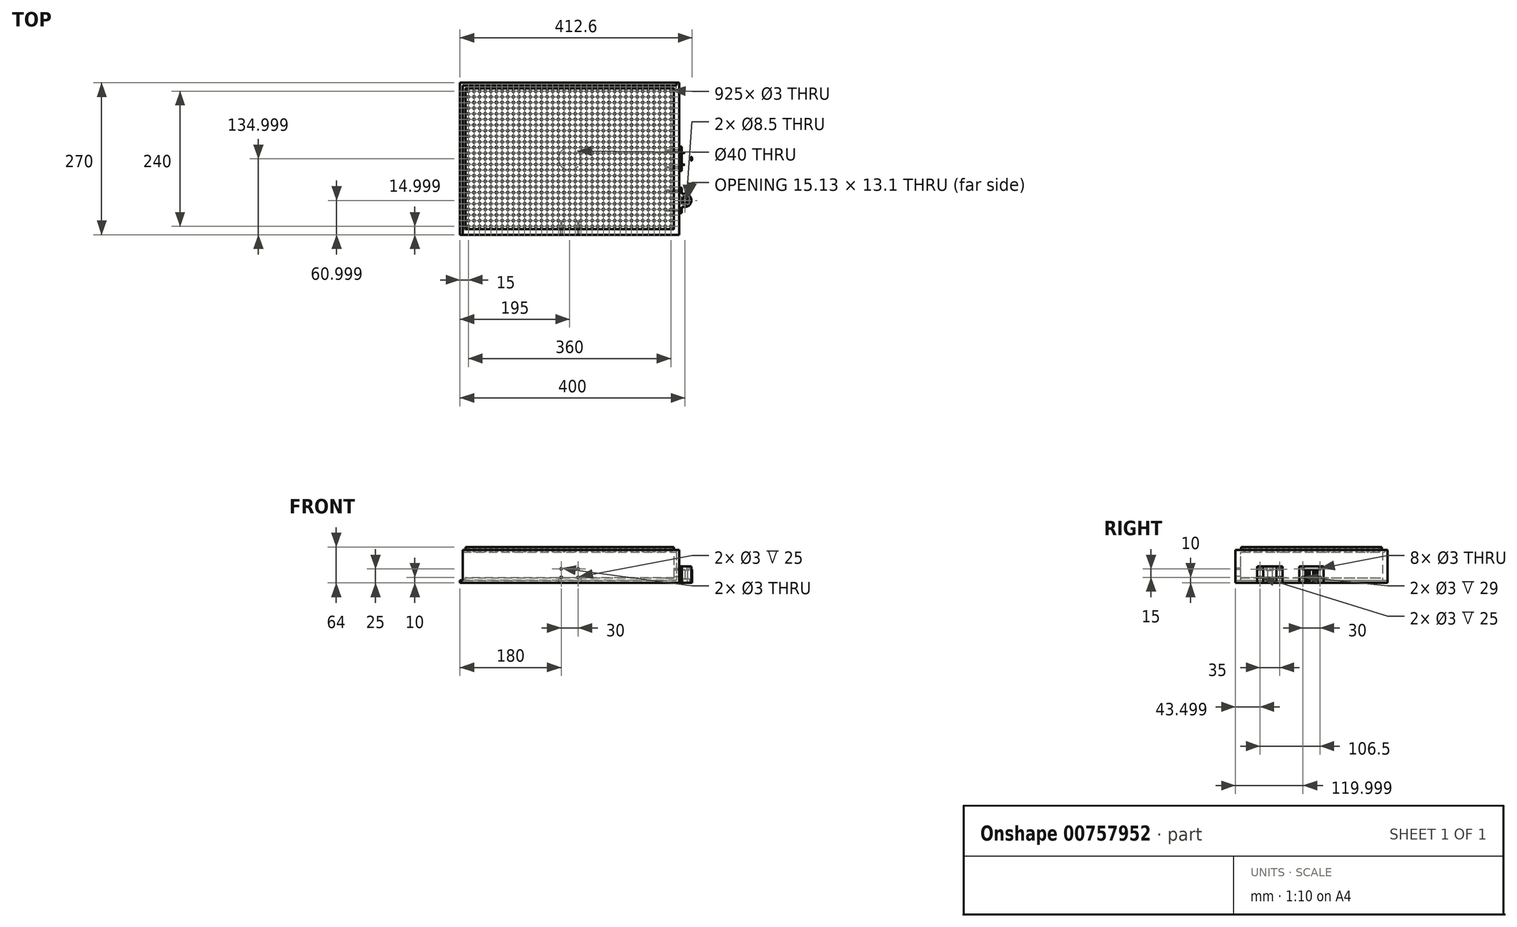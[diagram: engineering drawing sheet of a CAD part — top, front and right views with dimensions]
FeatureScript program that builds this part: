
annotation { "Feature Type Name" : "Feature", "Feature Type Description" : "" }
export const myFeature = defineFeature(function(context is Context, id is Id, definition is map)
    precondition{}
    {
        {
            var Q0;
            Q0=qCreatedBy(makeId("Top.planeOp"),FACE);
            var sketch = newSketch(context, id + "F0", { "sketchPlane" : qUnion([Q0])});
            skLineSegment(sketch, "E0.bottom", {"start": v(-146.05, 133.26) * mm, "end": v(223.95, 133.26) * mm});
            skLineSegment(sketch, "E0.top", {"start": v(-146.05, -116.74) * mm, "end": v(223.95, -116.74) * mm});
            skLineSegment(sketch, "E0.left", {"start": v(-146.05, 133.26) * mm, "end": v(-146.05, -116.74) * mm});
            skLineSegment(sketch, "E0.right", {"start": v(223.95, 133.26) * mm, "end": v(223.95, -116.74) * mm});
            skCircle(sketch, "E1", {"center": v(-141.05, -111.74) * mm, "radius": 1.5 * mm});
            skCircle(sketch, "E2.0.1.0", {"center": v(-141.05, -101.74) * mm, "radius": 1.5 * mm});
            skCircle(sketch, "E2.0.2.0", {"center": v(-141.05, -91.74) * mm, "radius": 1.5 * mm});
            skCircle(sketch, "E2.0.3.0", {"center": v(-141.05, -81.74) * mm, "radius": 1.5 * mm});
            skCircle(sketch, "E2.0.4.0", {"center": v(-141.05, -71.74) * mm, "radius": 1.5 * mm});
            skCircle(sketch, "E2.0.5.0", {"center": v(-141.05, -61.74) * mm, "radius": 1.5 * mm});
            skCircle(sketch, "E2.0.6.0", {"center": v(-141.05, -51.74) * mm, "radius": 1.5 * mm});
            skCircle(sketch, "E2.0.7.0", {"center": v(-141.05, -41.74) * mm, "radius": 1.5 * mm});
            skCircle(sketch, "E2.0.8.0", {"center": v(-141.05, -31.74) * mm, "radius": 1.5 * mm});
            skCircle(sketch, "E2.0.9.0", {"center": v(-141.05, -21.74) * mm, "radius": 1.5 * mm});
            skCircle(sketch, "E2.0.10.0", {"center": v(-141.05, -11.74) * mm, "radius": 1.5 * mm});
            skCircle(sketch, "E2.0.11.0", {"center": v(-141.05, -1.74) * mm, "radius": 1.5 * mm});
            skCircle(sketch, "E2.0.12.0", {"center": v(-141.05, 8.26) * mm, "radius": 1.5 * mm});
            skCircle(sketch, "E2.0.13.0", {"center": v(-141.05, 18.26) * mm, "radius": 1.5 * mm});
            skCircle(sketch, "E2.0.14.0", {"center": v(-141.05, 28.26) * mm, "radius": 1.5 * mm});
            skCircle(sketch, "E2.0.15.0", {"center": v(-141.05, 38.26) * mm, "radius": 1.5 * mm});
            skCircle(sketch, "E2.0.16.0", {"center": v(-141.05, 48.26) * mm, "radius": 1.5 * mm});
            skCircle(sketch, "E2.0.17.0", {"center": v(-141.05, 58.26) * mm, "radius": 1.5 * mm});
            skCircle(sketch, "E2.0.18.0", {"center": v(-141.05, 68.26) * mm, "radius": 1.5 * mm});
            skCircle(sketch, "E2.0.19.0", {"center": v(-141.05, 78.26) * mm, "radius": 1.5 * mm});
            skCircle(sketch, "E2.0.20.0", {"center": v(-141.05, 88.26) * mm, "radius": 1.5 * mm});
            skCircle(sketch, "E2.0.21.0", {"center": v(-141.05, 98.26) * mm, "radius": 1.5 * mm});
            skCircle(sketch, "E2.0.22.0", {"center": v(-141.05, 108.26) * mm, "radius": 1.5 * mm});
            skCircle(sketch, "E2.0.23.0", {"center": v(-141.05, 118.26) * mm, "radius": 1.5 * mm});
            skCircle(sketch, "E2.1.0.0", {"center": v(-131.05, -111.74) * mm, "radius": 1.5 * mm});
            skCircle(sketch, "E2.1.1.0", {"center": v(-131.05, -101.74) * mm, "radius": 1.5 * mm});
            skCircle(sketch, "E2.1.2.0", {"center": v(-131.05, -91.74) * mm, "radius": 1.5 * mm});
            skCircle(sketch, "E2.1.3.0", {"center": v(-131.05, -81.74) * mm, "radius": 1.5 * mm});
            skCircle(sketch, "E2.1.4.0", {"center": v(-131.05, -71.74) * mm, "radius": 1.5 * mm});
            skCircle(sketch, "E2.1.5.0", {"center": v(-131.05, -61.74) * mm, "radius": 1.5 * mm});
            skCircle(sketch, "E2.1.6.0", {"center": v(-131.05, -51.74) * mm, "radius": 1.5 * mm});
            skCircle(sketch, "E2.1.7.0", {"center": v(-131.05, -41.74) * mm, "radius": 1.5 * mm});
            skCircle(sketch, "E2.1.8.0", {"center": v(-131.05, -31.74) * mm, "radius": 1.5 * mm});
            skCircle(sketch, "E2.1.9.0", {"center": v(-131.05, -21.74) * mm, "radius": 1.5 * mm});
            skCircle(sketch, "E2.1.10.0", {"center": v(-131.05, -11.74) * mm, "radius": 1.5 * mm});
            skCircle(sketch, "E2.1.11.0", {"center": v(-131.05, -1.74) * mm, "radius": 1.5 * mm});
            skCircle(sketch, "E2.1.12.0", {"center": v(-131.05, 8.26) * mm, "radius": 1.5 * mm});
            skCircle(sketch, "E2.1.13.0", {"center": v(-131.05, 18.26) * mm, "radius": 1.5 * mm});
            skCircle(sketch, "E2.1.14.0", {"center": v(-131.05, 28.26) * mm, "radius": 1.5 * mm});
            skCircle(sketch, "E2.1.15.0", {"center": v(-131.05, 38.26) * mm, "radius": 1.5 * mm});
            skCircle(sketch, "E2.1.16.0", {"center": v(-131.05, 48.26) * mm, "radius": 1.5 * mm});
            skCircle(sketch, "E2.1.17.0", {"center": v(-131.05, 58.26) * mm, "radius": 1.5 * mm});
            skCircle(sketch, "E2.1.18.0", {"center": v(-131.05, 68.26) * mm, "radius": 1.5 * mm});
            skCircle(sketch, "E2.1.19.0", {"center": v(-131.05, 78.26) * mm, "radius": 1.5 * mm});
            skCircle(sketch, "E2.1.20.0", {"center": v(-131.05, 88.26) * mm, "radius": 1.5 * mm});
            skCircle(sketch, "E2.1.21.0", {"center": v(-131.05, 98.26) * mm, "radius": 1.5 * mm});
            skCircle(sketch, "E2.1.22.0", {"center": v(-131.05, 108.26) * mm, "radius": 1.5 * mm});
            skCircle(sketch, "E2.1.23.0", {"center": v(-131.05, 118.26) * mm, "radius": 1.5 * mm});
            skCircle(sketch, "E2.2.0.0", {"center": v(-121.05, -111.74) * mm, "radius": 1.5 * mm});
            skCircle(sketch, "E2.2.1.0", {"center": v(-121.05, -101.74) * mm, "radius": 1.5 * mm});
            skCircle(sketch, "E2.2.2.0", {"center": v(-121.05, -91.74) * mm, "radius": 1.5 * mm});
            skCircle(sketch, "E2.2.3.0", {"center": v(-121.05, -81.74) * mm, "radius": 1.5 * mm});
            skCircle(sketch, "E2.2.4.0", {"center": v(-121.05, -71.74) * mm, "radius": 1.5 * mm});
            skCircle(sketch, "E2.2.5.0", {"center": v(-121.05, -61.74) * mm, "radius": 1.5 * mm});
            skCircle(sketch, "E2.2.6.0", {"center": v(-121.05, -51.74) * mm, "radius": 1.5 * mm});
            skCircle(sketch, "E2.2.7.0", {"center": v(-121.05, -41.74) * mm, "radius": 1.5 * mm});
            skCircle(sketch, "E2.2.8.0", {"center": v(-121.05, -31.74) * mm, "radius": 1.5 * mm});
            skCircle(sketch, "E2.2.9.0", {"center": v(-121.05, -21.74) * mm, "radius": 1.5 * mm});
            skCircle(sketch, "E2.2.10.0", {"center": v(-121.05, -11.74) * mm, "radius": 1.5 * mm});
            skCircle(sketch, "E2.2.11.0", {"center": v(-121.05, -1.74) * mm, "radius": 1.5 * mm});
            skCircle(sketch, "E2.2.12.0", {"center": v(-121.05, 8.26) * mm, "radius": 1.5 * mm});
            skCircle(sketch, "E2.2.13.0", {"center": v(-121.05, 18.26) * mm, "radius": 1.5 * mm});
            skCircle(sketch, "E2.2.14.0", {"center": v(-121.05, 28.26) * mm, "radius": 1.5 * mm});
            skCircle(sketch, "E2.2.15.0", {"center": v(-121.05, 38.26) * mm, "radius": 1.5 * mm});
            skCircle(sketch, "E2.2.16.0", {"center": v(-121.05, 48.26) * mm, "radius": 1.5 * mm});
            skCircle(sketch, "E2.2.17.0", {"center": v(-121.05, 58.26) * mm, "radius": 1.5 * mm});
            skCircle(sketch, "E2.2.18.0", {"center": v(-121.05, 68.26) * mm, "radius": 1.5 * mm});
            skCircle(sketch, "E2.2.19.0", {"center": v(-121.05, 78.26) * mm, "radius": 1.5 * mm});
            skCircle(sketch, "E2.2.20.0", {"center": v(-121.05, 88.26) * mm, "radius": 1.5 * mm});
            skCircle(sketch, "E2.2.21.0", {"center": v(-121.05, 98.26) * mm, "radius": 1.5 * mm});
            skCircle(sketch, "E2.2.22.0", {"center": v(-121.05, 108.26) * mm, "radius": 1.5 * mm});
            skCircle(sketch, "E2.2.23.0", {"center": v(-121.05, 118.26) * mm, "radius": 1.5 * mm});
            skCircle(sketch, "E2.3.0.0", {"center": v(-111.05, -111.74) * mm, "radius": 1.5 * mm});
            skCircle(sketch, "E2.3.1.0", {"center": v(-111.05, -101.74) * mm, "radius": 1.5 * mm});
            skCircle(sketch, "E2.3.2.0", {"center": v(-111.05, -91.74) * mm, "radius": 1.5 * mm});
            skCircle(sketch, "E2.3.3.0", {"center": v(-111.05, -81.74) * mm, "radius": 1.5 * mm});
            skCircle(sketch, "E2.3.4.0", {"center": v(-111.05, -71.74) * mm, "radius": 1.5 * mm});
            skCircle(sketch, "E2.3.5.0", {"center": v(-111.05, -61.74) * mm, "radius": 1.5 * mm});
            skCircle(sketch, "E2.3.6.0", {"center": v(-111.05, -51.74) * mm, "radius": 1.5 * mm});
            skCircle(sketch, "E2.3.7.0", {"center": v(-111.05, -41.74) * mm, "radius": 1.5 * mm});
            skCircle(sketch, "E2.3.8.0", {"center": v(-111.05, -31.74) * mm, "radius": 1.5 * mm});
            skCircle(sketch, "E2.3.9.0", {"center": v(-111.05, -21.74) * mm, "radius": 1.5 * mm});
            skCircle(sketch, "E2.3.10.0", {"center": v(-111.05, -11.74) * mm, "radius": 1.5 * mm});
            skCircle(sketch, "E2.3.11.0", {"center": v(-111.05, -1.74) * mm, "radius": 1.5 * mm});
            skCircle(sketch, "E2.3.12.0", {"center": v(-111.05, 8.26) * mm, "radius": 1.5 * mm});
            skCircle(sketch, "E2.3.13.0", {"center": v(-111.05, 18.26) * mm, "radius": 1.5 * mm});
            skCircle(sketch, "E2.3.14.0", {"center": v(-111.05, 28.26) * mm, "radius": 1.5 * mm});
            skCircle(sketch, "E2.3.15.0", {"center": v(-111.05, 38.26) * mm, "radius": 1.5 * mm});
            skCircle(sketch, "E2.3.16.0", {"center": v(-111.05, 48.26) * mm, "radius": 1.5 * mm});
            skCircle(sketch, "E2.3.17.0", {"center": v(-111.05, 58.26) * mm, "radius": 1.5 * mm});
            skCircle(sketch, "E2.3.18.0", {"center": v(-111.05, 68.26) * mm, "radius": 1.5 * mm});
            skCircle(sketch, "E2.3.19.0", {"center": v(-111.05, 78.26) * mm, "radius": 1.5 * mm});
            skCircle(sketch, "E2.3.20.0", {"center": v(-111.05, 88.26) * mm, "radius": 1.5 * mm});
            skCircle(sketch, "E2.3.21.0", {"center": v(-111.05, 98.26) * mm, "radius": 1.5 * mm});
            skCircle(sketch, "E2.3.22.0", {"center": v(-111.05, 108.26) * mm, "radius": 1.5 * mm});
            skCircle(sketch, "E2.3.23.0", {"center": v(-111.05, 118.26) * mm, "radius": 1.5 * mm});
            skCircle(sketch, "E2.4.0.0", {"center": v(-101.05, -111.74) * mm, "radius": 1.5 * mm});
            skCircle(sketch, "E2.4.1.0", {"center": v(-101.05, -101.74) * mm, "radius": 1.5 * mm});
            skCircle(sketch, "E2.4.2.0", {"center": v(-101.05, -91.74) * mm, "radius": 1.5 * mm});
            skCircle(sketch, "E2.4.3.0", {"center": v(-101.05, -81.74) * mm, "radius": 1.5 * mm});
            skCircle(sketch, "E2.4.4.0", {"center": v(-101.05, -71.74) * mm, "radius": 1.5 * mm});
            skCircle(sketch, "E2.4.5.0", {"center": v(-101.05, -61.74) * mm, "radius": 1.5 * mm});
            skCircle(sketch, "E2.4.6.0", {"center": v(-101.05, -51.74) * mm, "radius": 1.5 * mm});
            skCircle(sketch, "E2.4.7.0", {"center": v(-101.05, -41.74) * mm, "radius": 1.5 * mm});
            skCircle(sketch, "E2.4.8.0", {"center": v(-101.05, -31.74) * mm, "radius": 1.5 * mm});
            skCircle(sketch, "E2.4.9.0", {"center": v(-101.05, -21.74) * mm, "radius": 1.5 * mm});
            skCircle(sketch, "E2.4.10.0", {"center": v(-101.05, -11.74) * mm, "radius": 1.5 * mm});
            skCircle(sketch, "E2.4.11.0", {"center": v(-101.05, -1.74) * mm, "radius": 1.5 * mm});
            skCircle(sketch, "E2.4.12.0", {"center": v(-101.05, 8.26) * mm, "radius": 1.5 * mm});
            skCircle(sketch, "E2.4.13.0", {"center": v(-101.05, 18.26) * mm, "radius": 1.5 * mm});
            skCircle(sketch, "E2.4.14.0", {"center": v(-101.05, 28.26) * mm, "radius": 1.5 * mm});
            skCircle(sketch, "E2.4.15.0", {"center": v(-101.05, 38.26) * mm, "radius": 1.5 * mm});
            skCircle(sketch, "E2.4.16.0", {"center": v(-101.05, 48.26) * mm, "radius": 1.5 * mm});
            skCircle(sketch, "E2.4.17.0", {"center": v(-101.05, 58.26) * mm, "radius": 1.5 * mm});
            skCircle(sketch, "E2.4.18.0", {"center": v(-101.05, 68.26) * mm, "radius": 1.5 * mm});
            skCircle(sketch, "E2.4.19.0", {"center": v(-101.05, 78.26) * mm, "radius": 1.5 * mm});
            skCircle(sketch, "E2.4.20.0", {"center": v(-101.05, 88.26) * mm, "radius": 1.5 * mm});
            skCircle(sketch, "E2.4.21.0", {"center": v(-101.05, 98.26) * mm, "radius": 1.5 * mm});
            skCircle(sketch, "E2.4.22.0", {"center": v(-101.05, 108.26) * mm, "radius": 1.5 * mm});
            skCircle(sketch, "E2.4.23.0", {"center": v(-101.05, 118.26) * mm, "radius": 1.5 * mm});
            skCircle(sketch, "E2.5.0.0", {"center": v(-91.05, -111.74) * mm, "radius": 1.5 * mm});
            skCircle(sketch, "E2.5.1.0", {"center": v(-91.05, -101.74) * mm, "radius": 1.5 * mm});
            skCircle(sketch, "E2.5.2.0", {"center": v(-91.05, -91.74) * mm, "radius": 1.5 * mm});
            skCircle(sketch, "E2.5.3.0", {"center": v(-91.05, -81.74) * mm, "radius": 1.5 * mm});
            skCircle(sketch, "E2.5.4.0", {"center": v(-91.05, -71.74) * mm, "radius": 1.5 * mm});
            skCircle(sketch, "E2.5.5.0", {"center": v(-91.05, -61.74) * mm, "radius": 1.5 * mm});
            skCircle(sketch, "E2.5.6.0", {"center": v(-91.05, -51.74) * mm, "radius": 1.5 * mm});
            skCircle(sketch, "E2.5.7.0", {"center": v(-91.05, -41.74) * mm, "radius": 1.5 * mm});
            skCircle(sketch, "E2.5.8.0", {"center": v(-91.05, -31.74) * mm, "radius": 1.5 * mm});
            skCircle(sketch, "E2.5.9.0", {"center": v(-91.05, -21.74) * mm, "radius": 1.5 * mm});
            skCircle(sketch, "E2.5.10.0", {"center": v(-91.05, -11.74) * mm, "radius": 1.5 * mm});
            skCircle(sketch, "E2.5.11.0", {"center": v(-91.05, -1.74) * mm, "radius": 1.5 * mm});
            skCircle(sketch, "E2.5.12.0", {"center": v(-91.05, 8.26) * mm, "radius": 1.5 * mm});
            skCircle(sketch, "E2.5.13.0", {"center": v(-91.05, 18.26) * mm, "radius": 1.5 * mm});
            skCircle(sketch, "E2.5.14.0", {"center": v(-91.05, 28.26) * mm, "radius": 1.5 * mm});
            skCircle(sketch, "E2.5.15.0", {"center": v(-91.05, 38.26) * mm, "radius": 1.5 * mm});
            skCircle(sketch, "E2.5.16.0", {"center": v(-91.05, 48.26) * mm, "radius": 1.5 * mm});
            skCircle(sketch, "E2.5.17.0", {"center": v(-91.05, 58.26) * mm, "radius": 1.5 * mm});
            skCircle(sketch, "E2.5.18.0", {"center": v(-91.05, 68.26) * mm, "radius": 1.5 * mm});
            skCircle(sketch, "E2.5.19.0", {"center": v(-91.05, 78.26) * mm, "radius": 1.5 * mm});
            skCircle(sketch, "E2.5.20.0", {"center": v(-91.05, 88.26) * mm, "radius": 1.5 * mm});
            skCircle(sketch, "E2.5.21.0", {"center": v(-91.05, 98.26) * mm, "radius": 1.5 * mm});
            skCircle(sketch, "E2.5.22.0", {"center": v(-91.05, 108.26) * mm, "radius": 1.5 * mm});
            skCircle(sketch, "E2.5.23.0", {"center": v(-91.05, 118.26) * mm, "radius": 1.5 * mm});
            skCircle(sketch, "E2.6.0.0", {"center": v(-81.05, -111.74) * mm, "radius": 1.5 * mm});
            skCircle(sketch, "E2.6.1.0", {"center": v(-81.05, -101.74) * mm, "radius": 1.5 * mm});
            skCircle(sketch, "E2.6.2.0", {"center": v(-81.05, -91.74) * mm, "radius": 1.5 * mm});
            skCircle(sketch, "E2.6.3.0", {"center": v(-81.05, -81.74) * mm, "radius": 1.5 * mm});
            skCircle(sketch, "E2.6.4.0", {"center": v(-81.05, -71.74) * mm, "radius": 1.5 * mm});
            skCircle(sketch, "E2.6.5.0", {"center": v(-81.05, -61.74) * mm, "radius": 1.5 * mm});
            skCircle(sketch, "E2.6.6.0", {"center": v(-81.05, -51.74) * mm, "radius": 1.5 * mm});
            skCircle(sketch, "E2.6.7.0", {"center": v(-81.05, -41.74) * mm, "radius": 1.5 * mm});
            skCircle(sketch, "E2.6.8.0", {"center": v(-81.05, -31.74) * mm, "radius": 1.5 * mm});
            skCircle(sketch, "E2.6.9.0", {"center": v(-81.05, -21.74) * mm, "radius": 1.5 * mm});
            skCircle(sketch, "E2.6.10.0", {"center": v(-81.05, -11.74) * mm, "radius": 1.5 * mm});
            skCircle(sketch, "E2.6.11.0", {"center": v(-81.05, -1.74) * mm, "radius": 1.5 * mm});
            skCircle(sketch, "E2.6.12.0", {"center": v(-81.05, 8.26) * mm, "radius": 1.5 * mm});
            skCircle(sketch, "E2.6.13.0", {"center": v(-81.05, 18.26) * mm, "radius": 1.5 * mm});
            skCircle(sketch, "E2.6.14.0", {"center": v(-81.05, 28.26) * mm, "radius": 1.5 * mm});
            skCircle(sketch, "E2.6.15.0", {"center": v(-81.05, 38.26) * mm, "radius": 1.5 * mm});
            skCircle(sketch, "E2.6.16.0", {"center": v(-81.05, 48.26) * mm, "radius": 1.5 * mm});
            skCircle(sketch, "E2.6.17.0", {"center": v(-81.05, 58.26) * mm, "radius": 1.5 * mm});
            skCircle(sketch, "E2.6.18.0", {"center": v(-81.05, 68.26) * mm, "radius": 1.5 * mm});
            skCircle(sketch, "E2.6.19.0", {"center": v(-81.05, 78.26) * mm, "radius": 1.5 * mm});
            skCircle(sketch, "E2.6.20.0", {"center": v(-81.05, 88.26) * mm, "radius": 1.5 * mm});
            skCircle(sketch, "E2.6.21.0", {"center": v(-81.05, 98.26) * mm, "radius": 1.5 * mm});
            skCircle(sketch, "E2.6.22.0", {"center": v(-81.05, 108.26) * mm, "radius": 1.5 * mm});
            skCircle(sketch, "E2.6.23.0", {"center": v(-81.05, 118.26) * mm, "radius": 1.5 * mm});
            skCircle(sketch, "E2.7.0.0", {"center": v(-71.05, -111.74) * mm, "radius": 1.5 * mm});
            skCircle(sketch, "E2.7.1.0", {"center": v(-71.05, -101.74) * mm, "radius": 1.5 * mm});
            skCircle(sketch, "E2.7.2.0", {"center": v(-71.05, -91.74) * mm, "radius": 1.5 * mm});
            skCircle(sketch, "E2.7.3.0", {"center": v(-71.05, -81.74) * mm, "radius": 1.5 * mm});
            skCircle(sketch, "E2.7.4.0", {"center": v(-71.05, -71.74) * mm, "radius": 1.5 * mm});
            skCircle(sketch, "E2.7.5.0", {"center": v(-71.05, -61.74) * mm, "radius": 1.5 * mm});
            skCircle(sketch, "E2.7.6.0", {"center": v(-71.05, -51.74) * mm, "radius": 1.5 * mm});
            skCircle(sketch, "E2.7.7.0", {"center": v(-71.05, -41.74) * mm, "radius": 1.5 * mm});
            skCircle(sketch, "E2.7.8.0", {"center": v(-71.05, -31.74) * mm, "radius": 1.5 * mm});
            skCircle(sketch, "E2.7.9.0", {"center": v(-71.05, -21.74) * mm, "radius": 1.5 * mm});
            skCircle(sketch, "E2.7.10.0", {"center": v(-71.05, -11.74) * mm, "radius": 1.5 * mm});
            skCircle(sketch, "E2.7.11.0", {"center": v(-71.05, -1.74) * mm, "radius": 1.5 * mm});
            skCircle(sketch, "E2.7.12.0", {"center": v(-71.05, 8.26) * mm, "radius": 1.5 * mm});
            skCircle(sketch, "E2.7.13.0", {"center": v(-71.05, 18.26) * mm, "radius": 1.5 * mm});
            skCircle(sketch, "E2.7.14.0", {"center": v(-71.05, 28.26) * mm, "radius": 1.5 * mm});
            skCircle(sketch, "E2.7.15.0", {"center": v(-71.05, 38.26) * mm, "radius": 1.5 * mm});
            skCircle(sketch, "E2.7.16.0", {"center": v(-71.05, 48.26) * mm, "radius": 1.5 * mm});
            skCircle(sketch, "E2.7.17.0", {"center": v(-71.05, 58.26) * mm, "radius": 1.5 * mm});
            skCircle(sketch, "E2.7.18.0", {"center": v(-71.05, 68.26) * mm, "radius": 1.5 * mm});
            skCircle(sketch, "E2.7.19.0", {"center": v(-71.05, 78.26) * mm, "radius": 1.5 * mm});
            skCircle(sketch, "E2.7.20.0", {"center": v(-71.05, 88.26) * mm, "radius": 1.5 * mm});
            skCircle(sketch, "E2.7.21.0", {"center": v(-71.05, 98.26) * mm, "radius": 1.5 * mm});
            skCircle(sketch, "E2.7.22.0", {"center": v(-71.05, 108.26) * mm, "radius": 1.5 * mm});
            skCircle(sketch, "E2.7.23.0", {"center": v(-71.05, 118.26) * mm, "radius": 1.5 * mm});
            skCircle(sketch, "E2.8.0.0", {"center": v(-61.05, -111.74) * mm, "radius": 1.5 * mm});
            skCircle(sketch, "E2.8.1.0", {"center": v(-61.05, -101.74) * mm, "radius": 1.5 * mm});
            skCircle(sketch, "E2.8.2.0", {"center": v(-61.05, -91.74) * mm, "radius": 1.5 * mm});
            skCircle(sketch, "E2.8.3.0", {"center": v(-61.05, -81.74) * mm, "radius": 1.5 * mm});
            skCircle(sketch, "E2.8.4.0", {"center": v(-61.05, -71.74) * mm, "radius": 1.5 * mm});
            skCircle(sketch, "E2.8.5.0", {"center": v(-61.05, -61.74) * mm, "radius": 1.5 * mm});
            skCircle(sketch, "E2.8.6.0", {"center": v(-61.05, -51.74) * mm, "radius": 1.5 * mm});
            skCircle(sketch, "E2.8.7.0", {"center": v(-61.05, -41.74) * mm, "radius": 1.5 * mm});
            skCircle(sketch, "E2.8.8.0", {"center": v(-61.05, -31.74) * mm, "radius": 1.5 * mm});
            skCircle(sketch, "E2.8.9.0", {"center": v(-61.05, -21.74) * mm, "radius": 1.5 * mm});
            skCircle(sketch, "E2.8.10.0", {"center": v(-61.05, -11.74) * mm, "radius": 1.5 * mm});
            skCircle(sketch, "E2.8.11.0", {"center": v(-61.05, -1.74) * mm, "radius": 1.5 * mm});
            skCircle(sketch, "E2.8.12.0", {"center": v(-61.05, 8.26) * mm, "radius": 1.5 * mm});
            skCircle(sketch, "E2.8.13.0", {"center": v(-61.05, 18.26) * mm, "radius": 1.5 * mm});
            skCircle(sketch, "E2.8.14.0", {"center": v(-61.05, 28.26) * mm, "radius": 1.5 * mm});
            skCircle(sketch, "E2.8.15.0", {"center": v(-61.05, 38.26) * mm, "radius": 1.5 * mm});
            skCircle(sketch, "E2.8.16.0", {"center": v(-61.05, 48.26) * mm, "radius": 1.5 * mm});
            skCircle(sketch, "E2.8.17.0", {"center": v(-61.05, 58.26) * mm, "radius": 1.5 * mm});
            skCircle(sketch, "E2.8.18.0", {"center": v(-61.05, 68.26) * mm, "radius": 1.5 * mm});
            skCircle(sketch, "E2.8.19.0", {"center": v(-61.05, 78.26) * mm, "radius": 1.5 * mm});
            skCircle(sketch, "E2.8.20.0", {"center": v(-61.05, 88.26) * mm, "radius": 1.5 * mm});
            skCircle(sketch, "E2.8.21.0", {"center": v(-61.05, 98.26) * mm, "radius": 1.5 * mm});
            skCircle(sketch, "E2.8.22.0", {"center": v(-61.05, 108.26) * mm, "radius": 1.5 * mm});
            skCircle(sketch, "E2.8.23.0", {"center": v(-61.05, 118.26) * mm, "radius": 1.5 * mm});
            skCircle(sketch, "E2.9.0.0", {"center": v(-51.05, -111.74) * mm, "radius": 1.5 * mm});
            skCircle(sketch, "E2.9.1.0", {"center": v(-51.05, -101.74) * mm, "radius": 1.5 * mm});
            skCircle(sketch, "E2.9.2.0", {"center": v(-51.05, -91.74) * mm, "radius": 1.5 * mm});
            skCircle(sketch, "E2.9.3.0", {"center": v(-51.05, -81.74) * mm, "radius": 1.5 * mm});
            skCircle(sketch, "E2.9.4.0", {"center": v(-51.05, -71.74) * mm, "radius": 1.5 * mm});
            skCircle(sketch, "E2.9.5.0", {"center": v(-51.05, -61.74) * mm, "radius": 1.5 * mm});
            skCircle(sketch, "E2.9.6.0", {"center": v(-51.05, -51.74) * mm, "radius": 1.5 * mm});
            skCircle(sketch, "E2.9.7.0", {"center": v(-51.05, -41.74) * mm, "radius": 1.5 * mm});
            skCircle(sketch, "E2.9.8.0", {"center": v(-51.05, -31.74) * mm, "radius": 1.5 * mm});
            skCircle(sketch, "E2.9.9.0", {"center": v(-51.05, -21.74) * mm, "radius": 1.5 * mm});
            skCircle(sketch, "E2.9.10.0", {"center": v(-51.05, -11.74) * mm, "radius": 1.5 * mm});
            skCircle(sketch, "E2.9.11.0", {"center": v(-51.05, -1.74) * mm, "radius": 1.5 * mm});
            skCircle(sketch, "E2.9.12.0", {"center": v(-51.05, 8.26) * mm, "radius": 1.5 * mm});
            skCircle(sketch, "E2.9.13.0", {"center": v(-51.05, 18.26) * mm, "radius": 1.5 * mm});
            skCircle(sketch, "E2.9.14.0", {"center": v(-51.05, 28.26) * mm, "radius": 1.5 * mm});
            skCircle(sketch, "E2.9.15.0", {"center": v(-51.05, 38.26) * mm, "radius": 1.5 * mm});
            skCircle(sketch, "E2.9.16.0", {"center": v(-51.05, 48.26) * mm, "radius": 1.5 * mm});
            skCircle(sketch, "E2.9.17.0", {"center": v(-51.05, 58.26) * mm, "radius": 1.5 * mm});
            skCircle(sketch, "E2.9.18.0", {"center": v(-51.05, 68.26) * mm, "radius": 1.5 * mm});
            skCircle(sketch, "E2.9.19.0", {"center": v(-51.05, 78.26) * mm, "radius": 1.5 * mm});
            skCircle(sketch, "E2.9.20.0", {"center": v(-51.05, 88.26) * mm, "radius": 1.5 * mm});
            skCircle(sketch, "E2.9.21.0", {"center": v(-51.05, 98.26) * mm, "radius": 1.5 * mm});
            skCircle(sketch, "E2.9.22.0", {"center": v(-51.05, 108.26) * mm, "radius": 1.5 * mm});
            skCircle(sketch, "E2.9.23.0", {"center": v(-51.05, 118.26) * mm, "radius": 1.5 * mm});
            skCircle(sketch, "E2.10.0.0", {"center": v(-41.05, -111.74) * mm, "radius": 1.5 * mm});
            skCircle(sketch, "E2.10.1.0", {"center": v(-41.05, -101.74) * mm, "radius": 1.5 * mm});
            skCircle(sketch, "E2.10.2.0", {"center": v(-41.05, -91.74) * mm, "radius": 1.5 * mm});
            skCircle(sketch, "E2.10.3.0", {"center": v(-41.05, -81.74) * mm, "radius": 1.5 * mm});
            skCircle(sketch, "E2.10.4.0", {"center": v(-41.05, -71.74) * mm, "radius": 1.5 * mm});
            skCircle(sketch, "E2.10.5.0", {"center": v(-41.05, -61.74) * mm, "radius": 1.5 * mm});
            skCircle(sketch, "E2.10.6.0", {"center": v(-41.05, -51.74) * mm, "radius": 1.5 * mm});
            skCircle(sketch, "E2.10.7.0", {"center": v(-41.05, -41.74) * mm, "radius": 1.5 * mm});
            skCircle(sketch, "E2.10.8.0", {"center": v(-41.05, -31.74) * mm, "radius": 1.5 * mm});
            skCircle(sketch, "E2.10.9.0", {"center": v(-41.05, -21.74) * mm, "radius": 1.5 * mm});
            skCircle(sketch, "E2.10.10.0", {"center": v(-41.05, -11.74) * mm, "radius": 1.5 * mm});
            skCircle(sketch, "E2.10.11.0", {"center": v(-41.05, -1.74) * mm, "radius": 1.5 * mm});
            skCircle(sketch, "E2.10.12.0", {"center": v(-41.05, 8.26) * mm, "radius": 1.5 * mm});
            skCircle(sketch, "E2.10.13.0", {"center": v(-41.05, 18.26) * mm, "radius": 1.5 * mm});
            skCircle(sketch, "E2.10.14.0", {"center": v(-41.05, 28.26) * mm, "radius": 1.5 * mm});
            skCircle(sketch, "E2.10.15.0", {"center": v(-41.05, 38.26) * mm, "radius": 1.5 * mm});
            skCircle(sketch, "E2.10.16.0", {"center": v(-41.05, 48.26) * mm, "radius": 1.5 * mm});
            skCircle(sketch, "E2.10.17.0", {"center": v(-41.05, 58.26) * mm, "radius": 1.5 * mm});
            skCircle(sketch, "E2.10.18.0", {"center": v(-41.05, 68.26) * mm, "radius": 1.5 * mm});
            skCircle(sketch, "E2.10.19.0", {"center": v(-41.05, 78.26) * mm, "radius": 1.5 * mm});
            skCircle(sketch, "E2.10.20.0", {"center": v(-41.05, 88.26) * mm, "radius": 1.5 * mm});
            skCircle(sketch, "E2.10.21.0", {"center": v(-41.05, 98.26) * mm, "radius": 1.5 * mm});
            skCircle(sketch, "E2.10.22.0", {"center": v(-41.05, 108.26) * mm, "radius": 1.5 * mm});
            skCircle(sketch, "E2.10.23.0", {"center": v(-41.05, 118.26) * mm, "radius": 1.5 * mm});
            skCircle(sketch, "E2.11.0.0", {"center": v(-31.05, -111.74) * mm, "radius": 1.5 * mm});
            skCircle(sketch, "E2.11.1.0", {"center": v(-31.05, -101.74) * mm, "radius": 1.5 * mm});
            skCircle(sketch, "E2.11.2.0", {"center": v(-31.05, -91.74) * mm, "radius": 1.5 * mm});
            skCircle(sketch, "E2.11.3.0", {"center": v(-31.05, -81.74) * mm, "radius": 1.5 * mm});
            skCircle(sketch, "E2.11.4.0", {"center": v(-31.05, -71.74) * mm, "radius": 1.5 * mm});
            skCircle(sketch, "E2.11.5.0", {"center": v(-31.05, -61.74) * mm, "radius": 1.5 * mm});
            skCircle(sketch, "E2.11.6.0", {"center": v(-31.05, -51.74) * mm, "radius": 1.5 * mm});
            skCircle(sketch, "E2.11.7.0", {"center": v(-31.05, -41.74) * mm, "radius": 1.5 * mm});
            skCircle(sketch, "E2.11.8.0", {"center": v(-31.05, -31.74) * mm, "radius": 1.5 * mm});
            skCircle(sketch, "E2.11.9.0", {"center": v(-31.05, -21.74) * mm, "radius": 1.5 * mm});
            skCircle(sketch, "E2.11.10.0", {"center": v(-31.05, -11.74) * mm, "radius": 1.5 * mm});
            skCircle(sketch, "E2.11.11.0", {"center": v(-31.05, -1.74) * mm, "radius": 1.5 * mm});
            skCircle(sketch, "E2.11.12.0", {"center": v(-31.05, 8.26) * mm, "radius": 1.5 * mm});
            skCircle(sketch, "E2.11.13.0", {"center": v(-31.05, 18.26) * mm, "radius": 1.5 * mm});
            skCircle(sketch, "E2.11.14.0", {"center": v(-31.05, 28.26) * mm, "radius": 1.5 * mm});
            skCircle(sketch, "E2.11.15.0", {"center": v(-31.05, 38.26) * mm, "radius": 1.5 * mm});
            skCircle(sketch, "E2.11.16.0", {"center": v(-31.05, 48.26) * mm, "radius": 1.5 * mm});
            skCircle(sketch, "E2.11.17.0", {"center": v(-31.05, 58.26) * mm, "radius": 1.5 * mm});
            skCircle(sketch, "E2.11.18.0", {"center": v(-31.05, 68.26) * mm, "radius": 1.5 * mm});
            skCircle(sketch, "E2.11.19.0", {"center": v(-31.05, 78.26) * mm, "radius": 1.5 * mm});
            skCircle(sketch, "E2.11.20.0", {"center": v(-31.05, 88.26) * mm, "radius": 1.5 * mm});
            skCircle(sketch, "E2.11.21.0", {"center": v(-31.05, 98.26) * mm, "radius": 1.5 * mm});
            skCircle(sketch, "E2.11.22.0", {"center": v(-31.05, 108.26) * mm, "radius": 1.5 * mm});
            skCircle(sketch, "E2.11.23.0", {"center": v(-31.05, 118.26) * mm, "radius": 1.5 * mm});
            skCircle(sketch, "E2.12.0.0", {"center": v(-21.05, -111.74) * mm, "radius": 1.5 * mm});
            skCircle(sketch, "E2.12.1.0", {"center": v(-21.05, -101.74) * mm, "radius": 1.5 * mm});
            skCircle(sketch, "E2.12.2.0", {"center": v(-21.05, -91.74) * mm, "radius": 1.5 * mm});
            skCircle(sketch, "E2.12.3.0", {"center": v(-21.05, -81.74) * mm, "radius": 1.5 * mm});
            skCircle(sketch, "E2.12.4.0", {"center": v(-21.05, -71.74) * mm, "radius": 1.5 * mm});
            skCircle(sketch, "E2.12.5.0", {"center": v(-21.05, -61.74) * mm, "radius": 1.5 * mm});
            skCircle(sketch, "E2.12.6.0", {"center": v(-21.05, -51.74) * mm, "radius": 1.5 * mm});
            skCircle(sketch, "E2.12.7.0", {"center": v(-21.05, -41.74) * mm, "radius": 1.5 * mm});
            skCircle(sketch, "E2.12.8.0", {"center": v(-21.05, -31.74) * mm, "radius": 1.5 * mm});
            skCircle(sketch, "E2.12.9.0", {"center": v(-21.05, -21.74) * mm, "radius": 1.5 * mm});
            skCircle(sketch, "E2.12.10.0", {"center": v(-21.05, -11.74) * mm, "radius": 1.5 * mm});
            skCircle(sketch, "E2.12.11.0", {"center": v(-21.05, -1.74) * mm, "radius": 1.5 * mm});
            skCircle(sketch, "E2.12.12.0", {"center": v(-21.05, 8.26) * mm, "radius": 1.5 * mm});
            skCircle(sketch, "E2.12.13.0", {"center": v(-21.05, 18.26) * mm, "radius": 1.5 * mm});
            skCircle(sketch, "E2.12.14.0", {"center": v(-21.05, 28.26) * mm, "radius": 1.5 * mm});
            skCircle(sketch, "E2.12.15.0", {"center": v(-21.05, 38.26) * mm, "radius": 1.5 * mm});
            skCircle(sketch, "E2.12.16.0", {"center": v(-21.05, 48.26) * mm, "radius": 1.5 * mm});
            skCircle(sketch, "E2.12.17.0", {"center": v(-21.05, 58.26) * mm, "radius": 1.5 * mm});
            skCircle(sketch, "E2.12.18.0", {"center": v(-21.05, 68.26) * mm, "radius": 1.5 * mm});
            skCircle(sketch, "E2.12.19.0", {"center": v(-21.05, 78.26) * mm, "radius": 1.5 * mm});
            skCircle(sketch, "E2.12.20.0", {"center": v(-21.05, 88.26) * mm, "radius": 1.5 * mm});
            skCircle(sketch, "E2.12.21.0", {"center": v(-21.05, 98.26) * mm, "radius": 1.5 * mm});
            skCircle(sketch, "E2.12.22.0", {"center": v(-21.05, 108.26) * mm, "radius": 1.5 * mm});
            skCircle(sketch, "E2.12.23.0", {"center": v(-21.05, 118.26) * mm, "radius": 1.5 * mm});
            skCircle(sketch, "E2.13.0.0", {"center": v(-11.05, -111.74) * mm, "radius": 1.5 * mm});
            skCircle(sketch, "E2.13.1.0", {"center": v(-11.05, -101.74) * mm, "radius": 1.5 * mm});
            skCircle(sketch, "E2.13.2.0", {"center": v(-11.05, -91.74) * mm, "radius": 1.5 * mm});
            skCircle(sketch, "E2.13.3.0", {"center": v(-11.05, -81.74) * mm, "radius": 1.5 * mm});
            skCircle(sketch, "E2.13.4.0", {"center": v(-11.05, -71.74) * mm, "radius": 1.5 * mm});
            skCircle(sketch, "E2.13.5.0", {"center": v(-11.05, -61.74) * mm, "radius": 1.5 * mm});
            skCircle(sketch, "E2.13.6.0", {"center": v(-11.05, -51.74) * mm, "radius": 1.5 * mm});
            skCircle(sketch, "E2.13.7.0", {"center": v(-11.05, -41.74) * mm, "radius": 1.5 * mm});
            skCircle(sketch, "E2.13.8.0", {"center": v(-11.05, -31.74) * mm, "radius": 1.5 * mm});
            skCircle(sketch, "E2.13.9.0", {"center": v(-11.05, -21.74) * mm, "radius": 1.5 * mm});
            skCircle(sketch, "E2.13.10.0", {"center": v(-11.05, -11.74) * mm, "radius": 1.5 * mm});
            skCircle(sketch, "E2.13.11.0", {"center": v(-11.05, -1.74) * mm, "radius": 1.5 * mm});
            skCircle(sketch, "E2.13.12.0", {"center": v(-11.05, 8.26) * mm, "radius": 1.5 * mm});
            skCircle(sketch, "E2.13.13.0", {"center": v(-11.05, 18.26) * mm, "radius": 1.5 * mm});
            skCircle(sketch, "E2.13.14.0", {"center": v(-11.05, 28.26) * mm, "radius": 1.5 * mm});
            skCircle(sketch, "E2.13.15.0", {"center": v(-11.05, 38.26) * mm, "radius": 1.5 * mm});
            skCircle(sketch, "E2.13.16.0", {"center": v(-11.05, 48.26) * mm, "radius": 1.5 * mm});
            skCircle(sketch, "E2.13.17.0", {"center": v(-11.05, 58.26) * mm, "radius": 1.5 * mm});
            skCircle(sketch, "E2.13.18.0", {"center": v(-11.05, 68.26) * mm, "radius": 1.5 * mm});
            skCircle(sketch, "E2.13.19.0", {"center": v(-11.05, 78.26) * mm, "radius": 1.5 * mm});
            skCircle(sketch, "E2.13.20.0", {"center": v(-11.05, 88.26) * mm, "radius": 1.5 * mm});
            skCircle(sketch, "E2.13.21.0", {"center": v(-11.05, 98.26) * mm, "radius": 1.5 * mm});
            skCircle(sketch, "E2.13.22.0", {"center": v(-11.05, 108.26) * mm, "radius": 1.5 * mm});
            skCircle(sketch, "E2.13.23.0", {"center": v(-11.05, 118.26) * mm, "radius": 1.5 * mm});
            skCircle(sketch, "E2.14.0.0", {"center": v(-1.05, -111.74) * mm, "radius": 1.5 * mm});
            skCircle(sketch, "E2.14.1.0", {"center": v(-1.05, -101.74) * mm, "radius": 1.5 * mm});
            skCircle(sketch, "E2.14.2.0", {"center": v(-1.05, -91.74) * mm, "radius": 1.5 * mm});
            skCircle(sketch, "E2.14.3.0", {"center": v(-1.05, -81.74) * mm, "radius": 1.5 * mm});
            skCircle(sketch, "E2.14.4.0", {"center": v(-1.05, -71.74) * mm, "radius": 1.5 * mm});
            skCircle(sketch, "E2.14.5.0", {"center": v(-1.05, -61.74) * mm, "radius": 1.5 * mm});
            skCircle(sketch, "E2.14.6.0", {"center": v(-1.05, -51.74) * mm, "radius": 1.5 * mm});
            skCircle(sketch, "E2.14.7.0", {"center": v(-1.05, -41.74) * mm, "radius": 1.5 * mm});
            skCircle(sketch, "E2.14.8.0", {"center": v(-1.05, -31.74) * mm, "radius": 1.5 * mm});
            skCircle(sketch, "E2.14.9.0", {"center": v(-1.05, -21.74) * mm, "radius": 1.5 * mm});
            skCircle(sketch, "E2.14.10.0", {"center": v(-1.05, -11.74) * mm, "radius": 1.5 * mm});
            skCircle(sketch, "E2.14.11.0", {"center": v(-1.05, -1.74) * mm, "radius": 1.5 * mm});
            skCircle(sketch, "E2.14.12.0", {"center": v(-1.05, 8.26) * mm, "radius": 1.5 * mm});
            skCircle(sketch, "E2.14.13.0", {"center": v(-1.05, 18.26) * mm, "radius": 1.5 * mm});
            skCircle(sketch, "E2.14.14.0", {"center": v(-1.05, 28.26) * mm, "radius": 1.5 * mm});
            skCircle(sketch, "E2.14.15.0", {"center": v(-1.05, 38.26) * mm, "radius": 1.5 * mm});
            skCircle(sketch, "E2.14.16.0", {"center": v(-1.05, 48.26) * mm, "radius": 1.5 * mm});
            skCircle(sketch, "E2.14.17.0", {"center": v(-1.05, 58.26) * mm, "radius": 1.5 * mm});
            skCircle(sketch, "E2.14.18.0", {"center": v(-1.05, 68.26) * mm, "radius": 1.5 * mm});
            skCircle(sketch, "E2.14.19.0", {"center": v(-1.05, 78.26) * mm, "radius": 1.5 * mm});
            skCircle(sketch, "E2.14.20.0", {"center": v(-1.05, 88.26) * mm, "radius": 1.5 * mm});
            skCircle(sketch, "E2.14.21.0", {"center": v(-1.05, 98.26) * mm, "radius": 1.5 * mm});
            skCircle(sketch, "E2.14.22.0", {"center": v(-1.05, 108.26) * mm, "radius": 1.5 * mm});
            skCircle(sketch, "E2.14.23.0", {"center": v(-1.05, 118.26) * mm, "radius": 1.5 * mm});
            skCircle(sketch, "E2.15.0.0", {"center": v(8.95, -111.74) * mm, "radius": 1.5 * mm});
            skCircle(sketch, "E2.15.1.0", {"center": v(8.95, -101.74) * mm, "radius": 1.5 * mm});
            skCircle(sketch, "E2.15.2.0", {"center": v(8.95, -91.74) * mm, "radius": 1.5 * mm});
            skCircle(sketch, "E2.15.3.0", {"center": v(8.95, -81.74) * mm, "radius": 1.5 * mm});
            skCircle(sketch, "E2.15.4.0", {"center": v(8.95, -71.74) * mm, "radius": 1.5 * mm});
            skCircle(sketch, "E2.15.5.0", {"center": v(8.95, -61.74) * mm, "radius": 1.5 * mm});
            skCircle(sketch, "E2.15.6.0", {"center": v(8.95, -51.74) * mm, "radius": 1.5 * mm});
            skCircle(sketch, "E2.15.7.0", {"center": v(8.95, -41.74) * mm, "radius": 1.5 * mm});
            skCircle(sketch, "E2.15.8.0", {"center": v(8.95, -31.74) * mm, "radius": 1.5 * mm});
            skCircle(sketch, "E2.15.9.0", {"center": v(8.95, -21.74) * mm, "radius": 1.5 * mm});
            skCircle(sketch, "E2.15.10.0", {"center": v(8.95, -11.74) * mm, "radius": 1.5 * mm});
            skCircle(sketch, "E2.15.11.0", {"center": v(8.95, -1.74) * mm, "radius": 1.5 * mm});
            skCircle(sketch, "E2.15.12.0", {"center": v(8.95, 8.26) * mm, "radius": 1.5 * mm});
            skCircle(sketch, "E2.15.13.0", {"center": v(8.95, 18.26) * mm, "radius": 1.5 * mm});
            skCircle(sketch, "E2.15.14.0", {"center": v(8.95, 28.26) * mm, "radius": 1.5 * mm});
            skCircle(sketch, "E2.15.15.0", {"center": v(8.95, 38.26) * mm, "radius": 1.5 * mm});
            skCircle(sketch, "E2.15.16.0", {"center": v(8.95, 48.26) * mm, "radius": 1.5 * mm});
            skCircle(sketch, "E2.15.17.0", {"center": v(8.95, 58.26) * mm, "radius": 1.5 * mm});
            skCircle(sketch, "E2.15.18.0", {"center": v(8.95, 68.26) * mm, "radius": 1.5 * mm});
            skCircle(sketch, "E2.15.19.0", {"center": v(8.95, 78.26) * mm, "radius": 1.5 * mm});
            skCircle(sketch, "E2.15.20.0", {"center": v(8.95, 88.26) * mm, "radius": 1.5 * mm});
            skCircle(sketch, "E2.15.21.0", {"center": v(8.95, 98.26) * mm, "radius": 1.5 * mm});
            skCircle(sketch, "E2.15.22.0", {"center": v(8.95, 108.26) * mm, "radius": 1.5 * mm});
            skCircle(sketch, "E2.15.23.0", {"center": v(8.95, 118.26) * mm, "radius": 1.5 * mm});
            skCircle(sketch, "E2.16.0.0", {"center": v(18.95, -111.74) * mm, "radius": 1.5 * mm});
            skCircle(sketch, "E2.16.1.0", {"center": v(18.95, -101.74) * mm, "radius": 1.5 * mm});
            skCircle(sketch, "E2.16.2.0", {"center": v(18.95, -91.74) * mm, "radius": 1.5 * mm});
            skCircle(sketch, "E2.16.3.0", {"center": v(18.95, -81.74) * mm, "radius": 1.5 * mm});
            skCircle(sketch, "E2.16.4.0", {"center": v(18.95, -71.74) * mm, "radius": 1.5 * mm});
            skCircle(sketch, "E2.16.5.0", {"center": v(18.95, -61.74) * mm, "radius": 1.5 * mm});
            skCircle(sketch, "E2.16.6.0", {"center": v(18.95, -51.74) * mm, "radius": 1.5 * mm});
            skCircle(sketch, "E2.16.7.0", {"center": v(18.95, -41.74) * mm, "radius": 1.5 * mm});
            skCircle(sketch, "E2.16.8.0", {"center": v(18.95, -31.74) * mm, "radius": 1.5 * mm});
            skCircle(sketch, "E2.16.9.0", {"center": v(18.95, -21.74) * mm, "radius": 1.5 * mm});
            skCircle(sketch, "E2.16.10.0", {"center": v(18.95, -11.74) * mm, "radius": 1.5 * mm});
            skCircle(sketch, "E2.16.11.0", {"center": v(18.95, -1.74) * mm, "radius": 1.5 * mm});
            skCircle(sketch, "E2.16.12.0", {"center": v(18.95, 8.26) * mm, "radius": 1.5 * mm});
            skCircle(sketch, "E2.16.13.0", {"center": v(18.95, 18.26) * mm, "radius": 1.5 * mm});
            skCircle(sketch, "E2.16.14.0", {"center": v(18.95, 28.26) * mm, "radius": 1.5 * mm});
            skCircle(sketch, "E2.16.15.0", {"center": v(18.95, 38.26) * mm, "radius": 1.5 * mm});
            skCircle(sketch, "E2.16.16.0", {"center": v(18.95, 48.26) * mm, "radius": 1.5 * mm});
            skCircle(sketch, "E2.16.17.0", {"center": v(18.95, 58.26) * mm, "radius": 1.5 * mm});
            skCircle(sketch, "E2.16.18.0", {"center": v(18.95, 68.26) * mm, "radius": 1.5 * mm});
            skCircle(sketch, "E2.16.19.0", {"center": v(18.95, 78.26) * mm, "radius": 1.5 * mm});
            skCircle(sketch, "E2.16.20.0", {"center": v(18.95, 88.26) * mm, "radius": 1.5 * mm});
            skCircle(sketch, "E2.16.21.0", {"center": v(18.95, 98.26) * mm, "radius": 1.5 * mm});
            skCircle(sketch, "E2.16.22.0", {"center": v(18.95, 108.26) * mm, "radius": 1.5 * mm});
            skCircle(sketch, "E2.16.23.0", {"center": v(18.95, 118.26) * mm, "radius": 1.5 * mm});
            skCircle(sketch, "E2.17.0.0", {"center": v(28.95, -111.74) * mm, "radius": 1.5 * mm});
            skCircle(sketch, "E2.17.1.0", {"center": v(28.95, -101.74) * mm, "radius": 1.5 * mm});
            skCircle(sketch, "E2.17.2.0", {"center": v(28.95, -91.74) * mm, "radius": 1.5 * mm});
            skCircle(sketch, "E2.17.3.0", {"center": v(28.95, -81.74) * mm, "radius": 1.5 * mm});
            skCircle(sketch, "E2.17.4.0", {"center": v(28.95, -71.74) * mm, "radius": 1.5 * mm});
            skCircle(sketch, "E2.17.5.0", {"center": v(28.95, -61.74) * mm, "radius": 1.5 * mm});
            skCircle(sketch, "E2.17.6.0", {"center": v(28.95, -51.74) * mm, "radius": 1.5 * mm});
            skCircle(sketch, "E2.17.7.0", {"center": v(28.95, -41.74) * mm, "radius": 1.5 * mm});
            skCircle(sketch, "E2.17.8.0", {"center": v(28.95, -31.74) * mm, "radius": 1.5 * mm});
            skCircle(sketch, "E2.17.9.0", {"center": v(28.95, -21.74) * mm, "radius": 1.5 * mm});
            skCircle(sketch, "E2.17.10.0", {"center": v(28.95, -11.74) * mm, "radius": 1.5 * mm});
            skCircle(sketch, "E2.17.11.0", {"center": v(28.95, -1.74) * mm, "radius": 1.5 * mm});
            skCircle(sketch, "E2.17.12.0", {"center": v(28.95, 8.26) * mm, "radius": 1.5 * mm});
            skCircle(sketch, "E2.17.13.0", {"center": v(28.95, 18.26) * mm, "radius": 1.5 * mm});
            skCircle(sketch, "E2.17.14.0", {"center": v(28.95, 28.26) * mm, "radius": 1.5 * mm});
            skCircle(sketch, "E2.17.15.0", {"center": v(28.95, 38.26) * mm, "radius": 1.5 * mm});
            skCircle(sketch, "E2.17.16.0", {"center": v(28.95, 48.26) * mm, "radius": 1.5 * mm});
            skCircle(sketch, "E2.17.17.0", {"center": v(28.95, 58.26) * mm, "radius": 1.5 * mm});
            skCircle(sketch, "E2.17.18.0", {"center": v(28.95, 68.26) * mm, "radius": 1.5 * mm});
            skCircle(sketch, "E2.17.19.0", {"center": v(28.95, 78.26) * mm, "radius": 1.5 * mm});
            skCircle(sketch, "E2.17.20.0", {"center": v(28.95, 88.26) * mm, "radius": 1.5 * mm});
            skCircle(sketch, "E2.17.21.0", {"center": v(28.95, 98.26) * mm, "radius": 1.5 * mm});
            skCircle(sketch, "E2.17.22.0", {"center": v(28.95, 108.26) * mm, "radius": 1.5 * mm});
            skCircle(sketch, "E2.17.23.0", {"center": v(28.95, 118.26) * mm, "radius": 1.5 * mm});
            skCircle(sketch, "E2.18.0.0", {"center": v(38.95, -111.74) * mm, "radius": 1.5 * mm});
            skCircle(sketch, "E2.18.1.0", {"center": v(38.95, -101.74) * mm, "radius": 1.5 * mm});
            skCircle(sketch, "E2.18.2.0", {"center": v(38.95, -91.74) * mm, "radius": 1.5 * mm});
            skCircle(sketch, "E2.18.3.0", {"center": v(38.95, -81.74) * mm, "radius": 1.5 * mm});
            skCircle(sketch, "E2.18.4.0", {"center": v(38.95, -71.74) * mm, "radius": 1.5 * mm});
            skCircle(sketch, "E2.18.5.0", {"center": v(38.95, -61.74) * mm, "radius": 1.5 * mm});
            skCircle(sketch, "E2.18.6.0", {"center": v(38.95, -51.74) * mm, "radius": 1.5 * mm});
            skCircle(sketch, "E2.18.7.0", {"center": v(38.95, -41.74) * mm, "radius": 1.5 * mm});
            skCircle(sketch, "E2.18.8.0", {"center": v(38.95, -31.74) * mm, "radius": 1.5 * mm});
            skCircle(sketch, "E2.18.9.0", {"center": v(38.95, -21.74) * mm, "radius": 1.5 * mm});
            skCircle(sketch, "E2.18.10.0", {"center": v(38.95, -11.74) * mm, "radius": 1.5 * mm});
            skCircle(sketch, "E2.18.11.0", {"center": v(38.95, -1.74) * mm, "radius": 1.5 * mm});
            skCircle(sketch, "E2.18.12.0", {"center": v(38.95, 8.26) * mm, "radius": 1.5 * mm});
            skCircle(sketch, "E2.18.13.0", {"center": v(38.95, 18.26) * mm, "radius": 1.5 * mm});
            skCircle(sketch, "E2.18.14.0", {"center": v(38.95, 28.26) * mm, "radius": 1.5 * mm});
            skCircle(sketch, "E2.18.15.0", {"center": v(38.95, 38.26) * mm, "radius": 1.5 * mm});
            skCircle(sketch, "E2.18.16.0", {"center": v(38.95, 48.26) * mm, "radius": 1.5 * mm});
            skCircle(sketch, "E2.18.17.0", {"center": v(38.95, 58.26) * mm, "radius": 1.5 * mm});
            skCircle(sketch, "E2.18.18.0", {"center": v(38.95, 68.26) * mm, "radius": 1.5 * mm});
            skCircle(sketch, "E2.18.19.0", {"center": v(38.95, 78.26) * mm, "radius": 1.5 * mm});
            skCircle(sketch, "E2.18.20.0", {"center": v(38.95, 88.26) * mm, "radius": 1.5 * mm});
            skCircle(sketch, "E2.18.21.0", {"center": v(38.95, 98.26) * mm, "radius": 1.5 * mm});
            skCircle(sketch, "E2.18.22.0", {"center": v(38.95, 108.26) * mm, "radius": 1.5 * mm});
            skCircle(sketch, "E2.18.23.0", {"center": v(38.95, 118.26) * mm, "radius": 1.5 * mm});
            skCircle(sketch, "E2.19.0.0", {"center": v(48.95, -111.74) * mm, "radius": 1.5 * mm});
            skCircle(sketch, "E2.19.1.0", {"center": v(48.95, -101.74) * mm, "radius": 1.5 * mm});
            skCircle(sketch, "E2.19.2.0", {"center": v(48.95, -91.74) * mm, "radius": 1.5 * mm});
            skCircle(sketch, "E2.19.3.0", {"center": v(48.95, -81.74) * mm, "radius": 1.5 * mm});
            skCircle(sketch, "E2.19.4.0", {"center": v(48.95, -71.74) * mm, "radius": 1.5 * mm});
            skCircle(sketch, "E2.19.5.0", {"center": v(48.95, -61.74) * mm, "radius": 1.5 * mm});
            skCircle(sketch, "E2.19.6.0", {"center": v(48.95, -51.74) * mm, "radius": 1.5 * mm});
            skCircle(sketch, "E2.19.7.0", {"center": v(48.95, -41.74) * mm, "radius": 1.5 * mm});
            skCircle(sketch, "E2.19.8.0", {"center": v(48.95, -31.74) * mm, "radius": 1.5 * mm});
            skCircle(sketch, "E2.19.9.0", {"center": v(48.95, -21.74) * mm, "radius": 1.5 * mm});
            skCircle(sketch, "E2.19.10.0", {"center": v(48.95, -11.74) * mm, "radius": 1.5 * mm});
            skCircle(sketch, "E2.19.11.0", {"center": v(48.95, -1.74) * mm, "radius": 1.5 * mm});
            skCircle(sketch, "E2.19.12.0", {"center": v(48.95, 8.26) * mm, "radius": 1.5 * mm});
            skCircle(sketch, "E2.19.13.0", {"center": v(48.95, 18.26) * mm, "radius": 1.5 * mm});
            skCircle(sketch, "E2.19.14.0", {"center": v(48.95, 28.26) * mm, "radius": 1.5 * mm});
            skCircle(sketch, "E2.19.15.0", {"center": v(48.95, 38.26) * mm, "radius": 1.5 * mm});
            skCircle(sketch, "E2.19.16.0", {"center": v(48.95, 48.26) * mm, "radius": 1.5 * mm});
            skCircle(sketch, "E2.19.17.0", {"center": v(48.95, 58.26) * mm, "radius": 1.5 * mm});
            skCircle(sketch, "E2.19.18.0", {"center": v(48.95, 68.26) * mm, "radius": 1.5 * mm});
            skCircle(sketch, "E2.19.19.0", {"center": v(48.95, 78.26) * mm, "radius": 1.5 * mm});
            skCircle(sketch, "E2.19.20.0", {"center": v(48.95, 88.26) * mm, "radius": 1.5 * mm});
            skCircle(sketch, "E2.19.21.0", {"center": v(48.95, 98.26) * mm, "radius": 1.5 * mm});
            skCircle(sketch, "E2.19.22.0", {"center": v(48.95, 108.26) * mm, "radius": 1.5 * mm});
            skCircle(sketch, "E2.19.23.0", {"center": v(48.95, 118.26) * mm, "radius": 1.5 * mm});
            skCircle(sketch, "E2.20.0.0", {"center": v(58.95, -111.74) * mm, "radius": 1.5 * mm});
            skCircle(sketch, "E2.20.1.0", {"center": v(58.95, -101.74) * mm, "radius": 1.5 * mm});
            skCircle(sketch, "E2.20.2.0", {"center": v(58.95, -91.74) * mm, "radius": 1.5 * mm});
            skCircle(sketch, "E2.20.3.0", {"center": v(58.95, -81.74) * mm, "radius": 1.5 * mm});
            skCircle(sketch, "E2.20.4.0", {"center": v(58.95, -71.74) * mm, "radius": 1.5 * mm});
            skCircle(sketch, "E2.20.5.0", {"center": v(58.95, -61.74) * mm, "radius": 1.5 * mm});
            skCircle(sketch, "E2.20.6.0", {"center": v(58.95, -51.74) * mm, "radius": 1.5 * mm});
            skCircle(sketch, "E2.20.7.0", {"center": v(58.95, -41.74) * mm, "radius": 1.5 * mm});
            skCircle(sketch, "E2.20.8.0", {"center": v(58.95, -31.74) * mm, "radius": 1.5 * mm});
            skCircle(sketch, "E2.20.9.0", {"center": v(58.95, -21.74) * mm, "radius": 1.5 * mm});
            skCircle(sketch, "E2.20.10.0", {"center": v(58.95, -11.74) * mm, "radius": 1.5 * mm});
            skCircle(sketch, "E2.20.11.0", {"center": v(58.95, -1.74) * mm, "radius": 1.5 * mm});
            skCircle(sketch, "E2.20.12.0", {"center": v(58.95, 8.26) * mm, "radius": 1.5 * mm});
            skCircle(sketch, "E2.20.13.0", {"center": v(58.95, 18.26) * mm, "radius": 1.5 * mm});
            skCircle(sketch, "E2.20.14.0", {"center": v(58.95, 28.26) * mm, "radius": 1.5 * mm});
            skCircle(sketch, "E2.20.15.0", {"center": v(58.95, 38.26) * mm, "radius": 1.5 * mm});
            skCircle(sketch, "E2.20.16.0", {"center": v(58.95, 48.26) * mm, "radius": 1.5 * mm});
            skCircle(sketch, "E2.20.17.0", {"center": v(58.95, 58.26) * mm, "radius": 1.5 * mm});
            skCircle(sketch, "E2.20.18.0", {"center": v(58.95, 68.26) * mm, "radius": 1.5 * mm});
            skCircle(sketch, "E2.20.19.0", {"center": v(58.95, 78.26) * mm, "radius": 1.5 * mm});
            skCircle(sketch, "E2.20.20.0", {"center": v(58.95, 88.26) * mm, "radius": 1.5 * mm});
            skCircle(sketch, "E2.20.21.0", {"center": v(58.95, 98.26) * mm, "radius": 1.5 * mm});
            skCircle(sketch, "E2.20.22.0", {"center": v(58.95, 108.26) * mm, "radius": 1.5 * mm});
            skCircle(sketch, "E2.20.23.0", {"center": v(58.95, 118.26) * mm, "radius": 1.5 * mm});
            skCircle(sketch, "E2.21.0.0", {"center": v(68.95, -111.74) * mm, "radius": 1.5 * mm});
            skCircle(sketch, "E2.21.1.0", {"center": v(68.95, -101.74) * mm, "radius": 1.5 * mm});
            skCircle(sketch, "E2.21.2.0", {"center": v(68.95, -91.74) * mm, "radius": 1.5 * mm});
            skCircle(sketch, "E2.21.3.0", {"center": v(68.95, -81.74) * mm, "radius": 1.5 * mm});
            skCircle(sketch, "E2.21.4.0", {"center": v(68.95, -71.74) * mm, "radius": 1.5 * mm});
            skCircle(sketch, "E2.21.5.0", {"center": v(68.95, -61.74) * mm, "radius": 1.5 * mm});
            skCircle(sketch, "E2.21.6.0", {"center": v(68.95, -51.74) * mm, "radius": 1.5 * mm});
            skCircle(sketch, "E2.21.7.0", {"center": v(68.95, -41.74) * mm, "radius": 1.5 * mm});
            skCircle(sketch, "E2.21.8.0", {"center": v(68.95, -31.74) * mm, "radius": 1.5 * mm});
            skCircle(sketch, "E2.21.9.0", {"center": v(68.95, -21.74) * mm, "radius": 1.5 * mm});
            skCircle(sketch, "E2.21.10.0", {"center": v(68.95, -11.74) * mm, "radius": 1.5 * mm});
            skCircle(sketch, "E2.21.11.0", {"center": v(68.95, -1.74) * mm, "radius": 1.5 * mm});
            skCircle(sketch, "E2.21.12.0", {"center": v(68.95, 8.26) * mm, "radius": 1.5 * mm});
            skCircle(sketch, "E2.21.13.0", {"center": v(68.95, 18.26) * mm, "radius": 1.5 * mm});
            skCircle(sketch, "E2.21.14.0", {"center": v(68.95, 28.26) * mm, "radius": 1.5 * mm});
            skCircle(sketch, "E2.21.15.0", {"center": v(68.95, 38.26) * mm, "radius": 1.5 * mm});
            skCircle(sketch, "E2.21.16.0", {"center": v(68.95, 48.26) * mm, "radius": 1.5 * mm});
            skCircle(sketch, "E2.21.17.0", {"center": v(68.95, 58.26) * mm, "radius": 1.5 * mm});
            skCircle(sketch, "E2.21.18.0", {"center": v(68.95, 68.26) * mm, "radius": 1.5 * mm});
            skCircle(sketch, "E2.21.19.0", {"center": v(68.95, 78.26) * mm, "radius": 1.5 * mm});
            skCircle(sketch, "E2.21.20.0", {"center": v(68.95, 88.26) * mm, "radius": 1.5 * mm});
            skCircle(sketch, "E2.21.21.0", {"center": v(68.95, 98.26) * mm, "radius": 1.5 * mm});
            skCircle(sketch, "E2.21.22.0", {"center": v(68.95, 108.26) * mm, "radius": 1.5 * mm});
            skCircle(sketch, "E2.21.23.0", {"center": v(68.95, 118.26) * mm, "radius": 1.5 * mm});
            skCircle(sketch, "E2.22.0.0", {"center": v(78.95, -111.74) * mm, "radius": 1.5 * mm});
            skCircle(sketch, "E2.22.1.0", {"center": v(78.95, -101.74) * mm, "radius": 1.5 * mm});
            skCircle(sketch, "E2.22.2.0", {"center": v(78.95, -91.74) * mm, "radius": 1.5 * mm});
            skCircle(sketch, "E2.22.3.0", {"center": v(78.95, -81.74) * mm, "radius": 1.5 * mm});
            skCircle(sketch, "E2.22.4.0", {"center": v(78.95, -71.74) * mm, "radius": 1.5 * mm});
            skCircle(sketch, "E2.22.5.0", {"center": v(78.95, -61.74) * mm, "radius": 1.5 * mm});
            skCircle(sketch, "E2.22.6.0", {"center": v(78.95, -51.74) * mm, "radius": 1.5 * mm});
            skCircle(sketch, "E2.22.7.0", {"center": v(78.95, -41.74) * mm, "radius": 1.5 * mm});
            skCircle(sketch, "E2.22.8.0", {"center": v(78.95, -31.74) * mm, "radius": 1.5 * mm});
            skCircle(sketch, "E2.22.9.0", {"center": v(78.95, -21.74) * mm, "radius": 1.5 * mm});
            skCircle(sketch, "E2.22.10.0", {"center": v(78.95, -11.74) * mm, "radius": 1.5 * mm});
            skCircle(sketch, "E2.22.11.0", {"center": v(78.95, -1.74) * mm, "radius": 1.5 * mm});
            skCircle(sketch, "E2.22.12.0", {"center": v(78.95, 8.26) * mm, "radius": 1.5 * mm});
            skCircle(sketch, "E2.22.13.0", {"center": v(78.95, 18.26) * mm, "radius": 1.5 * mm});
            skCircle(sketch, "E2.22.14.0", {"center": v(78.95, 28.26) * mm, "radius": 1.5 * mm});
            skCircle(sketch, "E2.22.15.0", {"center": v(78.95, 38.26) * mm, "radius": 1.5 * mm});
            skCircle(sketch, "E2.22.16.0", {"center": v(78.95, 48.26) * mm, "radius": 1.5 * mm});
            skCircle(sketch, "E2.22.17.0", {"center": v(78.95, 58.26) * mm, "radius": 1.5 * mm});
            skCircle(sketch, "E2.22.18.0", {"center": v(78.95, 68.26) * mm, "radius": 1.5 * mm});
            skCircle(sketch, "E2.22.19.0", {"center": v(78.95, 78.26) * mm, "radius": 1.5 * mm});
            skCircle(sketch, "E2.22.20.0", {"center": v(78.95, 88.26) * mm, "radius": 1.5 * mm});
            skCircle(sketch, "E2.22.21.0", {"center": v(78.95, 98.26) * mm, "radius": 1.5 * mm});
            skCircle(sketch, "E2.22.22.0", {"center": v(78.95, 108.26) * mm, "radius": 1.5 * mm});
            skCircle(sketch, "E2.22.23.0", {"center": v(78.95, 118.26) * mm, "radius": 1.5 * mm});
            skCircle(sketch, "E2.23.0.0", {"center": v(88.95, -111.74) * mm, "radius": 1.5 * mm});
            skCircle(sketch, "E2.23.1.0", {"center": v(88.95, -101.74) * mm, "radius": 1.5 * mm});
            skCircle(sketch, "E2.23.2.0", {"center": v(88.95, -91.74) * mm, "radius": 1.5 * mm});
            skCircle(sketch, "E2.23.3.0", {"center": v(88.95, -81.74) * mm, "radius": 1.5 * mm});
            skCircle(sketch, "E2.23.4.0", {"center": v(88.95, -71.74) * mm, "radius": 1.5 * mm});
            skCircle(sketch, "E2.23.5.0", {"center": v(88.95, -61.74) * mm, "radius": 1.5 * mm});
            skCircle(sketch, "E2.23.6.0", {"center": v(88.95, -51.74) * mm, "radius": 1.5 * mm});
            skCircle(sketch, "E2.23.7.0", {"center": v(88.95, -41.74) * mm, "radius": 1.5 * mm});
            skCircle(sketch, "E2.23.8.0", {"center": v(88.95, -31.74) * mm, "radius": 1.5 * mm});
            skCircle(sketch, "E2.23.9.0", {"center": v(88.95, -21.74) * mm, "radius": 1.5 * mm});
            skCircle(sketch, "E2.23.10.0", {"center": v(88.95, -11.74) * mm, "radius": 1.5 * mm});
            skCircle(sketch, "E2.23.11.0", {"center": v(88.95, -1.74) * mm, "radius": 1.5 * mm});
            skCircle(sketch, "E2.23.12.0", {"center": v(88.95, 8.26) * mm, "radius": 1.5 * mm});
            skCircle(sketch, "E2.23.13.0", {"center": v(88.95, 18.26) * mm, "radius": 1.5 * mm});
            skCircle(sketch, "E2.23.14.0", {"center": v(88.95, 28.26) * mm, "radius": 1.5 * mm});
            skCircle(sketch, "E2.23.15.0", {"center": v(88.95, 38.26) * mm, "radius": 1.5 * mm});
            skCircle(sketch, "E2.23.16.0", {"center": v(88.95, 48.26) * mm, "radius": 1.5 * mm});
            skCircle(sketch, "E2.23.17.0", {"center": v(88.95, 58.26) * mm, "radius": 1.5 * mm});
            skCircle(sketch, "E2.23.18.0", {"center": v(88.95, 68.26) * mm, "radius": 1.5 * mm});
            skCircle(sketch, "E2.23.19.0", {"center": v(88.95, 78.26) * mm, "radius": 1.5 * mm});
            skCircle(sketch, "E2.23.20.0", {"center": v(88.95, 88.26) * mm, "radius": 1.5 * mm});
            skCircle(sketch, "E2.23.21.0", {"center": v(88.95, 98.26) * mm, "radius": 1.5 * mm});
            skCircle(sketch, "E2.23.22.0", {"center": v(88.95, 108.26) * mm, "radius": 1.5 * mm});
            skCircle(sketch, "E2.23.23.0", {"center": v(88.95, 118.26) * mm, "radius": 1.5 * mm});
            skCircle(sketch, "E2.24.0.0", {"center": v(98.95, -111.74) * mm, "radius": 1.5 * mm});
            skCircle(sketch, "E2.24.1.0", {"center": v(98.95, -101.74) * mm, "radius": 1.5 * mm});
            skCircle(sketch, "E2.24.2.0", {"center": v(98.95, -91.74) * mm, "radius": 1.5 * mm});
            skCircle(sketch, "E2.24.3.0", {"center": v(98.95, -81.74) * mm, "radius": 1.5 * mm});
            skCircle(sketch, "E2.24.4.0", {"center": v(98.95, -71.74) * mm, "radius": 1.5 * mm});
            skCircle(sketch, "E2.24.5.0", {"center": v(98.95, -61.74) * mm, "radius": 1.5 * mm});
            skCircle(sketch, "E2.24.6.0", {"center": v(98.95, -51.74) * mm, "radius": 1.5 * mm});
            skCircle(sketch, "E2.24.7.0", {"center": v(98.95, -41.74) * mm, "radius": 1.5 * mm});
            skCircle(sketch, "E2.24.8.0", {"center": v(98.95, -31.74) * mm, "radius": 1.5 * mm});
            skCircle(sketch, "E2.24.9.0", {"center": v(98.95, -21.74) * mm, "radius": 1.5 * mm});
            skCircle(sketch, "E2.24.10.0", {"center": v(98.95, -11.74) * mm, "radius": 1.5 * mm});
            skCircle(sketch, "E2.24.11.0", {"center": v(98.95, -1.74) * mm, "radius": 1.5 * mm});
            skCircle(sketch, "E2.24.12.0", {"center": v(98.95, 8.26) * mm, "radius": 1.5 * mm});
            skCircle(sketch, "E2.24.13.0", {"center": v(98.95, 18.26) * mm, "radius": 1.5 * mm});
            skCircle(sketch, "E2.24.14.0", {"center": v(98.95, 28.26) * mm, "radius": 1.5 * mm});
            skCircle(sketch, "E2.24.15.0", {"center": v(98.95, 38.26) * mm, "radius": 1.5 * mm});
            skCircle(sketch, "E2.24.16.0", {"center": v(98.95, 48.26) * mm, "radius": 1.5 * mm});
            skCircle(sketch, "E2.24.17.0", {"center": v(98.95, 58.26) * mm, "radius": 1.5 * mm});
            skCircle(sketch, "E2.24.18.0", {"center": v(98.95, 68.26) * mm, "radius": 1.5 * mm});
            skCircle(sketch, "E2.24.19.0", {"center": v(98.95, 78.26) * mm, "radius": 1.5 * mm});
            skCircle(sketch, "E2.24.20.0", {"center": v(98.95, 88.26) * mm, "radius": 1.5 * mm});
            skCircle(sketch, "E2.24.21.0", {"center": v(98.95, 98.26) * mm, "radius": 1.5 * mm});
            skCircle(sketch, "E2.24.22.0", {"center": v(98.95, 108.26) * mm, "radius": 1.5 * mm});
            skCircle(sketch, "E2.24.23.0", {"center": v(98.95, 118.26) * mm, "radius": 1.5 * mm});
            skCircle(sketch, "E2.25.0.0", {"center": v(108.95, -111.74) * mm, "radius": 1.5 * mm});
            skCircle(sketch, "E2.25.1.0", {"center": v(108.95, -101.74) * mm, "radius": 1.5 * mm});
            skCircle(sketch, "E2.25.2.0", {"center": v(108.95, -91.74) * mm, "radius": 1.5 * mm});
            skCircle(sketch, "E2.25.3.0", {"center": v(108.95, -81.74) * mm, "radius": 1.5 * mm});
            skCircle(sketch, "E2.25.4.0", {"center": v(108.95, -71.74) * mm, "radius": 1.5 * mm});
            skCircle(sketch, "E2.25.5.0", {"center": v(108.95, -61.74) * mm, "radius": 1.5 * mm});
            skCircle(sketch, "E2.25.6.0", {"center": v(108.95, -51.74) * mm, "radius": 1.5 * mm});
            skCircle(sketch, "E2.25.7.0", {"center": v(108.95, -41.74) * mm, "radius": 1.5 * mm});
            skCircle(sketch, "E2.25.8.0", {"center": v(108.95, -31.74) * mm, "radius": 1.5 * mm});
            skCircle(sketch, "E2.25.9.0", {"center": v(108.95, -21.74) * mm, "radius": 1.5 * mm});
            skCircle(sketch, "E2.25.10.0", {"center": v(108.95, -11.74) * mm, "radius": 1.5 * mm});
            skCircle(sketch, "E2.25.11.0", {"center": v(108.95, -1.74) * mm, "radius": 1.5 * mm});
            skCircle(sketch, "E2.25.12.0", {"center": v(108.95, 8.26) * mm, "radius": 1.5 * mm});
            skCircle(sketch, "E2.25.13.0", {"center": v(108.95, 18.26) * mm, "radius": 1.5 * mm});
            skCircle(sketch, "E2.25.14.0", {"center": v(108.95, 28.26) * mm, "radius": 1.5 * mm});
            skCircle(sketch, "E2.25.15.0", {"center": v(108.95, 38.26) * mm, "radius": 1.5 * mm});
            skCircle(sketch, "E2.25.16.0", {"center": v(108.95, 48.26) * mm, "radius": 1.5 * mm});
            skCircle(sketch, "E2.25.17.0", {"center": v(108.95, 58.26) * mm, "radius": 1.5 * mm});
            skCircle(sketch, "E2.25.18.0", {"center": v(108.95, 68.26) * mm, "radius": 1.5 * mm});
            skCircle(sketch, "E2.25.19.0", {"center": v(108.95, 78.26) * mm, "radius": 1.5 * mm});
            skCircle(sketch, "E2.25.20.0", {"center": v(108.95, 88.26) * mm, "radius": 1.5 * mm});
            skCircle(sketch, "E2.25.21.0", {"center": v(108.95, 98.26) * mm, "radius": 1.5 * mm});
            skCircle(sketch, "E2.25.22.0", {"center": v(108.95, 108.26) * mm, "radius": 1.5 * mm});
            skCircle(sketch, "E2.25.23.0", {"center": v(108.95, 118.26) * mm, "radius": 1.5 * mm});
            skCircle(sketch, "E2.26.0.0", {"center": v(118.95, -111.74) * mm, "radius": 1.5 * mm});
            skCircle(sketch, "E2.26.1.0", {"center": v(118.95, -101.74) * mm, "radius": 1.5 * mm});
            skCircle(sketch, "E2.26.2.0", {"center": v(118.95, -91.74) * mm, "radius": 1.5 * mm});
            skCircle(sketch, "E2.26.3.0", {"center": v(118.95, -81.74) * mm, "radius": 1.5 * mm});
            skCircle(sketch, "E2.26.4.0", {"center": v(118.95, -71.74) * mm, "radius": 1.5 * mm});
            skCircle(sketch, "E2.26.5.0", {"center": v(118.95, -61.74) * mm, "radius": 1.5 * mm});
            skCircle(sketch, "E2.26.6.0", {"center": v(118.95, -51.74) * mm, "radius": 1.5 * mm});
            skCircle(sketch, "E2.26.7.0", {"center": v(118.95, -41.74) * mm, "radius": 1.5 * mm});
            skCircle(sketch, "E2.26.8.0", {"center": v(118.95, -31.74) * mm, "radius": 1.5 * mm});
            skCircle(sketch, "E2.26.9.0", {"center": v(118.95, -21.74) * mm, "radius": 1.5 * mm});
            skCircle(sketch, "E2.26.10.0", {"center": v(118.95, -11.74) * mm, "radius": 1.5 * mm});
            skCircle(sketch, "E2.26.11.0", {"center": v(118.95, -1.74) * mm, "radius": 1.5 * mm});
            skCircle(sketch, "E2.26.12.0", {"center": v(118.95, 8.26) * mm, "radius": 1.5 * mm});
            skCircle(sketch, "E2.26.13.0", {"center": v(118.95, 18.26) * mm, "radius": 1.5 * mm});
            skCircle(sketch, "E2.26.14.0", {"center": v(118.95, 28.26) * mm, "radius": 1.5 * mm});
            skCircle(sketch, "E2.26.15.0", {"center": v(118.95, 38.26) * mm, "radius": 1.5 * mm});
            skCircle(sketch, "E2.26.16.0", {"center": v(118.95, 48.26) * mm, "radius": 1.5 * mm});
            skCircle(sketch, "E2.26.17.0", {"center": v(118.95, 58.26) * mm, "radius": 1.5 * mm});
            skCircle(sketch, "E2.26.18.0", {"center": v(118.95, 68.26) * mm, "radius": 1.5 * mm});
            skCircle(sketch, "E2.26.19.0", {"center": v(118.95, 78.26) * mm, "radius": 1.5 * mm});
            skCircle(sketch, "E2.26.20.0", {"center": v(118.95, 88.26) * mm, "radius": 1.5 * mm});
            skCircle(sketch, "E2.26.21.0", {"center": v(118.95, 98.26) * mm, "radius": 1.5 * mm});
            skCircle(sketch, "E2.26.22.0", {"center": v(118.95, 108.26) * mm, "radius": 1.5 * mm});
            skCircle(sketch, "E2.26.23.0", {"center": v(118.95, 118.26) * mm, "radius": 1.5 * mm});
            skCircle(sketch, "E2.27.0.0", {"center": v(128.95, -111.74) * mm, "radius": 1.5 * mm});
            skCircle(sketch, "E2.27.1.0", {"center": v(128.95, -101.74) * mm, "radius": 1.5 * mm});
            skCircle(sketch, "E2.27.2.0", {"center": v(128.95, -91.74) * mm, "radius": 1.5 * mm});
            skCircle(sketch, "E2.27.3.0", {"center": v(128.95, -81.74) * mm, "radius": 1.5 * mm});
            skCircle(sketch, "E2.27.4.0", {"center": v(128.95, -71.74) * mm, "radius": 1.5 * mm});
            skCircle(sketch, "E2.27.5.0", {"center": v(128.95, -61.74) * mm, "radius": 1.5 * mm});
            skCircle(sketch, "E2.27.6.0", {"center": v(128.95, -51.74) * mm, "radius": 1.5 * mm});
            skCircle(sketch, "E2.27.7.0", {"center": v(128.95, -41.74) * mm, "radius": 1.5 * mm});
            skCircle(sketch, "E2.27.8.0", {"center": v(128.95, -31.74) * mm, "radius": 1.5 * mm});
            skCircle(sketch, "E2.27.9.0", {"center": v(128.95, -21.74) * mm, "radius": 1.5 * mm});
            skCircle(sketch, "E2.27.10.0", {"center": v(128.95, -11.74) * mm, "radius": 1.5 * mm});
            skCircle(sketch, "E2.27.11.0", {"center": v(128.95, -1.74) * mm, "radius": 1.5 * mm});
            skCircle(sketch, "E2.27.12.0", {"center": v(128.95, 8.26) * mm, "radius": 1.5 * mm});
            skCircle(sketch, "E2.27.13.0", {"center": v(128.95, 18.26) * mm, "radius": 1.5 * mm});
            skCircle(sketch, "E2.27.14.0", {"center": v(128.95, 28.26) * mm, "radius": 1.5 * mm});
            skCircle(sketch, "E2.27.15.0", {"center": v(128.95, 38.26) * mm, "radius": 1.5 * mm});
            skCircle(sketch, "E2.27.16.0", {"center": v(128.95, 48.26) * mm, "radius": 1.5 * mm});
            skCircle(sketch, "E2.27.17.0", {"center": v(128.95, 58.26) * mm, "radius": 1.5 * mm});
            skCircle(sketch, "E2.27.18.0", {"center": v(128.95, 68.26) * mm, "radius": 1.5 * mm});
            skCircle(sketch, "E2.27.19.0", {"center": v(128.95, 78.26) * mm, "radius": 1.5 * mm});
            skCircle(sketch, "E2.27.20.0", {"center": v(128.95, 88.26) * mm, "radius": 1.5 * mm});
            skCircle(sketch, "E2.27.21.0", {"center": v(128.95, 98.26) * mm, "radius": 1.5 * mm});
            skCircle(sketch, "E2.27.22.0", {"center": v(128.95, 108.26) * mm, "radius": 1.5 * mm});
            skCircle(sketch, "E2.27.23.0", {"center": v(128.95, 118.26) * mm, "radius": 1.5 * mm});
            skCircle(sketch, "E2.28.0.0", {"center": v(138.95, -111.74) * mm, "radius": 1.5 * mm});
            skCircle(sketch, "E2.28.1.0", {"center": v(138.95, -101.74) * mm, "radius": 1.5 * mm});
            skCircle(sketch, "E2.28.2.0", {"center": v(138.95, -91.74) * mm, "radius": 1.5 * mm});
            skCircle(sketch, "E2.28.3.0", {"center": v(138.95, -81.74) * mm, "radius": 1.5 * mm});
            skCircle(sketch, "E2.28.4.0", {"center": v(138.95, -71.74) * mm, "radius": 1.5 * mm});
            skCircle(sketch, "E2.28.5.0", {"center": v(138.95, -61.74) * mm, "radius": 1.5 * mm});
            skCircle(sketch, "E2.28.6.0", {"center": v(138.95, -51.74) * mm, "radius": 1.5 * mm});
            skCircle(sketch, "E2.28.7.0", {"center": v(138.95, -41.74) * mm, "radius": 1.5 * mm});
            skCircle(sketch, "E2.28.8.0", {"center": v(138.95, -31.74) * mm, "radius": 1.5 * mm});
            skCircle(sketch, "E2.28.9.0", {"center": v(138.95, -21.74) * mm, "radius": 1.5 * mm});
            skCircle(sketch, "E2.28.10.0", {"center": v(138.95, -11.74) * mm, "radius": 1.5 * mm});
            skCircle(sketch, "E2.28.11.0", {"center": v(138.95, -1.74) * mm, "radius": 1.5 * mm});
            skCircle(sketch, "E2.28.12.0", {"center": v(138.95, 8.26) * mm, "radius": 1.5 * mm});
            skCircle(sketch, "E2.28.13.0", {"center": v(138.95, 18.26) * mm, "radius": 1.5 * mm});
            skCircle(sketch, "E2.28.14.0", {"center": v(138.95, 28.26) * mm, "radius": 1.5 * mm});
            skCircle(sketch, "E2.28.15.0", {"center": v(138.95, 38.26) * mm, "radius": 1.5 * mm});
            skCircle(sketch, "E2.28.16.0", {"center": v(138.95, 48.26) * mm, "radius": 1.5 * mm});
            skCircle(sketch, "E2.28.17.0", {"center": v(138.95, 58.26) * mm, "radius": 1.5 * mm});
            skCircle(sketch, "E2.28.18.0", {"center": v(138.95, 68.26) * mm, "radius": 1.5 * mm});
            skCircle(sketch, "E2.28.19.0", {"center": v(138.95, 78.26) * mm, "radius": 1.5 * mm});
            skCircle(sketch, "E2.28.20.0", {"center": v(138.95, 88.26) * mm, "radius": 1.5 * mm});
            skCircle(sketch, "E2.28.21.0", {"center": v(138.95, 98.26) * mm, "radius": 1.5 * mm});
            skCircle(sketch, "E2.28.22.0", {"center": v(138.95, 108.26) * mm, "radius": 1.5 * mm});
            skCircle(sketch, "E2.28.23.0", {"center": v(138.95, 118.26) * mm, "radius": 1.5 * mm});
            skCircle(sketch, "E2.29.0.0", {"center": v(148.95, -111.74) * mm, "radius": 1.5 * mm});
            skCircle(sketch, "E2.29.1.0", {"center": v(148.95, -101.74) * mm, "radius": 1.5 * mm});
            skCircle(sketch, "E2.29.2.0", {"center": v(148.95, -91.74) * mm, "radius": 1.5 * mm});
            skCircle(sketch, "E2.29.3.0", {"center": v(148.95, -81.74) * mm, "radius": 1.5 * mm});
            skCircle(sketch, "E2.29.4.0", {"center": v(148.95, -71.74) * mm, "radius": 1.5 * mm});
            skCircle(sketch, "E2.29.5.0", {"center": v(148.95, -61.74) * mm, "radius": 1.5 * mm});
            skCircle(sketch, "E2.29.6.0", {"center": v(148.95, -51.74) * mm, "radius": 1.5 * mm});
            skCircle(sketch, "E2.29.7.0", {"center": v(148.95, -41.74) * mm, "radius": 1.5 * mm});
            skCircle(sketch, "E2.29.8.0", {"center": v(148.95, -31.74) * mm, "radius": 1.5 * mm});
            skCircle(sketch, "E2.29.9.0", {"center": v(148.95, -21.74) * mm, "radius": 1.5 * mm});
            skCircle(sketch, "E2.29.10.0", {"center": v(148.95, -11.74) * mm, "radius": 1.5 * mm});
            skCircle(sketch, "E2.29.11.0", {"center": v(148.95, -1.74) * mm, "radius": 1.5 * mm});
            skCircle(sketch, "E2.29.12.0", {"center": v(148.95, 8.26) * mm, "radius": 1.5 * mm});
            skCircle(sketch, "E2.29.13.0", {"center": v(148.95, 18.26) * mm, "radius": 1.5 * mm});
            skCircle(sketch, "E2.29.14.0", {"center": v(148.95, 28.26) * mm, "radius": 1.5 * mm});
            skCircle(sketch, "E2.29.15.0", {"center": v(148.95, 38.26) * mm, "radius": 1.5 * mm});
            skCircle(sketch, "E2.29.16.0", {"center": v(148.95, 48.26) * mm, "radius": 1.5 * mm});
            skCircle(sketch, "E2.29.17.0", {"center": v(148.95, 58.26) * mm, "radius": 1.5 * mm});
            skCircle(sketch, "E2.29.18.0", {"center": v(148.95, 68.26) * mm, "radius": 1.5 * mm});
            skCircle(sketch, "E2.29.19.0", {"center": v(148.95, 78.26) * mm, "radius": 1.5 * mm});
            skCircle(sketch, "E2.29.20.0", {"center": v(148.95, 88.26) * mm, "radius": 1.5 * mm});
            skCircle(sketch, "E2.29.21.0", {"center": v(148.95, 98.26) * mm, "radius": 1.5 * mm});
            skCircle(sketch, "E2.29.22.0", {"center": v(148.95, 108.26) * mm, "radius": 1.5 * mm});
            skCircle(sketch, "E2.29.23.0", {"center": v(148.95, 118.26) * mm, "radius": 1.5 * mm});
            skCircle(sketch, "E2.30.0.0", {"center": v(158.95, -111.74) * mm, "radius": 1.5 * mm});
            skCircle(sketch, "E2.30.1.0", {"center": v(158.95, -101.74) * mm, "radius": 1.5 * mm});
            skCircle(sketch, "E2.30.2.0", {"center": v(158.95, -91.74) * mm, "radius": 1.5 * mm});
            skCircle(sketch, "E2.30.3.0", {"center": v(158.95, -81.74) * mm, "radius": 1.5 * mm});
            skCircle(sketch, "E2.30.4.0", {"center": v(158.95, -71.74) * mm, "radius": 1.5 * mm});
            skCircle(sketch, "E2.30.5.0", {"center": v(158.95, -61.74) * mm, "radius": 1.5 * mm});
            skCircle(sketch, "E2.30.6.0", {"center": v(158.95, -51.74) * mm, "radius": 1.5 * mm});
            skCircle(sketch, "E2.30.7.0", {"center": v(158.95, -41.74) * mm, "radius": 1.5 * mm});
            skCircle(sketch, "E2.30.8.0", {"center": v(158.95, -31.74) * mm, "radius": 1.5 * mm});
            skCircle(sketch, "E2.30.9.0", {"center": v(158.95, -21.74) * mm, "radius": 1.5 * mm});
            skCircle(sketch, "E2.30.10.0", {"center": v(158.95, -11.74) * mm, "radius": 1.5 * mm});
            skCircle(sketch, "E2.30.11.0", {"center": v(158.95, -1.74) * mm, "radius": 1.5 * mm});
            skCircle(sketch, "E2.30.12.0", {"center": v(158.95, 8.26) * mm, "radius": 1.5 * mm});
            skCircle(sketch, "E2.30.13.0", {"center": v(158.95, 18.26) * mm, "radius": 1.5 * mm});
            skCircle(sketch, "E2.30.14.0", {"center": v(158.95, 28.26) * mm, "radius": 1.5 * mm});
            skCircle(sketch, "E2.30.15.0", {"center": v(158.95, 38.26) * mm, "radius": 1.5 * mm});
            skCircle(sketch, "E2.30.16.0", {"center": v(158.95, 48.26) * mm, "radius": 1.5 * mm});
            skCircle(sketch, "E2.30.17.0", {"center": v(158.95, 58.26) * mm, "radius": 1.5 * mm});
            skCircle(sketch, "E2.30.18.0", {"center": v(158.95, 68.26) * mm, "radius": 1.5 * mm});
            skCircle(sketch, "E2.30.19.0", {"center": v(158.95, 78.26) * mm, "radius": 1.5 * mm});
            skCircle(sketch, "E2.30.20.0", {"center": v(158.95, 88.26) * mm, "radius": 1.5 * mm});
            skCircle(sketch, "E2.30.21.0", {"center": v(158.95, 98.26) * mm, "radius": 1.5 * mm});
            skCircle(sketch, "E2.30.22.0", {"center": v(158.95, 108.26) * mm, "radius": 1.5 * mm});
            skCircle(sketch, "E2.30.23.0", {"center": v(158.95, 118.26) * mm, "radius": 1.5 * mm});
            skCircle(sketch, "E2.31.0.0", {"center": v(168.95, -111.74) * mm, "radius": 1.5 * mm});
            skCircle(sketch, "E2.31.1.0", {"center": v(168.95, -101.74) * mm, "radius": 1.5 * mm});
            skCircle(sketch, "E2.31.2.0", {"center": v(168.95, -91.74) * mm, "radius": 1.5 * mm});
            skCircle(sketch, "E2.31.3.0", {"center": v(168.95, -81.74) * mm, "radius": 1.5 * mm});
            skCircle(sketch, "E2.31.4.0", {"center": v(168.95, -71.74) * mm, "radius": 1.5 * mm});
            skCircle(sketch, "E2.31.5.0", {"center": v(168.95, -61.74) * mm, "radius": 1.5 * mm});
            skCircle(sketch, "E2.31.6.0", {"center": v(168.95, -51.74) * mm, "radius": 1.5 * mm});
            skCircle(sketch, "E2.31.7.0", {"center": v(168.95, -41.74) * mm, "radius": 1.5 * mm});
            skCircle(sketch, "E2.31.8.0", {"center": v(168.95, -31.74) * mm, "radius": 1.5 * mm});
            skCircle(sketch, "E2.31.9.0", {"center": v(168.95, -21.74) * mm, "radius": 1.5 * mm});
            skCircle(sketch, "E2.31.10.0", {"center": v(168.95, -11.74) * mm, "radius": 1.5 * mm});
            skCircle(sketch, "E2.31.11.0", {"center": v(168.95, -1.74) * mm, "radius": 1.5 * mm});
            skCircle(sketch, "E2.31.12.0", {"center": v(168.95, 8.26) * mm, "radius": 1.5 * mm});
            skCircle(sketch, "E2.31.13.0", {"center": v(168.95, 18.26) * mm, "radius": 1.5 * mm});
            skCircle(sketch, "E2.31.14.0", {"center": v(168.95, 28.26) * mm, "radius": 1.5 * mm});
            skCircle(sketch, "E2.31.15.0", {"center": v(168.95, 38.26) * mm, "radius": 1.5 * mm});
            skCircle(sketch, "E2.31.16.0", {"center": v(168.95, 48.26) * mm, "radius": 1.5 * mm});
            skCircle(sketch, "E2.31.17.0", {"center": v(168.95, 58.26) * mm, "radius": 1.5 * mm});
            skCircle(sketch, "E2.31.18.0", {"center": v(168.95, 68.26) * mm, "radius": 1.5 * mm});
            skCircle(sketch, "E2.31.19.0", {"center": v(168.95, 78.26) * mm, "radius": 1.5 * mm});
            skCircle(sketch, "E2.31.20.0", {"center": v(168.95, 88.26) * mm, "radius": 1.5 * mm});
            skCircle(sketch, "E2.31.21.0", {"center": v(168.95, 98.26) * mm, "radius": 1.5 * mm});
            skCircle(sketch, "E2.31.22.0", {"center": v(168.95, 108.26) * mm, "radius": 1.5 * mm});
            skCircle(sketch, "E2.31.23.0", {"center": v(168.95, 118.26) * mm, "radius": 1.5 * mm});
            skCircle(sketch, "E2.32.0.0", {"center": v(178.95, -111.74) * mm, "radius": 1.5 * mm});
            skCircle(sketch, "E2.32.1.0", {"center": v(178.95, -101.74) * mm, "radius": 1.5 * mm});
            skCircle(sketch, "E2.32.2.0", {"center": v(178.95, -91.74) * mm, "radius": 1.5 * mm});
            skCircle(sketch, "E2.32.3.0", {"center": v(178.95, -81.74) * mm, "radius": 1.5 * mm});
            skCircle(sketch, "E2.32.4.0", {"center": v(178.95, -71.74) * mm, "radius": 1.5 * mm});
            skCircle(sketch, "E2.32.5.0", {"center": v(178.95, -61.74) * mm, "radius": 1.5 * mm});
            skCircle(sketch, "E2.32.6.0", {"center": v(178.95, -51.74) * mm, "radius": 1.5 * mm});
            skCircle(sketch, "E2.32.7.0", {"center": v(178.95, -41.74) * mm, "radius": 1.5 * mm});
            skCircle(sketch, "E2.32.8.0", {"center": v(178.95, -31.74) * mm, "radius": 1.5 * mm});
            skCircle(sketch, "E2.32.9.0", {"center": v(178.95, -21.74) * mm, "radius": 1.5 * mm});
            skCircle(sketch, "E2.32.10.0", {"center": v(178.95, -11.74) * mm, "radius": 1.5 * mm});
            skCircle(sketch, "E2.32.11.0", {"center": v(178.95, -1.74) * mm, "radius": 1.5 * mm});
            skCircle(sketch, "E2.32.12.0", {"center": v(178.95, 8.26) * mm, "radius": 1.5 * mm});
            skCircle(sketch, "E2.32.13.0", {"center": v(178.95, 18.26) * mm, "radius": 1.5 * mm});
            skCircle(sketch, "E2.32.14.0", {"center": v(178.95, 28.26) * mm, "radius": 1.5 * mm});
            skCircle(sketch, "E2.32.15.0", {"center": v(178.95, 38.26) * mm, "radius": 1.5 * mm});
            skCircle(sketch, "E2.32.16.0", {"center": v(178.95, 48.26) * mm, "radius": 1.5 * mm});
            skCircle(sketch, "E2.32.17.0", {"center": v(178.95, 58.26) * mm, "radius": 1.5 * mm});
            skCircle(sketch, "E2.32.18.0", {"center": v(178.95, 68.26) * mm, "radius": 1.5 * mm});
            skCircle(sketch, "E2.32.19.0", {"center": v(178.95, 78.26) * mm, "radius": 1.5 * mm});
            skCircle(sketch, "E2.32.20.0", {"center": v(178.95, 88.26) * mm, "radius": 1.5 * mm});
            skCircle(sketch, "E2.32.21.0", {"center": v(178.95, 98.26) * mm, "radius": 1.5 * mm});
            skCircle(sketch, "E2.32.22.0", {"center": v(178.95, 108.26) * mm, "radius": 1.5 * mm});
            skCircle(sketch, "E2.32.23.0", {"center": v(178.95, 118.26) * mm, "radius": 1.5 * mm});
            skCircle(sketch, "E2.33.0.0", {"center": v(188.95, -111.74) * mm, "radius": 1.5 * mm});
            skCircle(sketch, "E2.33.1.0", {"center": v(188.95, -101.74) * mm, "radius": 1.5 * mm});
            skCircle(sketch, "E2.33.2.0", {"center": v(188.95, -91.74) * mm, "radius": 1.5 * mm});
            skCircle(sketch, "E2.33.3.0", {"center": v(188.95, -81.74) * mm, "radius": 1.5 * mm});
            skCircle(sketch, "E2.33.4.0", {"center": v(188.95, -71.74) * mm, "radius": 1.5 * mm});
            skCircle(sketch, "E2.33.5.0", {"center": v(188.95, -61.74) * mm, "radius": 1.5 * mm});
            skCircle(sketch, "E2.33.6.0", {"center": v(188.95, -51.74) * mm, "radius": 1.5 * mm});
            skCircle(sketch, "E2.33.7.0", {"center": v(188.95, -41.74) * mm, "radius": 1.5 * mm});
            skCircle(sketch, "E2.33.8.0", {"center": v(188.95, -31.74) * mm, "radius": 1.5 * mm});
            skCircle(sketch, "E2.33.9.0", {"center": v(188.95, -21.74) * mm, "radius": 1.5 * mm});
            skCircle(sketch, "E2.33.10.0", {"center": v(188.95, -11.74) * mm, "radius": 1.5 * mm});
            skCircle(sketch, "E2.33.11.0", {"center": v(188.95, -1.74) * mm, "radius": 1.5 * mm});
            skCircle(sketch, "E2.33.12.0", {"center": v(188.95, 8.26) * mm, "radius": 1.5 * mm});
            skCircle(sketch, "E2.33.13.0", {"center": v(188.95, 18.26) * mm, "radius": 1.5 * mm});
            skCircle(sketch, "E2.33.14.0", {"center": v(188.95, 28.26) * mm, "radius": 1.5 * mm});
            skCircle(sketch, "E2.33.15.0", {"center": v(188.95, 38.26) * mm, "radius": 1.5 * mm});
            skCircle(sketch, "E2.33.16.0", {"center": v(188.95, 48.26) * mm, "radius": 1.5 * mm});
            skCircle(sketch, "E2.33.17.0", {"center": v(188.95, 58.26) * mm, "radius": 1.5 * mm});
            skCircle(sketch, "E2.33.18.0", {"center": v(188.95, 68.26) * mm, "radius": 1.5 * mm});
            skCircle(sketch, "E2.33.19.0", {"center": v(188.95, 78.26) * mm, "radius": 1.5 * mm});
            skCircle(sketch, "E2.33.20.0", {"center": v(188.95, 88.26) * mm, "radius": 1.5 * mm});
            skCircle(sketch, "E2.33.21.0", {"center": v(188.95, 98.26) * mm, "radius": 1.5 * mm});
            skCircle(sketch, "E2.33.22.0", {"center": v(188.95, 108.26) * mm, "radius": 1.5 * mm});
            skCircle(sketch, "E2.33.23.0", {"center": v(188.95, 118.26) * mm, "radius": 1.5 * mm});
            skCircle(sketch, "E2.34.0.0", {"center": v(198.95, -111.74) * mm, "radius": 1.5 * mm});
            skCircle(sketch, "E2.34.1.0", {"center": v(198.95, -101.74) * mm, "radius": 1.5 * mm});
            skCircle(sketch, "E2.34.2.0", {"center": v(198.95, -91.74) * mm, "radius": 1.5 * mm});
            skCircle(sketch, "E2.34.3.0", {"center": v(198.95, -81.74) * mm, "radius": 1.5 * mm});
            skCircle(sketch, "E2.34.4.0", {"center": v(198.95, -71.74) * mm, "radius": 1.5 * mm});
            skCircle(sketch, "E2.34.5.0", {"center": v(198.95, -61.74) * mm, "radius": 1.5 * mm});
            skCircle(sketch, "E2.34.6.0", {"center": v(198.95, -51.74) * mm, "radius": 1.5 * mm});
            skCircle(sketch, "E2.34.7.0", {"center": v(198.95, -41.74) * mm, "radius": 1.5 * mm});
            skCircle(sketch, "E2.34.8.0", {"center": v(198.95, -31.74) * mm, "radius": 1.5 * mm});
            skCircle(sketch, "E2.34.9.0", {"center": v(198.95, -21.74) * mm, "radius": 1.5 * mm});
            skCircle(sketch, "E2.34.10.0", {"center": v(198.95, -11.74) * mm, "radius": 1.5 * mm});
            skCircle(sketch, "E2.34.11.0", {"center": v(198.95, -1.74) * mm, "radius": 1.5 * mm});
            skCircle(sketch, "E2.34.12.0", {"center": v(198.95, 8.26) * mm, "radius": 1.5 * mm});
            skCircle(sketch, "E2.34.13.0", {"center": v(198.95, 18.26) * mm, "radius": 1.5 * mm});
            skCircle(sketch, "E2.34.14.0", {"center": v(198.95, 28.26) * mm, "radius": 1.5 * mm});
            skCircle(sketch, "E2.34.15.0", {"center": v(198.95, 38.26) * mm, "radius": 1.5 * mm});
            skCircle(sketch, "E2.34.16.0", {"center": v(198.95, 48.26) * mm, "radius": 1.5 * mm});
            skCircle(sketch, "E2.34.17.0", {"center": v(198.95, 58.26) * mm, "radius": 1.5 * mm});
            skCircle(sketch, "E2.34.18.0", {"center": v(198.95, 68.26) * mm, "radius": 1.5 * mm});
            skCircle(sketch, "E2.34.19.0", {"center": v(198.95, 78.26) * mm, "radius": 1.5 * mm});
            skCircle(sketch, "E2.34.20.0", {"center": v(198.95, 88.26) * mm, "radius": 1.5 * mm});
            skCircle(sketch, "E2.34.21.0", {"center": v(198.95, 98.26) * mm, "radius": 1.5 * mm});
            skCircle(sketch, "E2.34.22.0", {"center": v(198.95, 108.26) * mm, "radius": 1.5 * mm});
            skCircle(sketch, "E2.34.23.0", {"center": v(198.95, 118.26) * mm, "radius": 1.5 * mm});
            skLineSegment(sketch, "E2.direction1", {"start": v(-141.05, -111.74) * mm, "end": v(-131.05, -111.74) * mm, "construction": true});
            skLineSegment(sketch, "E2.direction2", {"start": v(-141.05, -111.74) * mm, "end": v(-141.05, -101.74) * mm, "construction": true});
            skCircle(sketch, "E3.0.35.0", {"center": v(208.95, -111.74) * mm, "radius": 1.5 * mm});
            skCircle(sketch, "E3.0.35.1", {"center": v(208.95, -101.74) * mm, "radius": 1.5 * mm});
            skCircle(sketch, "E3.0.35.2", {"center": v(208.95, -91.74) * mm, "radius": 1.5 * mm});
            skCircle(sketch, "E3.0.35.3", {"center": v(208.95, -81.74) * mm, "radius": 1.5 * mm});
            skCircle(sketch, "E3.0.35.4", {"center": v(208.95, -71.74) * mm, "radius": 1.5 * mm});
            skCircle(sketch, "E3.0.35.5", {"center": v(208.95, -61.74) * mm, "radius": 1.5 * mm});
            skCircle(sketch, "E3.0.35.6", {"center": v(208.95, -51.74) * mm, "radius": 1.5 * mm});
            skCircle(sketch, "E3.0.35.7", {"center": v(208.95, -41.74) * mm, "radius": 1.5 * mm});
            skCircle(sketch, "E3.0.35.8", {"center": v(208.95, -31.74) * mm, "radius": 1.5 * mm});
            skCircle(sketch, "E3.0.35.9", {"center": v(208.95, -21.74) * mm, "radius": 1.5 * mm});
            skCircle(sketch, "E3.0.35.10", {"center": v(208.95, -11.74) * mm, "radius": 1.5 * mm});
            skCircle(sketch, "E3.0.35.11", {"center": v(208.95, -1.74) * mm, "radius": 1.5 * mm});
            skCircle(sketch, "E3.0.35.12", {"center": v(208.95, 8.26) * mm, "radius": 1.5 * mm});
            skCircle(sketch, "E3.0.35.13", {"center": v(208.95, 18.26) * mm, "radius": 1.5 * mm});
            skCircle(sketch, "E3.0.35.14", {"center": v(208.95, 28.26) * mm, "radius": 1.5 * mm});
            skCircle(sketch, "E3.0.35.15", {"center": v(208.95, 38.26) * mm, "radius": 1.5 * mm});
            skCircle(sketch, "E3.0.35.16", {"center": v(208.95, 48.26) * mm, "radius": 1.5 * mm});
            skCircle(sketch, "E3.0.35.17", {"center": v(208.95, 58.26) * mm, "radius": 1.5 * mm});
            skCircle(sketch, "E3.0.35.18", {"center": v(208.95, 68.26) * mm, "radius": 1.5 * mm});
            skCircle(sketch, "E3.0.35.19", {"center": v(208.95, 78.26) * mm, "radius": 1.5 * mm});
            skCircle(sketch, "E3.0.35.20", {"center": v(208.95, 88.26) * mm, "radius": 1.5 * mm});
            skCircle(sketch, "E3.0.35.21", {"center": v(208.95, 98.26) * mm, "radius": 1.5 * mm});
            skCircle(sketch, "E3.0.35.22", {"center": v(208.95, 108.26) * mm, "radius": 1.5 * mm});
            skCircle(sketch, "E3.0.35.23", {"center": v(208.95, 118.26) * mm, "radius": 1.5 * mm});
            skCircle(sketch, "E3.0.36.0", {"center": v(218.95, -111.74) * mm, "radius": 1.5 * mm});
            skCircle(sketch, "E3.0.36.1", {"center": v(218.95, -101.74) * mm, "radius": 1.5 * mm});
            skCircle(sketch, "E3.0.36.2", {"center": v(218.95, -91.74) * mm, "radius": 1.5 * mm});
            skCircle(sketch, "E3.0.36.3", {"center": v(218.95, -81.74) * mm, "radius": 1.5 * mm});
            skCircle(sketch, "E3.0.36.4", {"center": v(218.95, -71.74) * mm, "radius": 1.5 * mm});
            skCircle(sketch, "E3.0.36.5", {"center": v(218.95, -61.74) * mm, "radius": 1.5 * mm});
            skCircle(sketch, "E3.0.36.6", {"center": v(218.95, -51.74) * mm, "radius": 1.5 * mm});
            skCircle(sketch, "E3.0.36.7", {"center": v(218.95, -41.74) * mm, "radius": 1.5 * mm});
            skCircle(sketch, "E3.0.36.8", {"center": v(218.95, -31.74) * mm, "radius": 1.5 * mm});
            skCircle(sketch, "E3.0.36.9", {"center": v(218.95, -21.74) * mm, "radius": 1.5 * mm});
            skCircle(sketch, "E3.0.36.10", {"center": v(218.95, -11.74) * mm, "radius": 1.5 * mm});
            skCircle(sketch, "E3.0.36.11", {"center": v(218.95, -1.74) * mm, "radius": 1.5 * mm});
            skCircle(sketch, "E3.0.36.12", {"center": v(218.95, 8.26) * mm, "radius": 1.5 * mm});
            skCircle(sketch, "E3.0.36.13", {"center": v(218.95, 18.26) * mm, "radius": 1.5 * mm});
            skCircle(sketch, "E3.0.36.14", {"center": v(218.95, 28.26) * mm, "radius": 1.5 * mm});
            skCircle(sketch, "E3.0.36.15", {"center": v(218.95, 38.26) * mm, "radius": 1.5 * mm});
            skCircle(sketch, "E3.0.36.16", {"center": v(218.95, 48.26) * mm, "radius": 1.5 * mm});
            skCircle(sketch, "E3.0.36.17", {"center": v(218.95, 58.26) * mm, "radius": 1.5 * mm});
            skCircle(sketch, "E3.0.36.18", {"center": v(218.95, 68.26) * mm, "radius": 1.5 * mm});
            skCircle(sketch, "E3.0.36.19", {"center": v(218.95, 78.26) * mm, "radius": 1.5 * mm});
            skCircle(sketch, "E3.0.36.20", {"center": v(218.95, 88.26) * mm, "radius": 1.5 * mm});
            skCircle(sketch, "E3.0.36.21", {"center": v(218.95, 98.26) * mm, "radius": 1.5 * mm});
            skCircle(sketch, "E3.0.36.22", {"center": v(218.95, 108.26) * mm, "radius": 1.5 * mm});
            skCircle(sketch, "E3.0.36.23", {"center": v(218.95, 118.26) * mm, "radius": 1.5 * mm});
            skCircle(sketch, "E4.0.0.24", {"center": v(-141.05, 128.26) * mm, "radius": 1.5 * mm});
            skCircle(sketch, "E4.0.1.24", {"center": v(-131.05, 128.26) * mm, "radius": 1.5 * mm});
            skCircle(sketch, "E4.0.2.24", {"center": v(-121.05, 128.26) * mm, "radius": 1.5 * mm});
            skCircle(sketch, "E4.0.3.24", {"center": v(-111.05, 128.26) * mm, "radius": 1.5 * mm});
            skCircle(sketch, "E4.0.4.24", {"center": v(-101.05, 128.26) * mm, "radius": 1.5 * mm});
            skCircle(sketch, "E4.0.5.24", {"center": v(-91.05, 128.26) * mm, "radius": 1.5 * mm});
            skCircle(sketch, "E4.0.6.24", {"center": v(-81.05, 128.26) * mm, "radius": 1.5 * mm});
            skCircle(sketch, "E4.0.7.24", {"center": v(-71.05, 128.26) * mm, "radius": 1.5 * mm});
            skCircle(sketch, "E4.0.8.24", {"center": v(-61.05, 128.26) * mm, "radius": 1.5 * mm});
            skCircle(sketch, "E4.0.9.24", {"center": v(-51.05, 128.26) * mm, "radius": 1.5 * mm});
            skCircle(sketch, "E4.0.10.24", {"center": v(-41.05, 128.26) * mm, "radius": 1.5 * mm});
            skCircle(sketch, "E4.0.11.24", {"center": v(-31.05, 128.26) * mm, "radius": 1.5 * mm});
            skCircle(sketch, "E4.0.12.24", {"center": v(-21.05, 128.26) * mm, "radius": 1.5 * mm});
            skCircle(sketch, "E4.0.13.24", {"center": v(-11.05, 128.26) * mm, "radius": 1.5 * mm});
            skCircle(sketch, "E4.0.14.24", {"center": v(-1.05, 128.26) * mm, "radius": 1.5 * mm});
            skCircle(sketch, "E4.0.15.24", {"center": v(8.95, 128.26) * mm, "radius": 1.5 * mm});
            skCircle(sketch, "E4.0.16.24", {"center": v(18.95, 128.26) * mm, "radius": 1.5 * mm});
            skCircle(sketch, "E4.0.17.24", {"center": v(28.95, 128.26) * mm, "radius": 1.5 * mm});
            skCircle(sketch, "E4.0.18.24", {"center": v(38.95, 128.26) * mm, "radius": 1.5 * mm});
            skCircle(sketch, "E4.0.19.24", {"center": v(48.95, 128.26) * mm, "radius": 1.5 * mm});
            skCircle(sketch, "E4.0.20.24", {"center": v(58.95, 128.26) * mm, "radius": 1.5 * mm});
            skCircle(sketch, "E4.0.21.24", {"center": v(68.95, 128.26) * mm, "radius": 1.5 * mm});
            skCircle(sketch, "E4.0.22.24", {"center": v(78.95, 128.26) * mm, "radius": 1.5 * mm});
            skCircle(sketch, "E4.0.23.24", {"center": v(88.95, 128.26) * mm, "radius": 1.5 * mm});
            skCircle(sketch, "E4.0.24.24", {"center": v(98.95, 128.26) * mm, "radius": 1.5 * mm});
            skCircle(sketch, "E4.0.25.24", {"center": v(108.95, 128.26) * mm, "radius": 1.5 * mm});
            skCircle(sketch, "E4.0.26.24", {"center": v(118.95, 128.26) * mm, "radius": 1.5 * mm});
            skCircle(sketch, "E4.0.27.24", {"center": v(128.95, 128.26) * mm, "radius": 1.5 * mm});
            skCircle(sketch, "E4.0.28.24", {"center": v(138.95, 128.26) * mm, "radius": 1.5 * mm});
            skCircle(sketch, "E4.0.29.24", {"center": v(148.95, 128.26) * mm, "radius": 1.5 * mm});
            skCircle(sketch, "E4.0.30.24", {"center": v(158.95, 128.26) * mm, "radius": 1.5 * mm});
            skCircle(sketch, "E4.0.31.24", {"center": v(168.95, 128.26) * mm, "radius": 1.5 * mm});
            skCircle(sketch, "E4.0.32.24", {"center": v(178.95, 128.26) * mm, "radius": 1.5 * mm});
            skCircle(sketch, "E4.0.33.24", {"center": v(188.95, 128.26) * mm, "radius": 1.5 * mm});
            skCircle(sketch, "E4.0.34.24", {"center": v(198.95, 128.26) * mm, "radius": 1.5 * mm});
            skCircle(sketch, "E4.0.35.24", {"center": v(208.95, 128.26) * mm, "radius": 1.5 * mm});
            skCircle(sketch, "E4.0.36.24", {"center": v(218.95, 128.26) * mm, "radius": 1.5 * mm});
            skLineSegment(sketch, "E5.bottom", {"start": v(-151.05, -121.74) * mm, "end": v(228.95, -121.74) * mm});
            skLineSegment(sketch, "E5.top", {"start": v(-151.05, 138.26) * mm, "end": v(228.95, 138.26) * mm});
            skLineSegment(sketch, "E5.left", {"start": v(-151.05, -121.74) * mm, "end": v(-151.05, 138.26) * mm});
            skLineSegment(sketch, "E5.right", {"start": v(228.95, -121.74) * mm, "end": v(228.95, 138.26) * mm});
            skSolve(sketch);
        }
        {
            var Q0;
            Q0=makeQuery(id+"F0.imprint","IMPRINT",FACE,{"disambiguationData":[TD([[makeQuery(id+"F0.imprint","IMPRINT",EDGE,{"derivedFrom":sQuery(id+"F0.wireOp",EDGE,"E0.bottom")}),-1.0]])]});
            extrude(context, id + "F1", {"entities" : qUnion([Q0]), "depth" : 9 * mm, "offsetDistance" : 25 * mm});
        }
        {
            var Q0;
            Q0=makeQuery(id+"F0.imprint","IMPRINT",FACE,{"disambiguationData":[TD([[makeQuery(id+"F0.imprint","IMPRINT",EDGE,{"derivedFrom":sQuery(id+"F0.wireOp",EDGE,"E0.bottom")}),1.0]])]});
            extrude(context, id + "F2", {"entities" : qUnion([Q0]), "operationType" : NewBodyOperationType.ADD, "depth" : 4 * mm, "offsetDistance" : 25 * mm});
        }
        {
            var Q0;
            {var subQ0=sQuery(id+"F0.wireOp",EDGE,"E0.right");var subQ1=sQuery(id+"F0.wireOp",EDGE,"E0.left");var subQ2=sQuery(id+"F0.wireOp",EDGE,"E0.top");var subQ3=sQuery(id+"F0.wireOp",EDGE,"E0.bottom");Q0=makeQuery(id+"F2.boolean.opBoolean","MERGE",FACE,{"derivedFrom":[makeQuery(id+"F1.opExtrude","CAP_FACE",FACE,{"disambiguationData":[OSD([subQ3,subQ2,subQ1,subQ0,sQuery(id+"F0.wireOp",EDGE,"E1"),sQuery(id+"F0.wireOp",EDGE,"E2.0.1.0"),sQuery(id+"F0.wireOp",EDGE,"E2.0.2.0"),sQuery(id+"F0.wireOp",EDGE,"E2.0.3.0"),sQuery(id+"F0.wireOp",EDGE,"E2.0.4.0"),sQuery(id+"F0.wireOp",EDGE,"E2.0.5.0"),sQuery(id+"F0.wireOp",EDGE,"E2.0.6.0"),sQuery(id+"F0.wireOp",EDGE,"E2.0.7.0"),sQuery(id+"F0.wireOp",EDGE,"E2.0.8.0"),sQuery(id+"F0.wireOp",EDGE,"E2.0.9.0"),sQuery(id+"F0.wireOp",EDGE,"E2.0.10.0"),sQuery(id+"F0.wireOp",EDGE,"E2.0.11.0"),sQuery(id+"F0.wireOp",EDGE,"E2.0.12.0"),sQuery(id+"F0.wireOp",EDGE,"E2.0.13.0"),sQuery(id+"F0.wireOp",EDGE,"E2.0.14.0"),sQuery(id+"F0.wireOp",EDGE,"E2.0.15.0"),sQuery(id+"F0.wireOp",EDGE,"E2.0.16.0"),sQuery(id+"F0.wireOp",EDGE,"E2.0.17.0"),sQuery(id+"F0.wireOp",EDGE,"E2.0.18.0"),sQuery(id+"F0.wireOp",EDGE,"E2.0.19.0"),sQuery(id+"F0.wireOp",EDGE,"E2.0.20.0"),sQuery(id+"F0.wireOp",EDGE,"E2.0.21.0"),sQuery(id+"F0.wireOp",EDGE,"E2.0.22.0"),sQuery(id+"F0.wireOp",EDGE,"E2.0.23.0"),sQuery(id+"F0.wireOp",EDGE,"E2.1.0.0"),sQuery(id+"F0.wireOp",EDGE,"E2.1.1.0"),sQuery(id+"F0.wireOp",EDGE,"E2.1.2.0"),sQuery(id+"F0.wireOp",EDGE,"E2.1.3.0"),sQuery(id+"F0.wireOp",EDGE,"E2.1.4.0"),sQuery(id+"F0.wireOp",EDGE,"E2.1.5.0"),sQuery(id+"F0.wireOp",EDGE,"E2.1.6.0"),sQuery(id+"F0.wireOp",EDGE,"E2.1.7.0"),sQuery(id+"F0.wireOp",EDGE,"E2.1.8.0"),sQuery(id+"F0.wireOp",EDGE,"E2.1.9.0"),sQuery(id+"F0.wireOp",EDGE,"E2.1.10.0"),sQuery(id+"F0.wireOp",EDGE,"E2.1.11.0"),sQuery(id+"F0.wireOp",EDGE,"E2.1.12.0"),sQuery(id+"F0.wireOp",EDGE,"E2.1.13.0"),sQuery(id+"F0.wireOp",EDGE,"E2.1.14.0"),sQuery(id+"F0.wireOp",EDGE,"E2.1.15.0"),sQuery(id+"F0.wireOp",EDGE,"E2.1.16.0"),sQuery(id+"F0.wireOp",EDGE,"E2.1.17.0"),sQuery(id+"F0.wireOp",EDGE,"E2.1.18.0"),sQuery(id+"F0.wireOp",EDGE,"E2.1.19.0"),sQuery(id+"F0.wireOp",EDGE,"E2.1.20.0"),sQuery(id+"F0.wireOp",EDGE,"E2.1.21.0"),sQuery(id+"F0.wireOp",EDGE,"E2.1.22.0"),sQuery(id+"F0.wireOp",EDGE,"E2.1.23.0"),sQuery(id+"F0.wireOp",EDGE,"E2.2.0.0"),sQuery(id+"F0.wireOp",EDGE,"E2.2.1.0"),sQuery(id+"F0.wireOp",EDGE,"E2.2.2.0"),sQuery(id+"F0.wireOp",EDGE,"E2.2.3.0"),sQuery(id+"F0.wireOp",EDGE,"E2.2.4.0"),sQuery(id+"F0.wireOp",EDGE,"E2.2.5.0"),sQuery(id+"F0.wireOp",EDGE,"E2.2.6.0"),sQuery(id+"F0.wireOp",EDGE,"E2.2.7.0"),sQuery(id+"F0.wireOp",EDGE,"E2.2.8.0"),sQuery(id+"F0.wireOp",EDGE,"E2.2.9.0"),sQuery(id+"F0.wireOp",EDGE,"E2.2.10.0"),sQuery(id+"F0.wireOp",EDGE,"E2.2.11.0"),sQuery(id+"F0.wireOp",EDGE,"E2.2.12.0"),sQuery(id+"F0.wireOp",EDGE,"E2.2.13.0"),sQuery(id+"F0.wireOp",EDGE,"E2.2.14.0"),sQuery(id+"F0.wireOp",EDGE,"E2.2.15.0"),sQuery(id+"F0.wireOp",EDGE,"E2.2.16.0"),sQuery(id+"F0.wireOp",EDGE,"E2.2.17.0"),sQuery(id+"F0.wireOp",EDGE,"E2.2.18.0"),sQuery(id+"F0.wireOp",EDGE,"E2.2.19.0"),sQuery(id+"F0.wireOp",EDGE,"E2.2.20.0"),sQuery(id+"F0.wireOp",EDGE,"E2.2.21.0"),sQuery(id+"F0.wireOp",EDGE,"E2.2.22.0"),sQuery(id+"F0.wireOp",EDGE,"E2.2.23.0"),sQuery(id+"F0.wireOp",EDGE,"E2.3.0.0"),sQuery(id+"F0.wireOp",EDGE,"E2.3.1.0"),sQuery(id+"F0.wireOp",EDGE,"E2.3.2.0"),sQuery(id+"F0.wireOp",EDGE,"E2.3.3.0"),sQuery(id+"F0.wireOp",EDGE,"E2.3.4.0"),sQuery(id+"F0.wireOp",EDGE,"E2.3.5.0"),sQuery(id+"F0.wireOp",EDGE,"E2.3.6.0"),sQuery(id+"F0.wireOp",EDGE,"E2.3.7.0"),sQuery(id+"F0.wireOp",EDGE,"E2.3.8.0"),sQuery(id+"F0.wireOp",EDGE,"E2.3.9.0"),sQuery(id+"F0.wireOp",EDGE,"E2.3.10.0"),sQuery(id+"F0.wireOp",EDGE,"E2.3.11.0"),sQuery(id+"F0.wireOp",EDGE,"E2.3.12.0"),sQuery(id+"F0.wireOp",EDGE,"E2.3.13.0"),sQuery(id+"F0.wireOp",EDGE,"E2.3.14.0"),sQuery(id+"F0.wireOp",EDGE,"E2.3.15.0"),sQuery(id+"F0.wireOp",EDGE,"E2.3.16.0"),sQuery(id+"F0.wireOp",EDGE,"E2.3.17.0"),sQuery(id+"F0.wireOp",EDGE,"E2.3.18.0"),sQuery(id+"F0.wireOp",EDGE,"E2.3.19.0"),sQuery(id+"F0.wireOp",EDGE,"E2.3.20.0"),sQuery(id+"F0.wireOp",EDGE,"E2.3.21.0"),sQuery(id+"F0.wireOp",EDGE,"E2.3.22.0"),sQuery(id+"F0.wireOp",EDGE,"E2.3.23.0"),sQuery(id+"F0.wireOp",EDGE,"E2.4.0.0"),sQuery(id+"F0.wireOp",EDGE,"E2.4.1.0"),sQuery(id+"F0.wireOp",EDGE,"E2.4.2.0"),sQuery(id+"F0.wireOp",EDGE,"E2.4.3.0"),sQuery(id+"F0.wireOp",EDGE,"E2.4.4.0"),sQuery(id+"F0.wireOp",EDGE,"E2.4.5.0"),sQuery(id+"F0.wireOp",EDGE,"E2.4.6.0"),sQuery(id+"F0.wireOp",EDGE,"E2.4.7.0"),sQuery(id+"F0.wireOp",EDGE,"E2.4.8.0"),sQuery(id+"F0.wireOp",EDGE,"E2.4.9.0"),sQuery(id+"F0.wireOp",EDGE,"E2.4.10.0"),sQuery(id+"F0.wireOp",EDGE,"E2.4.11.0"),sQuery(id+"F0.wireOp",EDGE,"E2.4.12.0"),sQuery(id+"F0.wireOp",EDGE,"E2.4.13.0"),sQuery(id+"F0.wireOp",EDGE,"E2.4.14.0"),sQuery(id+"F0.wireOp",EDGE,"E2.4.15.0"),sQuery(id+"F0.wireOp",EDGE,"E2.4.16.0"),sQuery(id+"F0.wireOp",EDGE,"E2.4.17.0"),sQuery(id+"F0.wireOp",EDGE,"E2.4.18.0"),sQuery(id+"F0.wireOp",EDGE,"E2.4.19.0"),sQuery(id+"F0.wireOp",EDGE,"E2.4.20.0"),sQuery(id+"F0.wireOp",EDGE,"E2.4.21.0"),sQuery(id+"F0.wireOp",EDGE,"E2.4.22.0"),sQuery(id+"F0.wireOp",EDGE,"E2.4.23.0"),sQuery(id+"F0.wireOp",EDGE,"E2.5.0.0"),sQuery(id+"F0.wireOp",EDGE,"E2.5.1.0"),sQuery(id+"F0.wireOp",EDGE,"E2.5.2.0"),sQuery(id+"F0.wireOp",EDGE,"E2.5.3.0"),sQuery(id+"F0.wireOp",EDGE,"E2.5.4.0"),sQuery(id+"F0.wireOp",EDGE,"E2.5.5.0"),sQuery(id+"F0.wireOp",EDGE,"E2.5.6.0"),sQuery(id+"F0.wireOp",EDGE,"E2.5.7.0"),sQuery(id+"F0.wireOp",EDGE,"E2.5.8.0"),sQuery(id+"F0.wireOp",EDGE,"E2.5.9.0"),sQuery(id+"F0.wireOp",EDGE,"E2.5.10.0"),sQuery(id+"F0.wireOp",EDGE,"E2.5.11.0"),sQuery(id+"F0.wireOp",EDGE,"E2.5.12.0"),sQuery(id+"F0.wireOp",EDGE,"E2.5.13.0"),sQuery(id+"F0.wireOp",EDGE,"E2.5.14.0"),sQuery(id+"F0.wireOp",EDGE,"E2.5.15.0"),sQuery(id+"F0.wireOp",EDGE,"E2.5.16.0"),sQuery(id+"F0.wireOp",EDGE,"E2.5.17.0"),sQuery(id+"F0.wireOp",EDGE,"E2.5.18.0"),sQuery(id+"F0.wireOp",EDGE,"E2.5.19.0"),sQuery(id+"F0.wireOp",EDGE,"E2.5.20.0"),sQuery(id+"F0.wireOp",EDGE,"E2.5.21.0"),sQuery(id+"F0.wireOp",EDGE,"E2.5.22.0"),sQuery(id+"F0.wireOp",EDGE,"E2.5.23.0"),sQuery(id+"F0.wireOp",EDGE,"E2.6.0.0"),sQuery(id+"F0.wireOp",EDGE,"E2.6.1.0"),sQuery(id+"F0.wireOp",EDGE,"E2.6.2.0"),sQuery(id+"F0.wireOp",EDGE,"E2.6.3.0"),sQuery(id+"F0.wireOp",EDGE,"E2.6.4.0"),sQuery(id+"F0.wireOp",EDGE,"E2.6.5.0"),sQuery(id+"F0.wireOp",EDGE,"E2.6.6.0"),sQuery(id+"F0.wireOp",EDGE,"E2.6.7.0"),sQuery(id+"F0.wireOp",EDGE,"E2.6.8.0"),sQuery(id+"F0.wireOp",EDGE,"E2.6.9.0"),sQuery(id+"F0.wireOp",EDGE,"E2.6.10.0"),sQuery(id+"F0.wireOp",EDGE,"E2.6.11.0"),sQuery(id+"F0.wireOp",EDGE,"E2.6.12.0"),sQuery(id+"F0.wireOp",EDGE,"E2.6.13.0"),sQuery(id+"F0.wireOp",EDGE,"E2.6.14.0"),sQuery(id+"F0.wireOp",EDGE,"E2.6.15.0"),sQuery(id+"F0.wireOp",EDGE,"E2.6.16.0"),sQuery(id+"F0.wireOp",EDGE,"E2.6.17.0"),sQuery(id+"F0.wireOp",EDGE,"E2.6.18.0"),sQuery(id+"F0.wireOp",EDGE,"E2.6.19.0"),sQuery(id+"F0.wireOp",EDGE,"E2.6.20.0"),sQuery(id+"F0.wireOp",EDGE,"E2.6.21.0"),sQuery(id+"F0.wireOp",EDGE,"E2.6.22.0"),sQuery(id+"F0.wireOp",EDGE,"E2.6.23.0"),sQuery(id+"F0.wireOp",EDGE,"E2.7.0.0"),sQuery(id+"F0.wireOp",EDGE,"E2.7.1.0"),sQuery(id+"F0.wireOp",EDGE,"E2.7.2.0"),sQuery(id+"F0.wireOp",EDGE,"E2.7.3.0"),sQuery(id+"F0.wireOp",EDGE,"E2.7.4.0"),sQuery(id+"F0.wireOp",EDGE,"E2.7.5.0"),sQuery(id+"F0.wireOp",EDGE,"E2.7.6.0"),sQuery(id+"F0.wireOp",EDGE,"E2.7.7.0"),sQuery(id+"F0.wireOp",EDGE,"E2.7.8.0"),sQuery(id+"F0.wireOp",EDGE,"E2.7.9.0"),sQuery(id+"F0.wireOp",EDGE,"E2.7.10.0"),sQuery(id+"F0.wireOp",EDGE,"E2.7.11.0"),sQuery(id+"F0.wireOp",EDGE,"E2.7.12.0"),sQuery(id+"F0.wireOp",EDGE,"E2.7.13.0"),sQuery(id+"F0.wireOp",EDGE,"E2.7.14.0"),sQuery(id+"F0.wireOp",EDGE,"E2.7.15.0"),sQuery(id+"F0.wireOp",EDGE,"E2.7.16.0"),sQuery(id+"F0.wireOp",EDGE,"E2.7.17.0"),sQuery(id+"F0.wireOp",EDGE,"E2.7.18.0"),sQuery(id+"F0.wireOp",EDGE,"E2.7.19.0"),sQuery(id+"F0.wireOp",EDGE,"E2.7.20.0"),sQuery(id+"F0.wireOp",EDGE,"E2.7.21.0"),sQuery(id+"F0.wireOp",EDGE,"E2.7.22.0"),sQuery(id+"F0.wireOp",EDGE,"E2.7.23.0"),sQuery(id+"F0.wireOp",EDGE,"E2.8.0.0"),sQuery(id+"F0.wireOp",EDGE,"E2.8.1.0"),sQuery(id+"F0.wireOp",EDGE,"E2.8.2.0"),sQuery(id+"F0.wireOp",EDGE,"E2.8.3.0"),sQuery(id+"F0.wireOp",EDGE,"E2.8.4.0"),sQuery(id+"F0.wireOp",EDGE,"E2.8.5.0"),sQuery(id+"F0.wireOp",EDGE,"E2.8.6.0"),sQuery(id+"F0.wireOp",EDGE,"E2.8.7.0"),sQuery(id+"F0.wireOp",EDGE,"E2.8.8.0"),sQuery(id+"F0.wireOp",EDGE,"E2.8.9.0"),sQuery(id+"F0.wireOp",EDGE,"E2.8.10.0"),sQuery(id+"F0.wireOp",EDGE,"E2.8.11.0"),sQuery(id+"F0.wireOp",EDGE,"E2.8.12.0"),sQuery(id+"F0.wireOp",EDGE,"E2.8.13.0"),sQuery(id+"F0.wireOp",EDGE,"E2.8.14.0"),sQuery(id+"F0.wireOp",EDGE,"E2.8.15.0"),sQuery(id+"F0.wireOp",EDGE,"E2.8.16.0"),sQuery(id+"F0.wireOp",EDGE,"E2.8.17.0"),sQuery(id+"F0.wireOp",EDGE,"E2.8.18.0"),sQuery(id+"F0.wireOp",EDGE,"E2.8.19.0"),sQuery(id+"F0.wireOp",EDGE,"E2.8.20.0"),sQuery(id+"F0.wireOp",EDGE,"E2.8.21.0"),sQuery(id+"F0.wireOp",EDGE,"E2.8.22.0"),sQuery(id+"F0.wireOp",EDGE,"E2.8.23.0"),sQuery(id+"F0.wireOp",EDGE,"E2.9.0.0"),sQuery(id+"F0.wireOp",EDGE,"E2.9.1.0"),sQuery(id+"F0.wireOp",EDGE,"E2.9.2.0"),sQuery(id+"F0.wireOp",EDGE,"E2.9.3.0"),sQuery(id+"F0.wireOp",EDGE,"E2.9.4.0"),sQuery(id+"F0.wireOp",EDGE,"E2.9.5.0"),sQuery(id+"F0.wireOp",EDGE,"E2.9.6.0"),sQuery(id+"F0.wireOp",EDGE,"E2.9.7.0"),sQuery(id+"F0.wireOp",EDGE,"E2.9.8.0"),sQuery(id+"F0.wireOp",EDGE,"E2.9.9.0"),sQuery(id+"F0.wireOp",EDGE,"E2.9.10.0"),sQuery(id+"F0.wireOp",EDGE,"E2.9.11.0"),sQuery(id+"F0.wireOp",EDGE,"E2.9.12.0"),sQuery(id+"F0.wireOp",EDGE,"E2.9.13.0"),sQuery(id+"F0.wireOp",EDGE,"E2.9.14.0"),sQuery(id+"F0.wireOp",EDGE,"E2.9.15.0"),sQuery(id+"F0.wireOp",EDGE,"E2.9.16.0"),sQuery(id+"F0.wireOp",EDGE,"E2.9.17.0"),sQuery(id+"F0.wireOp",EDGE,"E2.9.18.0"),sQuery(id+"F0.wireOp",EDGE,"E2.9.19.0"),sQuery(id+"F0.wireOp",EDGE,"E2.9.20.0"),sQuery(id+"F0.wireOp",EDGE,"E2.9.21.0"),sQuery(id+"F0.wireOp",EDGE,"E2.9.22.0"),sQuery(id+"F0.wireOp",EDGE,"E2.9.23.0"),sQuery(id+"F0.wireOp",EDGE,"E2.10.0.0"),sQuery(id+"F0.wireOp",EDGE,"E2.10.1.0"),sQuery(id+"F0.wireOp",EDGE,"E2.10.2.0"),sQuery(id+"F0.wireOp",EDGE,"E2.10.3.0"),sQuery(id+"F0.wireOp",EDGE,"E2.10.4.0"),sQuery(id+"F0.wireOp",EDGE,"E2.10.5.0"),sQuery(id+"F0.wireOp",EDGE,"E2.10.6.0"),sQuery(id+"F0.wireOp",EDGE,"E2.10.7.0"),sQuery(id+"F0.wireOp",EDGE,"E2.10.8.0"),sQuery(id+"F0.wireOp",EDGE,"E2.10.9.0"),sQuery(id+"F0.wireOp",EDGE,"E2.10.10.0"),sQuery(id+"F0.wireOp",EDGE,"E2.10.11.0"),sQuery(id+"F0.wireOp",EDGE,"E2.10.12.0"),sQuery(id+"F0.wireOp",EDGE,"E2.10.13.0"),sQuery(id+"F0.wireOp",EDGE,"E2.10.14.0"),sQuery(id+"F0.wireOp",EDGE,"E2.10.15.0"),sQuery(id+"F0.wireOp",EDGE,"E2.10.16.0"),sQuery(id+"F0.wireOp",EDGE,"E2.10.17.0"),sQuery(id+"F0.wireOp",EDGE,"E2.10.18.0"),sQuery(id+"F0.wireOp",EDGE,"E2.10.19.0"),sQuery(id+"F0.wireOp",EDGE,"E2.10.20.0"),sQuery(id+"F0.wireOp",EDGE,"E2.10.21.0"),sQuery(id+"F0.wireOp",EDGE,"E2.10.22.0"),sQuery(id+"F0.wireOp",EDGE,"E2.10.23.0"),sQuery(id+"F0.wireOp",EDGE,"E2.11.0.0"),sQuery(id+"F0.wireOp",EDGE,"E2.11.1.0"),sQuery(id+"F0.wireOp",EDGE,"E2.11.2.0"),sQuery(id+"F0.wireOp",EDGE,"E2.11.3.0"),sQuery(id+"F0.wireOp",EDGE,"E2.11.4.0"),sQuery(id+"F0.wireOp",EDGE,"E2.11.5.0"),sQuery(id+"F0.wireOp",EDGE,"E2.11.6.0"),sQuery(id+"F0.wireOp",EDGE,"E2.11.7.0"),sQuery(id+"F0.wireOp",EDGE,"E2.11.8.0"),sQuery(id+"F0.wireOp",EDGE,"E2.11.9.0"),sQuery(id+"F0.wireOp",EDGE,"E2.11.10.0"),sQuery(id+"F0.wireOp",EDGE,"E2.11.11.0"),sQuery(id+"F0.wireOp",EDGE,"E2.11.12.0"),sQuery(id+"F0.wireOp",EDGE,"E2.11.13.0"),sQuery(id+"F0.wireOp",EDGE,"E2.11.14.0"),sQuery(id+"F0.wireOp",EDGE,"E2.11.15.0"),sQuery(id+"F0.wireOp",EDGE,"E2.11.16.0"),sQuery(id+"F0.wireOp",EDGE,"E2.11.17.0"),sQuery(id+"F0.wireOp",EDGE,"E2.11.18.0"),sQuery(id+"F0.wireOp",EDGE,"E2.11.19.0"),sQuery(id+"F0.wireOp",EDGE,"E2.11.20.0"),sQuery(id+"F0.wireOp",EDGE,"E2.11.21.0"),sQuery(id+"F0.wireOp",EDGE,"E2.11.22.0"),sQuery(id+"F0.wireOp",EDGE,"E2.11.23.0"),sQuery(id+"F0.wireOp",EDGE,"E2.12.0.0"),sQuery(id+"F0.wireOp",EDGE,"E2.12.1.0"),sQuery(id+"F0.wireOp",EDGE,"E2.12.2.0"),sQuery(id+"F0.wireOp",EDGE,"E2.12.3.0"),sQuery(id+"F0.wireOp",EDGE,"E2.12.4.0"),sQuery(id+"F0.wireOp",EDGE,"E2.12.5.0"),sQuery(id+"F0.wireOp",EDGE,"E2.12.6.0"),sQuery(id+"F0.wireOp",EDGE,"E2.12.7.0"),sQuery(id+"F0.wireOp",EDGE,"E2.12.8.0"),sQuery(id+"F0.wireOp",EDGE,"E2.12.9.0"),sQuery(id+"F0.wireOp",EDGE,"E2.12.10.0"),sQuery(id+"F0.wireOp",EDGE,"E2.12.11.0"),sQuery(id+"F0.wireOp",EDGE,"E2.12.12.0"),sQuery(id+"F0.wireOp",EDGE,"E2.12.13.0"),sQuery(id+"F0.wireOp",EDGE,"E2.12.14.0"),sQuery(id+"F0.wireOp",EDGE,"E2.12.15.0"),sQuery(id+"F0.wireOp",EDGE,"E2.12.16.0"),sQuery(id+"F0.wireOp",EDGE,"E2.12.17.0"),sQuery(id+"F0.wireOp",EDGE,"E2.12.18.0"),sQuery(id+"F0.wireOp",EDGE,"E2.12.19.0"),sQuery(id+"F0.wireOp",EDGE,"E2.12.20.0"),sQuery(id+"F0.wireOp",EDGE,"E2.12.21.0"),sQuery(id+"F0.wireOp",EDGE,"E2.12.22.0"),sQuery(id+"F0.wireOp",EDGE,"E2.12.23.0"),sQuery(id+"F0.wireOp",EDGE,"E2.13.0.0"),sQuery(id+"F0.wireOp",EDGE,"E2.13.1.0"),sQuery(id+"F0.wireOp",EDGE,"E2.13.2.0"),sQuery(id+"F0.wireOp",EDGE,"E2.13.3.0"),sQuery(id+"F0.wireOp",EDGE,"E2.13.4.0"),sQuery(id+"F0.wireOp",EDGE,"E2.13.5.0"),sQuery(id+"F0.wireOp",EDGE,"E2.13.6.0"),sQuery(id+"F0.wireOp",EDGE,"E2.13.7.0"),sQuery(id+"F0.wireOp",EDGE,"E2.13.8.0"),sQuery(id+"F0.wireOp",EDGE,"E2.13.9.0"),sQuery(id+"F0.wireOp",EDGE,"E2.13.10.0"),sQuery(id+"F0.wireOp",EDGE,"E2.13.11.0"),sQuery(id+"F0.wireOp",EDGE,"E2.13.12.0"),sQuery(id+"F0.wireOp",EDGE,"E2.13.13.0"),sQuery(id+"F0.wireOp",EDGE,"E2.13.14.0"),sQuery(id+"F0.wireOp",EDGE,"E2.13.15.0"),sQuery(id+"F0.wireOp",EDGE,"E2.13.16.0"),sQuery(id+"F0.wireOp",EDGE,"E2.13.17.0"),sQuery(id+"F0.wireOp",EDGE,"E2.13.18.0"),sQuery(id+"F0.wireOp",EDGE,"E2.13.19.0"),sQuery(id+"F0.wireOp",EDGE,"E2.13.20.0"),sQuery(id+"F0.wireOp",EDGE,"E2.13.21.0"),sQuery(id+"F0.wireOp",EDGE,"E2.13.22.0"),sQuery(id+"F0.wireOp",EDGE,"E2.13.23.0"),sQuery(id+"F0.wireOp",EDGE,"E2.14.0.0"),sQuery(id+"F0.wireOp",EDGE,"E2.14.1.0"),sQuery(id+"F0.wireOp",EDGE,"E2.14.2.0"),sQuery(id+"F0.wireOp",EDGE,"E2.14.3.0"),sQuery(id+"F0.wireOp",EDGE,"E2.14.4.0"),sQuery(id+"F0.wireOp",EDGE,"E2.14.5.0"),sQuery(id+"F0.wireOp",EDGE,"E2.14.6.0"),sQuery(id+"F0.wireOp",EDGE,"E2.14.7.0"),sQuery(id+"F0.wireOp",EDGE,"E2.14.8.0"),sQuery(id+"F0.wireOp",EDGE,"E2.14.9.0"),sQuery(id+"F0.wireOp",EDGE,"E2.14.10.0"),sQuery(id+"F0.wireOp",EDGE,"E2.14.11.0"),sQuery(id+"F0.wireOp",EDGE,"E2.14.12.0"),sQuery(id+"F0.wireOp",EDGE,"E2.14.13.0"),sQuery(id+"F0.wireOp",EDGE,"E2.14.14.0"),sQuery(id+"F0.wireOp",EDGE,"E2.14.15.0"),sQuery(id+"F0.wireOp",EDGE,"E2.14.16.0"),sQuery(id+"F0.wireOp",EDGE,"E2.14.17.0"),sQuery(id+"F0.wireOp",EDGE,"E2.14.18.0"),sQuery(id+"F0.wireOp",EDGE,"E2.14.19.0"),sQuery(id+"F0.wireOp",EDGE,"E2.14.20.0"),sQuery(id+"F0.wireOp",EDGE,"E2.14.21.0"),sQuery(id+"F0.wireOp",EDGE,"E2.14.22.0"),sQuery(id+"F0.wireOp",EDGE,"E2.14.23.0"),sQuery(id+"F0.wireOp",EDGE,"E2.15.0.0"),sQuery(id+"F0.wireOp",EDGE,"E2.15.1.0"),sQuery(id+"F0.wireOp",EDGE,"E2.15.2.0"),sQuery(id+"F0.wireOp",EDGE,"E2.15.3.0"),sQuery(id+"F0.wireOp",EDGE,"E2.15.4.0"),sQuery(id+"F0.wireOp",EDGE,"E2.15.5.0"),sQuery(id+"F0.wireOp",EDGE,"E2.15.6.0"),sQuery(id+"F0.wireOp",EDGE,"E2.15.7.0"),sQuery(id+"F0.wireOp",EDGE,"E2.15.8.0"),sQuery(id+"F0.wireOp",EDGE,"E2.15.9.0"),sQuery(id+"F0.wireOp",EDGE,"E2.15.10.0"),sQuery(id+"F0.wireOp",EDGE,"E2.15.11.0"),sQuery(id+"F0.wireOp",EDGE,"E2.15.12.0"),sQuery(id+"F0.wireOp",EDGE,"E2.15.13.0"),sQuery(id+"F0.wireOp",EDGE,"E2.15.14.0"),sQuery(id+"F0.wireOp",EDGE,"E2.15.15.0"),sQuery(id+"F0.wireOp",EDGE,"E2.15.16.0"),sQuery(id+"F0.wireOp",EDGE,"E2.15.17.0"),sQuery(id+"F0.wireOp",EDGE,"E2.15.18.0"),sQuery(id+"F0.wireOp",EDGE,"E2.15.19.0"),sQuery(id+"F0.wireOp",EDGE,"E2.15.20.0"),sQuery(id+"F0.wireOp",EDGE,"E2.15.21.0"),sQuery(id+"F0.wireOp",EDGE,"E2.15.22.0"),sQuery(id+"F0.wireOp",EDGE,"E2.15.23.0"),sQuery(id+"F0.wireOp",EDGE,"E2.16.0.0"),sQuery(id+"F0.wireOp",EDGE,"E2.16.1.0"),sQuery(id+"F0.wireOp",EDGE,"E2.16.2.0"),sQuery(id+"F0.wireOp",EDGE,"E2.16.3.0"),sQuery(id+"F0.wireOp",EDGE,"E2.16.4.0"),sQuery(id+"F0.wireOp",EDGE,"E2.16.5.0"),sQuery(id+"F0.wireOp",EDGE,"E2.16.6.0"),sQuery(id+"F0.wireOp",EDGE,"E2.16.7.0"),sQuery(id+"F0.wireOp",EDGE,"E2.16.8.0"),sQuery(id+"F0.wireOp",EDGE,"E2.16.9.0"),sQuery(id+"F0.wireOp",EDGE,"E2.16.10.0"),sQuery(id+"F0.wireOp",EDGE,"E2.16.11.0"),sQuery(id+"F0.wireOp",EDGE,"E2.16.12.0"),sQuery(id+"F0.wireOp",EDGE,"E2.16.13.0"),sQuery(id+"F0.wireOp",EDGE,"E2.16.14.0"),sQuery(id+"F0.wireOp",EDGE,"E2.16.15.0"),sQuery(id+"F0.wireOp",EDGE,"E2.16.16.0"),sQuery(id+"F0.wireOp",EDGE,"E2.16.17.0"),sQuery(id+"F0.wireOp",EDGE,"E2.16.18.0"),sQuery(id+"F0.wireOp",EDGE,"E2.16.19.0"),sQuery(id+"F0.wireOp",EDGE,"E2.16.20.0"),sQuery(id+"F0.wireOp",EDGE,"E2.16.21.0"),sQuery(id+"F0.wireOp",EDGE,"E2.16.22.0"),sQuery(id+"F0.wireOp",EDGE,"E2.16.23.0"),sQuery(id+"F0.wireOp",EDGE,"E2.17.0.0"),sQuery(id+"F0.wireOp",EDGE,"E2.17.1.0"),sQuery(id+"F0.wireOp",EDGE,"E2.17.2.0"),sQuery(id+"F0.wireOp",EDGE,"E2.17.3.0"),sQuery(id+"F0.wireOp",EDGE,"E2.17.4.0"),sQuery(id+"F0.wireOp",EDGE,"E2.17.5.0"),sQuery(id+"F0.wireOp",EDGE,"E2.17.6.0"),sQuery(id+"F0.wireOp",EDGE,"E2.17.7.0"),sQuery(id+"F0.wireOp",EDGE,"E2.17.8.0"),sQuery(id+"F0.wireOp",EDGE,"E2.17.9.0"),sQuery(id+"F0.wireOp",EDGE,"E2.17.10.0"),sQuery(id+"F0.wireOp",EDGE,"E2.17.11.0"),sQuery(id+"F0.wireOp",EDGE,"E2.17.12.0"),sQuery(id+"F0.wireOp",EDGE,"E2.17.13.0"),sQuery(id+"F0.wireOp",EDGE,"E2.17.14.0"),sQuery(id+"F0.wireOp",EDGE,"E2.17.15.0"),sQuery(id+"F0.wireOp",EDGE,"E2.17.16.0"),sQuery(id+"F0.wireOp",EDGE,"E2.17.17.0"),sQuery(id+"F0.wireOp",EDGE,"E2.17.18.0"),sQuery(id+"F0.wireOp",EDGE,"E2.17.19.0"),sQuery(id+"F0.wireOp",EDGE,"E2.17.20.0"),sQuery(id+"F0.wireOp",EDGE,"E2.17.21.0"),sQuery(id+"F0.wireOp",EDGE,"E2.17.22.0"),sQuery(id+"F0.wireOp",EDGE,"E2.17.23.0"),sQuery(id+"F0.wireOp",EDGE,"E2.18.0.0"),sQuery(id+"F0.wireOp",EDGE,"E2.18.1.0"),sQuery(id+"F0.wireOp",EDGE,"E2.18.2.0"),sQuery(id+"F0.wireOp",EDGE,"E2.18.3.0"),sQuery(id+"F0.wireOp",EDGE,"E2.18.4.0"),sQuery(id+"F0.wireOp",EDGE,"E2.18.5.0"),sQuery(id+"F0.wireOp",EDGE,"E2.18.6.0"),sQuery(id+"F0.wireOp",EDGE,"E2.18.7.0"),sQuery(id+"F0.wireOp",EDGE,"E2.18.8.0"),sQuery(id+"F0.wireOp",EDGE,"E2.18.9.0"),sQuery(id+"F0.wireOp",EDGE,"E2.18.10.0"),sQuery(id+"F0.wireOp",EDGE,"E2.18.11.0"),sQuery(id+"F0.wireOp",EDGE,"E2.18.12.0"),sQuery(id+"F0.wireOp",EDGE,"E2.18.13.0"),sQuery(id+"F0.wireOp",EDGE,"E2.18.14.0"),sQuery(id+"F0.wireOp",EDGE,"E2.18.15.0"),sQuery(id+"F0.wireOp",EDGE,"E2.18.16.0"),sQuery(id+"F0.wireOp",EDGE,"E2.18.17.0"),sQuery(id+"F0.wireOp",EDGE,"E2.18.18.0"),sQuery(id+"F0.wireOp",EDGE,"E2.18.19.0"),sQuery(id+"F0.wireOp",EDGE,"E2.18.20.0"),sQuery(id+"F0.wireOp",EDGE,"E2.18.21.0"),sQuery(id+"F0.wireOp",EDGE,"E2.18.22.0"),sQuery(id+"F0.wireOp",EDGE,"E2.18.23.0"),sQuery(id+"F0.wireOp",EDGE,"E2.19.0.0"),sQuery(id+"F0.wireOp",EDGE,"E2.19.1.0"),sQuery(id+"F0.wireOp",EDGE,"E2.19.2.0"),sQuery(id+"F0.wireOp",EDGE,"E2.19.3.0"),sQuery(id+"F0.wireOp",EDGE,"E2.19.4.0"),sQuery(id+"F0.wireOp",EDGE,"E2.19.5.0"),sQuery(id+"F0.wireOp",EDGE,"E2.19.6.0"),sQuery(id+"F0.wireOp",EDGE,"E2.19.7.0"),sQuery(id+"F0.wireOp",EDGE,"E2.19.8.0"),sQuery(id+"F0.wireOp",EDGE,"E2.19.9.0"),sQuery(id+"F0.wireOp",EDGE,"E2.19.10.0"),sQuery(id+"F0.wireOp",EDGE,"E2.19.11.0"),sQuery(id+"F0.wireOp",EDGE,"E2.19.12.0"),sQuery(id+"F0.wireOp",EDGE,"E2.19.13.0"),sQuery(id+"F0.wireOp",EDGE,"E2.19.14.0"),sQuery(id+"F0.wireOp",EDGE,"E2.19.15.0"),sQuery(id+"F0.wireOp",EDGE,"E2.19.16.0"),sQuery(id+"F0.wireOp",EDGE,"E2.19.17.0"),sQuery(id+"F0.wireOp",EDGE,"E2.19.18.0"),sQuery(id+"F0.wireOp",EDGE,"E2.19.19.0"),sQuery(id+"F0.wireOp",EDGE,"E2.19.20.0"),sQuery(id+"F0.wireOp",EDGE,"E2.19.21.0"),sQuery(id+"F0.wireOp",EDGE,"E2.19.22.0"),sQuery(id+"F0.wireOp",EDGE,"E2.19.23.0"),sQuery(id+"F0.wireOp",EDGE,"E2.20.0.0"),sQuery(id+"F0.wireOp",EDGE,"E2.20.1.0"),sQuery(id+"F0.wireOp",EDGE,"E2.20.2.0"),sQuery(id+"F0.wireOp",EDGE,"E2.20.3.0"),sQuery(id+"F0.wireOp",EDGE,"E2.20.4.0"),sQuery(id+"F0.wireOp",EDGE,"E2.20.5.0"),sQuery(id+"F0.wireOp",EDGE,"E2.20.6.0"),sQuery(id+"F0.wireOp",EDGE,"E2.20.7.0"),sQuery(id+"F0.wireOp",EDGE,"E2.20.8.0"),sQuery(id+"F0.wireOp",EDGE,"E2.20.9.0"),sQuery(id+"F0.wireOp",EDGE,"E2.20.10.0"),sQuery(id+"F0.wireOp",EDGE,"E2.20.11.0"),sQuery(id+"F0.wireOp",EDGE,"E2.20.12.0"),sQuery(id+"F0.wireOp",EDGE,"E2.20.13.0"),sQuery(id+"F0.wireOp",EDGE,"E2.20.14.0"),sQuery(id+"F0.wireOp",EDGE,"E2.20.15.0"),sQuery(id+"F0.wireOp",EDGE,"E2.20.16.0"),sQuery(id+"F0.wireOp",EDGE,"E2.20.17.0"),sQuery(id+"F0.wireOp",EDGE,"E2.20.18.0"),sQuery(id+"F0.wireOp",EDGE,"E2.20.19.0"),sQuery(id+"F0.wireOp",EDGE,"E2.20.20.0"),sQuery(id+"F0.wireOp",EDGE,"E2.20.21.0"),sQuery(id+"F0.wireOp",EDGE,"E2.20.22.0"),sQuery(id+"F0.wireOp",EDGE,"E2.20.23.0"),sQuery(id+"F0.wireOp",EDGE,"E2.21.0.0"),sQuery(id+"F0.wireOp",EDGE,"E2.21.1.0"),sQuery(id+"F0.wireOp",EDGE,"E2.21.2.0"),sQuery(id+"F0.wireOp",EDGE,"E2.21.3.0"),sQuery(id+"F0.wireOp",EDGE,"E2.21.4.0"),sQuery(id+"F0.wireOp",EDGE,"E2.21.5.0"),sQuery(id+"F0.wireOp",EDGE,"E2.21.6.0"),sQuery(id+"F0.wireOp",EDGE,"E2.21.7.0"),sQuery(id+"F0.wireOp",EDGE,"E2.21.8.0"),sQuery(id+"F0.wireOp",EDGE,"E2.21.9.0"),sQuery(id+"F0.wireOp",EDGE,"E2.21.10.0"),sQuery(id+"F0.wireOp",EDGE,"E2.21.11.0"),sQuery(id+"F0.wireOp",EDGE,"E2.21.12.0"),sQuery(id+"F0.wireOp",EDGE,"E2.21.13.0"),sQuery(id+"F0.wireOp",EDGE,"E2.21.14.0"),sQuery(id+"F0.wireOp",EDGE,"E2.21.15.0"),sQuery(id+"F0.wireOp",EDGE,"E2.21.16.0"),sQuery(id+"F0.wireOp",EDGE,"E2.21.17.0"),sQuery(id+"F0.wireOp",EDGE,"E2.21.18.0"),sQuery(id+"F0.wireOp",EDGE,"E2.21.19.0"),sQuery(id+"F0.wireOp",EDGE,"E2.21.20.0"),sQuery(id+"F0.wireOp",EDGE,"E2.21.21.0"),sQuery(id+"F0.wireOp",EDGE,"E2.21.22.0"),sQuery(id+"F0.wireOp",EDGE,"E2.21.23.0"),sQuery(id+"F0.wireOp",EDGE,"E2.22.0.0"),sQuery(id+"F0.wireOp",EDGE,"E2.22.1.0"),sQuery(id+"F0.wireOp",EDGE,"E2.22.2.0"),sQuery(id+"F0.wireOp",EDGE,"E2.22.3.0"),sQuery(id+"F0.wireOp",EDGE,"E2.22.4.0"),sQuery(id+"F0.wireOp",EDGE,"E2.22.5.0"),sQuery(id+"F0.wireOp",EDGE,"E2.22.6.0"),sQuery(id+"F0.wireOp",EDGE,"E2.22.7.0"),sQuery(id+"F0.wireOp",EDGE,"E2.22.8.0"),sQuery(id+"F0.wireOp",EDGE,"E2.22.9.0"),sQuery(id+"F0.wireOp",EDGE,"E2.22.10.0"),sQuery(id+"F0.wireOp",EDGE,"E2.22.11.0"),sQuery(id+"F0.wireOp",EDGE,"E2.22.12.0"),sQuery(id+"F0.wireOp",EDGE,"E2.22.13.0"),sQuery(id+"F0.wireOp",EDGE,"E2.22.14.0"),sQuery(id+"F0.wireOp",EDGE,"E2.22.15.0"),sQuery(id+"F0.wireOp",EDGE,"E2.22.16.0"),sQuery(id+"F0.wireOp",EDGE,"E2.22.17.0"),sQuery(id+"F0.wireOp",EDGE,"E2.22.18.0"),sQuery(id+"F0.wireOp",EDGE,"E2.22.19.0"),sQuery(id+"F0.wireOp",EDGE,"E2.22.20.0"),sQuery(id+"F0.wireOp",EDGE,"E2.22.21.0"),sQuery(id+"F0.wireOp",EDGE,"E2.22.22.0"),sQuery(id+"F0.wireOp",EDGE,"E2.22.23.0"),sQuery(id+"F0.wireOp",EDGE,"E2.23.0.0"),sQuery(id+"F0.wireOp",EDGE,"E2.23.1.0"),sQuery(id+"F0.wireOp",EDGE,"E2.23.2.0"),sQuery(id+"F0.wireOp",EDGE,"E2.23.3.0"),sQuery(id+"F0.wireOp",EDGE,"E2.23.4.0"),sQuery(id+"F0.wireOp",EDGE,"E2.23.5.0"),sQuery(id+"F0.wireOp",EDGE,"E2.23.6.0"),sQuery(id+"F0.wireOp",EDGE,"E2.23.7.0"),sQuery(id+"F0.wireOp",EDGE,"E2.23.8.0"),sQuery(id+"F0.wireOp",EDGE,"E2.23.9.0"),sQuery(id+"F0.wireOp",EDGE,"E2.23.10.0"),sQuery(id+"F0.wireOp",EDGE,"E2.23.11.0"),sQuery(id+"F0.wireOp",EDGE,"E2.23.12.0"),sQuery(id+"F0.wireOp",EDGE,"E2.23.13.0"),sQuery(id+"F0.wireOp",EDGE,"E2.23.14.0"),sQuery(id+"F0.wireOp",EDGE,"E2.23.15.0"),sQuery(id+"F0.wireOp",EDGE,"E2.23.16.0"),sQuery(id+"F0.wireOp",EDGE,"E2.23.17.0"),sQuery(id+"F0.wireOp",EDGE,"E2.23.18.0"),sQuery(id+"F0.wireOp",EDGE,"E2.23.19.0"),sQuery(id+"F0.wireOp",EDGE,"E2.23.20.0"),sQuery(id+"F0.wireOp",EDGE,"E2.23.21.0"),sQuery(id+"F0.wireOp",EDGE,"E2.23.22.0"),sQuery(id+"F0.wireOp",EDGE,"E2.23.23.0"),sQuery(id+"F0.wireOp",EDGE,"E2.24.0.0"),sQuery(id+"F0.wireOp",EDGE,"E2.24.1.0"),sQuery(id+"F0.wireOp",EDGE,"E2.24.2.0"),sQuery(id+"F0.wireOp",EDGE,"E2.24.3.0"),sQuery(id+"F0.wireOp",EDGE,"E2.24.4.0"),sQuery(id+"F0.wireOp",EDGE,"E2.24.5.0"),sQuery(id+"F0.wireOp",EDGE,"E2.24.6.0"),sQuery(id+"F0.wireOp",EDGE,"E2.24.7.0"),sQuery(id+"F0.wireOp",EDGE,"E2.24.8.0"),sQuery(id+"F0.wireOp",EDGE,"E2.24.9.0"),sQuery(id+"F0.wireOp",EDGE,"E2.24.10.0"),sQuery(id+"F0.wireOp",EDGE,"E2.24.11.0"),sQuery(id+"F0.wireOp",EDGE,"E2.24.12.0"),sQuery(id+"F0.wireOp",EDGE,"E2.24.13.0"),sQuery(id+"F0.wireOp",EDGE,"E2.24.14.0"),sQuery(id+"F0.wireOp",EDGE,"E2.24.15.0"),sQuery(id+"F0.wireOp",EDGE,"E2.24.16.0"),sQuery(id+"F0.wireOp",EDGE,"E2.24.17.0"),sQuery(id+"F0.wireOp",EDGE,"E2.24.18.0"),sQuery(id+"F0.wireOp",EDGE,"E2.24.19.0"),sQuery(id+"F0.wireOp",EDGE,"E2.24.20.0"),sQuery(id+"F0.wireOp",EDGE,"E2.24.21.0"),sQuery(id+"F0.wireOp",EDGE,"E2.24.22.0"),sQuery(id+"F0.wireOp",EDGE,"E2.24.23.0"),sQuery(id+"F0.wireOp",EDGE,"E2.25.0.0"),sQuery(id+"F0.wireOp",EDGE,"E2.25.1.0"),sQuery(id+"F0.wireOp",EDGE,"E2.25.2.0"),sQuery(id+"F0.wireOp",EDGE,"E2.25.3.0"),sQuery(id+"F0.wireOp",EDGE,"E2.25.4.0"),sQuery(id+"F0.wireOp",EDGE,"E2.25.5.0"),sQuery(id+"F0.wireOp",EDGE,"E2.25.6.0"),sQuery(id+"F0.wireOp",EDGE,"E2.25.7.0"),sQuery(id+"F0.wireOp",EDGE,"E2.25.8.0"),sQuery(id+"F0.wireOp",EDGE,"E2.25.9.0"),sQuery(id+"F0.wireOp",EDGE,"E2.25.10.0"),sQuery(id+"F0.wireOp",EDGE,"E2.25.11.0"),sQuery(id+"F0.wireOp",EDGE,"E2.25.12.0"),sQuery(id+"F0.wireOp",EDGE,"E2.25.13.0"),sQuery(id+"F0.wireOp",EDGE,"E2.25.14.0"),sQuery(id+"F0.wireOp",EDGE,"E2.25.15.0"),sQuery(id+"F0.wireOp",EDGE,"E2.25.16.0"),sQuery(id+"F0.wireOp",EDGE,"E2.25.17.0"),sQuery(id+"F0.wireOp",EDGE,"E2.25.18.0"),sQuery(id+"F0.wireOp",EDGE,"E2.25.19.0"),sQuery(id+"F0.wireOp",EDGE,"E2.25.20.0"),sQuery(id+"F0.wireOp",EDGE,"E2.25.21.0"),sQuery(id+"F0.wireOp",EDGE,"E2.25.22.0"),sQuery(id+"F0.wireOp",EDGE,"E2.25.23.0"),sQuery(id+"F0.wireOp",EDGE,"E2.26.0.0"),sQuery(id+"F0.wireOp",EDGE,"E2.26.1.0"),sQuery(id+"F0.wireOp",EDGE,"E2.26.2.0"),sQuery(id+"F0.wireOp",EDGE,"E2.26.3.0"),sQuery(id+"F0.wireOp",EDGE,"E2.26.4.0"),sQuery(id+"F0.wireOp",EDGE,"E2.26.5.0"),sQuery(id+"F0.wireOp",EDGE,"E2.26.6.0"),sQuery(id+"F0.wireOp",EDGE,"E2.26.7.0"),sQuery(id+"F0.wireOp",EDGE,"E2.26.8.0"),sQuery(id+"F0.wireOp",EDGE,"E2.26.9.0"),sQuery(id+"F0.wireOp",EDGE,"E2.26.10.0"),sQuery(id+"F0.wireOp",EDGE,"E2.26.11.0"),sQuery(id+"F0.wireOp",EDGE,"E2.26.12.0"),sQuery(id+"F0.wireOp",EDGE,"E2.26.13.0"),sQuery(id+"F0.wireOp",EDGE,"E2.26.14.0"),sQuery(id+"F0.wireOp",EDGE,"E2.26.15.0"),sQuery(id+"F0.wireOp",EDGE,"E2.26.16.0"),sQuery(id+"F0.wireOp",EDGE,"E2.26.17.0"),sQuery(id+"F0.wireOp",EDGE,"E2.26.18.0"),sQuery(id+"F0.wireOp",EDGE,"E2.26.19.0"),sQuery(id+"F0.wireOp",EDGE,"E2.26.20.0"),sQuery(id+"F0.wireOp",EDGE,"E2.26.21.0"),sQuery(id+"F0.wireOp",EDGE,"E2.26.22.0"),sQuery(id+"F0.wireOp",EDGE,"E2.26.23.0"),sQuery(id+"F0.wireOp",EDGE,"E2.27.0.0"),sQuery(id+"F0.wireOp",EDGE,"E2.27.1.0"),sQuery(id+"F0.wireOp",EDGE,"E2.27.2.0"),sQuery(id+"F0.wireOp",EDGE,"E2.27.3.0"),sQuery(id+"F0.wireOp",EDGE,"E2.27.4.0"),sQuery(id+"F0.wireOp",EDGE,"E2.27.5.0"),sQuery(id+"F0.wireOp",EDGE,"E2.27.6.0"),sQuery(id+"F0.wireOp",EDGE,"E2.27.7.0"),sQuery(id+"F0.wireOp",EDGE,"E2.27.8.0"),sQuery(id+"F0.wireOp",EDGE,"E2.27.9.0"),sQuery(id+"F0.wireOp",EDGE,"E2.27.10.0"),sQuery(id+"F0.wireOp",EDGE,"E2.27.11.0"),sQuery(id+"F0.wireOp",EDGE,"E2.27.12.0"),sQuery(id+"F0.wireOp",EDGE,"E2.27.13.0"),sQuery(id+"F0.wireOp",EDGE,"E2.27.14.0"),sQuery(id+"F0.wireOp",EDGE,"E2.27.15.0"),sQuery(id+"F0.wireOp",EDGE,"E2.27.16.0"),sQuery(id+"F0.wireOp",EDGE,"E2.27.17.0"),sQuery(id+"F0.wireOp",EDGE,"E2.27.18.0"),sQuery(id+"F0.wireOp",EDGE,"E2.27.19.0"),sQuery(id+"F0.wireOp",EDGE,"E2.27.20.0"),sQuery(id+"F0.wireOp",EDGE,"E2.27.21.0"),sQuery(id+"F0.wireOp",EDGE,"E2.27.22.0"),sQuery(id+"F0.wireOp",EDGE,"E2.27.23.0"),sQuery(id+"F0.wireOp",EDGE,"E2.28.0.0"),sQuery(id+"F0.wireOp",EDGE,"E2.28.1.0"),sQuery(id+"F0.wireOp",EDGE,"E2.28.2.0"),sQuery(id+"F0.wireOp",EDGE,"E2.28.3.0"),sQuery(id+"F0.wireOp",EDGE,"E2.28.4.0"),sQuery(id+"F0.wireOp",EDGE,"E2.28.5.0"),sQuery(id+"F0.wireOp",EDGE,"E2.28.6.0"),sQuery(id+"F0.wireOp",EDGE,"E2.28.7.0"),sQuery(id+"F0.wireOp",EDGE,"E2.28.8.0"),sQuery(id+"F0.wireOp",EDGE,"E2.28.9.0"),sQuery(id+"F0.wireOp",EDGE,"E2.28.10.0"),sQuery(id+"F0.wireOp",EDGE,"E2.28.11.0"),sQuery(id+"F0.wireOp",EDGE,"E2.28.12.0"),sQuery(id+"F0.wireOp",EDGE,"E2.28.13.0"),sQuery(id+"F0.wireOp",EDGE,"E2.28.14.0"),sQuery(id+"F0.wireOp",EDGE,"E2.28.15.0"),sQuery(id+"F0.wireOp",EDGE,"E2.28.16.0"),sQuery(id+"F0.wireOp",EDGE,"E2.28.17.0"),sQuery(id+"F0.wireOp",EDGE,"E2.28.18.0"),sQuery(id+"F0.wireOp",EDGE,"E2.28.19.0"),sQuery(id+"F0.wireOp",EDGE,"E2.28.20.0"),sQuery(id+"F0.wireOp",EDGE,"E2.28.21.0"),sQuery(id+"F0.wireOp",EDGE,"E2.28.22.0"),sQuery(id+"F0.wireOp",EDGE,"E2.28.23.0"),sQuery(id+"F0.wireOp",EDGE,"E2.29.0.0"),sQuery(id+"F0.wireOp",EDGE,"E2.29.1.0"),sQuery(id+"F0.wireOp",EDGE,"E2.29.2.0"),sQuery(id+"F0.wireOp",EDGE,"E2.29.3.0"),sQuery(id+"F0.wireOp",EDGE,"E2.29.4.0"),sQuery(id+"F0.wireOp",EDGE,"E2.29.5.0"),sQuery(id+"F0.wireOp",EDGE,"E2.29.6.0"),sQuery(id+"F0.wireOp",EDGE,"E2.29.7.0"),sQuery(id+"F0.wireOp",EDGE,"E2.29.8.0"),sQuery(id+"F0.wireOp",EDGE,"E2.29.9.0"),sQuery(id+"F0.wireOp",EDGE,"E2.29.10.0"),sQuery(id+"F0.wireOp",EDGE,"E2.29.11.0"),sQuery(id+"F0.wireOp",EDGE,"E2.29.12.0"),sQuery(id+"F0.wireOp",EDGE,"E2.29.13.0"),sQuery(id+"F0.wireOp",EDGE,"E2.29.14.0"),sQuery(id+"F0.wireOp",EDGE,"E2.29.15.0"),sQuery(id+"F0.wireOp",EDGE,"E2.29.16.0"),sQuery(id+"F0.wireOp",EDGE,"E2.29.17.0"),sQuery(id+"F0.wireOp",EDGE,"E2.29.18.0"),sQuery(id+"F0.wireOp",EDGE,"E2.29.19.0"),sQuery(id+"F0.wireOp",EDGE,"E2.29.20.0"),sQuery(id+"F0.wireOp",EDGE,"E2.29.21.0"),sQuery(id+"F0.wireOp",EDGE,"E2.29.22.0"),sQuery(id+"F0.wireOp",EDGE,"E2.29.23.0"),sQuery(id+"F0.wireOp",EDGE,"E2.30.0.0"),sQuery(id+"F0.wireOp",EDGE,"E2.30.1.0"),sQuery(id+"F0.wireOp",EDGE,"E2.30.2.0"),sQuery(id+"F0.wireOp",EDGE,"E2.30.3.0"),sQuery(id+"F0.wireOp",EDGE,"E2.30.4.0"),sQuery(id+"F0.wireOp",EDGE,"E2.30.5.0"),sQuery(id+"F0.wireOp",EDGE,"E2.30.6.0"),sQuery(id+"F0.wireOp",EDGE,"E2.30.7.0"),sQuery(id+"F0.wireOp",EDGE,"E2.30.8.0"),sQuery(id+"F0.wireOp",EDGE,"E2.30.9.0"),sQuery(id+"F0.wireOp",EDGE,"E2.30.10.0"),sQuery(id+"F0.wireOp",EDGE,"E2.30.11.0"),sQuery(id+"F0.wireOp",EDGE,"E2.30.12.0"),sQuery(id+"F0.wireOp",EDGE,"E2.30.13.0"),sQuery(id+"F0.wireOp",EDGE,"E2.30.14.0"),sQuery(id+"F0.wireOp",EDGE,"E2.30.15.0"),sQuery(id+"F0.wireOp",EDGE,"E2.30.16.0"),sQuery(id+"F0.wireOp",EDGE,"E2.30.17.0"),sQuery(id+"F0.wireOp",EDGE,"E2.30.18.0"),sQuery(id+"F0.wireOp",EDGE,"E2.30.19.0"),sQuery(id+"F0.wireOp",EDGE,"E2.30.20.0"),sQuery(id+"F0.wireOp",EDGE,"E2.30.21.0"),sQuery(id+"F0.wireOp",EDGE,"E2.30.22.0"),sQuery(id+"F0.wireOp",EDGE,"E2.30.23.0"),sQuery(id+"F0.wireOp",EDGE,"E2.31.0.0"),sQuery(id+"F0.wireOp",EDGE,"E2.31.1.0"),sQuery(id+"F0.wireOp",EDGE,"E2.31.2.0"),sQuery(id+"F0.wireOp",EDGE,"E2.31.3.0"),sQuery(id+"F0.wireOp",EDGE,"E2.31.4.0"),sQuery(id+"F0.wireOp",EDGE,"E2.31.5.0"),sQuery(id+"F0.wireOp",EDGE,"E2.31.6.0"),sQuery(id+"F0.wireOp",EDGE,"E2.31.7.0"),sQuery(id+"F0.wireOp",EDGE,"E2.31.8.0"),sQuery(id+"F0.wireOp",EDGE,"E2.31.9.0"),sQuery(id+"F0.wireOp",EDGE,"E2.31.10.0"),sQuery(id+"F0.wireOp",EDGE,"E2.31.11.0"),sQuery(id+"F0.wireOp",EDGE,"E2.31.12.0"),sQuery(id+"F0.wireOp",EDGE,"E2.31.13.0"),sQuery(id+"F0.wireOp",EDGE,"E2.31.14.0"),sQuery(id+"F0.wireOp",EDGE,"E2.31.15.0"),sQuery(id+"F0.wireOp",EDGE,"E2.31.16.0"),sQuery(id+"F0.wireOp",EDGE,"E2.31.17.0"),sQuery(id+"F0.wireOp",EDGE,"E2.31.18.0"),sQuery(id+"F0.wireOp",EDGE,"E2.31.19.0"),sQuery(id+"F0.wireOp",EDGE,"E2.31.20.0"),sQuery(id+"F0.wireOp",EDGE,"E2.31.21.0"),sQuery(id+"F0.wireOp",EDGE,"E2.31.22.0"),sQuery(id+"F0.wireOp",EDGE,"E2.31.23.0"),sQuery(id+"F0.wireOp",EDGE,"E2.32.0.0"),sQuery(id+"F0.wireOp",EDGE,"E2.32.1.0"),sQuery(id+"F0.wireOp",EDGE,"E2.32.2.0"),sQuery(id+"F0.wireOp",EDGE,"E2.32.3.0"),sQuery(id+"F0.wireOp",EDGE,"E2.32.4.0"),sQuery(id+"F0.wireOp",EDGE,"E2.32.5.0"),sQuery(id+"F0.wireOp",EDGE,"E2.32.6.0"),sQuery(id+"F0.wireOp",EDGE,"E2.32.7.0"),sQuery(id+"F0.wireOp",EDGE,"E2.32.8.0"),sQuery(id+"F0.wireOp",EDGE,"E2.32.9.0"),sQuery(id+"F0.wireOp",EDGE,"E2.32.10.0"),sQuery(id+"F0.wireOp",EDGE,"E2.32.11.0"),sQuery(id+"F0.wireOp",EDGE,"E2.32.12.0"),sQuery(id+"F0.wireOp",EDGE,"E2.32.13.0"),sQuery(id+"F0.wireOp",EDGE,"E2.32.14.0"),sQuery(id+"F0.wireOp",EDGE,"E2.32.15.0"),sQuery(id+"F0.wireOp",EDGE,"E2.32.16.0"),sQuery(id+"F0.wireOp",EDGE,"E2.32.17.0"),sQuery(id+"F0.wireOp",EDGE,"E2.32.18.0"),sQuery(id+"F0.wireOp",EDGE,"E2.32.19.0"),sQuery(id+"F0.wireOp",EDGE,"E2.32.20.0"),sQuery(id+"F0.wireOp",EDGE,"E2.32.21.0"),sQuery(id+"F0.wireOp",EDGE,"E2.32.22.0"),sQuery(id+"F0.wireOp",EDGE,"E2.32.23.0"),sQuery(id+"F0.wireOp",EDGE,"E2.33.0.0"),sQuery(id+"F0.wireOp",EDGE,"E2.33.1.0"),sQuery(id+"F0.wireOp",EDGE,"E2.33.2.0"),sQuery(id+"F0.wireOp",EDGE,"E2.33.3.0"),sQuery(id+"F0.wireOp",EDGE,"E2.33.4.0"),sQuery(id+"F0.wireOp",EDGE,"E2.33.5.0"),sQuery(id+"F0.wireOp",EDGE,"E2.33.6.0"),sQuery(id+"F0.wireOp",EDGE,"E2.33.7.0"),sQuery(id+"F0.wireOp",EDGE,"E2.33.8.0"),sQuery(id+"F0.wireOp",EDGE,"E2.33.9.0"),sQuery(id+"F0.wireOp",EDGE,"E2.33.10.0"),sQuery(id+"F0.wireOp",EDGE,"E2.33.11.0"),sQuery(id+"F0.wireOp",EDGE,"E2.33.12.0"),sQuery(id+"F0.wireOp",EDGE,"E2.33.13.0"),sQuery(id+"F0.wireOp",EDGE,"E2.33.14.0"),sQuery(id+"F0.wireOp",EDGE,"E2.33.15.0"),sQuery(id+"F0.wireOp",EDGE,"E2.33.16.0"),sQuery(id+"F0.wireOp",EDGE,"E2.33.17.0"),sQuery(id+"F0.wireOp",EDGE,"E2.33.18.0"),sQuery(id+"F0.wireOp",EDGE,"E2.33.19.0"),sQuery(id+"F0.wireOp",EDGE,"E2.33.20.0"),sQuery(id+"F0.wireOp",EDGE,"E2.33.21.0"),sQuery(id+"F0.wireOp",EDGE,"E2.33.22.0"),sQuery(id+"F0.wireOp",EDGE,"E2.33.23.0"),sQuery(id+"F0.wireOp",EDGE,"E2.34.0.0"),sQuery(id+"F0.wireOp",EDGE,"E2.34.1.0"),sQuery(id+"F0.wireOp",EDGE,"E2.34.2.0"),sQuery(id+"F0.wireOp",EDGE,"E2.34.3.0"),sQuery(id+"F0.wireOp",EDGE,"E2.34.4.0"),sQuery(id+"F0.wireOp",EDGE,"E2.34.5.0"),sQuery(id+"F0.wireOp",EDGE,"E2.34.6.0"),sQuery(id+"F0.wireOp",EDGE,"E2.34.7.0"),sQuery(id+"F0.wireOp",EDGE,"E2.34.8.0"),sQuery(id+"F0.wireOp",EDGE,"E2.34.9.0"),sQuery(id+"F0.wireOp",EDGE,"E2.34.10.0"),sQuery(id+"F0.wireOp",EDGE,"E2.34.11.0"),sQuery(id+"F0.wireOp",EDGE,"E2.34.12.0"),sQuery(id+"F0.wireOp",EDGE,"E2.34.13.0"),sQuery(id+"F0.wireOp",EDGE,"E2.34.14.0"),sQuery(id+"F0.wireOp",EDGE,"E2.34.15.0"),sQuery(id+"F0.wireOp",EDGE,"E2.34.16.0"),sQuery(id+"F0.wireOp",EDGE,"E2.34.17.0"),sQuery(id+"F0.wireOp",EDGE,"E2.34.18.0"),sQuery(id+"F0.wireOp",EDGE,"E2.34.19.0"),sQuery(id+"F0.wireOp",EDGE,"E2.34.20.0"),sQuery(id+"F0.wireOp",EDGE,"E2.34.21.0"),sQuery(id+"F0.wireOp",EDGE,"E2.34.22.0"),sQuery(id+"F0.wireOp",EDGE,"E2.34.23.0"),sQuery(id+"F0.wireOp",EDGE,"E3.0.35.0"),sQuery(id+"F0.wireOp",EDGE,"E3.0.35.1"),sQuery(id+"F0.wireOp",EDGE,"E3.0.35.2"),sQuery(id+"F0.wireOp",EDGE,"E3.0.35.3"),sQuery(id+"F0.wireOp",EDGE,"E3.0.35.4"),sQuery(id+"F0.wireOp",EDGE,"E3.0.35.5"),sQuery(id+"F0.wireOp",EDGE,"E3.0.35.6"),sQuery(id+"F0.wireOp",EDGE,"E3.0.35.7"),sQuery(id+"F0.wireOp",EDGE,"E3.0.35.8"),sQuery(id+"F0.wireOp",EDGE,"E3.0.35.9"),sQuery(id+"F0.wireOp",EDGE,"E3.0.35.10"),sQuery(id+"F0.wireOp",EDGE,"E3.0.35.11"),sQuery(id+"F0.wireOp",EDGE,"E3.0.35.12"),sQuery(id+"F0.wireOp",EDGE,"E3.0.35.13"),sQuery(id+"F0.wireOp",EDGE,"E3.0.35.14"),sQuery(id+"F0.wireOp",EDGE,"E3.0.35.15"),sQuery(id+"F0.wireOp",EDGE,"E3.0.35.16"),sQuery(id+"F0.wireOp",EDGE,"E3.0.35.17"),sQuery(id+"F0.wireOp",EDGE,"E3.0.35.18"),sQuery(id+"F0.wireOp",EDGE,"E3.0.35.19"),sQuery(id+"F0.wireOp",EDGE,"E3.0.35.20"),sQuery(id+"F0.wireOp",EDGE,"E3.0.35.21"),sQuery(id+"F0.wireOp",EDGE,"E3.0.35.22"),sQuery(id+"F0.wireOp",EDGE,"E3.0.35.23"),sQuery(id+"F0.wireOp",EDGE,"E3.0.36.0"),sQuery(id+"F0.wireOp",EDGE,"E3.0.36.1"),sQuery(id+"F0.wireOp",EDGE,"E3.0.36.2"),sQuery(id+"F0.wireOp",EDGE,"E3.0.36.3"),sQuery(id+"F0.wireOp",EDGE,"E3.0.36.4"),sQuery(id+"F0.wireOp",EDGE,"E3.0.36.5"),sQuery(id+"F0.wireOp",EDGE,"E3.0.36.6"),sQuery(id+"F0.wireOp",EDGE,"E3.0.36.7"),sQuery(id+"F0.wireOp",EDGE,"E3.0.36.8"),sQuery(id+"F0.wireOp",EDGE,"E3.0.36.9"),sQuery(id+"F0.wireOp",EDGE,"E3.0.36.10"),sQuery(id+"F0.wireOp",EDGE,"E3.0.36.11"),sQuery(id+"F0.wireOp",EDGE,"E3.0.36.12"),sQuery(id+"F0.wireOp",EDGE,"E3.0.36.13"),sQuery(id+"F0.wireOp",EDGE,"E3.0.36.14"),sQuery(id+"F0.wireOp",EDGE,"E3.0.36.15"),sQuery(id+"F0.wireOp",EDGE,"E3.0.36.16"),sQuery(id+"F0.wireOp",EDGE,"E3.0.36.17"),sQuery(id+"F0.wireOp",EDGE,"E3.0.36.18"),sQuery(id+"F0.wireOp",EDGE,"E3.0.36.19"),sQuery(id+"F0.wireOp",EDGE,"E3.0.36.20"),sQuery(id+"F0.wireOp",EDGE,"E3.0.36.21"),sQuery(id+"F0.wireOp",EDGE,"E3.0.36.22"),sQuery(id+"F0.wireOp",EDGE,"E3.0.36.23"),sQuery(id+"F0.wireOp",EDGE,"E4.0.0.24"),sQuery(id+"F0.wireOp",EDGE,"E4.0.1.24"),sQuery(id+"F0.wireOp",EDGE,"E4.0.2.24"),sQuery(id+"F0.wireOp",EDGE,"E4.0.3.24"),sQuery(id+"F0.wireOp",EDGE,"E4.0.4.24"),sQuery(id+"F0.wireOp",EDGE,"E4.0.5.24"),sQuery(id+"F0.wireOp",EDGE,"E4.0.6.24"),sQuery(id+"F0.wireOp",EDGE,"E4.0.7.24"),sQuery(id+"F0.wireOp",EDGE,"E4.0.8.24"),sQuery(id+"F0.wireOp",EDGE,"E4.0.9.24"),sQuery(id+"F0.wireOp",EDGE,"E4.0.10.24"),sQuery(id+"F0.wireOp",EDGE,"E4.0.11.24"),sQuery(id+"F0.wireOp",EDGE,"E4.0.12.24"),sQuery(id+"F0.wireOp",EDGE,"E4.0.13.24"),sQuery(id+"F0.wireOp",EDGE,"E4.0.14.24"),sQuery(id+"F0.wireOp",EDGE,"E4.0.15.24"),sQuery(id+"F0.wireOp",EDGE,"E4.0.16.24"),sQuery(id+"F0.wireOp",EDGE,"E4.0.17.24"),sQuery(id+"F0.wireOp",EDGE,"E4.0.18.24"),sQuery(id+"F0.wireOp",EDGE,"E4.0.19.24"),sQuery(id+"F0.wireOp",EDGE,"E4.0.20.24"),sQuery(id+"F0.wireOp",EDGE,"E4.0.21.24"),sQuery(id+"F0.wireOp",EDGE,"E4.0.22.24"),sQuery(id+"F0.wireOp",EDGE,"E4.0.23.24"),sQuery(id+"F0.wireOp",EDGE,"E4.0.24.24"),sQuery(id+"F0.wireOp",EDGE,"E4.0.25.24"),sQuery(id+"F0.wireOp",EDGE,"E4.0.26.24"),sQuery(id+"F0.wireOp",EDGE,"E4.0.27.24"),sQuery(id+"F0.wireOp",EDGE,"E4.0.28.24"),sQuery(id+"F0.wireOp",EDGE,"E4.0.29.24"),sQuery(id+"F0.wireOp",EDGE,"E4.0.30.24"),sQuery(id+"F0.wireOp",EDGE,"E4.0.31.24"),sQuery(id+"F0.wireOp",EDGE,"E4.0.32.24"),sQuery(id+"F0.wireOp",EDGE,"E4.0.33.24"),sQuery(id+"F0.wireOp",EDGE,"E4.0.34.24"),sQuery(id+"F0.wireOp",EDGE,"E4.0.35.24"),sQuery(id+"F0.wireOp",EDGE,"E4.0.36.24")])],"isStart":true}),makeQuery(id+"F2.opExtrude","CAP_FACE",FACE,{"disambiguationData":[OSD([subQ3,subQ2,subQ1,subQ0,sQuery(id+"F0.wireOp",EDGE,"E5.bottom"),sQuery(id+"F0.wireOp",EDGE,"E5.top"),sQuery(id+"F0.wireOp",EDGE,"E5.left"),sQuery(id+"F0.wireOp",EDGE,"E5.right")])],"isStart":true})]});}
            var sketch = newSketch(context, id + "F3", { "sketchPlane" : qUnion([Q0])});
            skLineSegment(sketch, "E6.bottom", {"start": v(-151.05, 117.74) * mm, "end": v(228.95, 117.74) * mm});
            skLineSegment(sketch, "E6.top", {"start": v(-151.05, 126.74) * mm, "end": v(228.95, 126.74) * mm});
            skLineSegment(sketch, "E6.left", {"start": v(-151.05, 117.74) * mm, "end": v(-151.05, 126.74) * mm});
            skLineSegment(sketch, "E6.right", {"start": v(228.95, 117.74) * mm, "end": v(228.95, 126.74) * mm});
            skSolve(sketch);
        }
        {
            var Q0;
            {var subQ0=sQuery(id+"F3.wireOp",EDGE,"E6.bottom");Q0=makeQuery(id+"F3.imprint","IMPRINT",FACE,{"disambiguationData":[TD([[makeQuery(id+"F3.imprint","IMPRINT",EDGE,{"derivedFrom":subQ0}),1.0]])]});}
            var Q1;
            {var subQ0=sQuery(id+"F3.wireOp",EDGE,"E6.top");Q1=makeQuery(id+"F3.imprint","IMPRINT",FACE,{"disambiguationData":[TD([[makeQuery(id+"F3.imprint","IMPRINT",EDGE,{"derivedFrom":subQ0}),-1.0]])]});}
            extrude(context, id + "F4", {"entities" : qUnion([Q0, Q1]), "depth" : 50 * mm, "offsetDistance" : 25 * mm});
        }
        {
            var Q0;
            {var subQ0=sQuery(id+"F3.wireOp",EDGE,"E6.top");Q0=makeQuery(id+"F3.imprint","IMPRINT",FACE,{"disambiguationData":[TD([[makeQuery(id+"F3.imprint","IMPRINT",EDGE,{"derivedFrom":subQ0}),-1.0]])]});}
            var Q1;
            Q1=makeQuery(id+"F2.opExtrude","CAP_FACE",FACE,{"disambiguationData":[OSD([sQuery(id+"F0.wireOp",EDGE,"E0.bottom"),sQuery(id+"F0.wireOp",EDGE,"E0.top"),sQuery(id+"F0.wireOp",EDGE,"E0.left"),sQuery(id+"F0.wireOp",EDGE,"E0.right"),sQuery(id+"F0.wireOp",EDGE,"E5.bottom"),sQuery(id+"F0.wireOp",EDGE,"E5.top"),sQuery(id+"F0.wireOp",EDGE,"E5.left"),sQuery(id+"F0.wireOp",EDGE,"E5.right")])],"isStart":false});
            extrude(context, id + "F5", {"entities" : qUnion([Q0]), "operationType" : NewBodyOperationType.ADD, "endBound" : BoundingType.UP_TO_SURFACE, "oppositeDirection" : true, "depth" : 25 * mm, "endBoundEntityFace" : qUnion([Q1]), "offsetDistance" : 25 * mm});
        }
        {
            var Q0;
            {var subQ0=sQuery(id+"F3.wireOp",EDGE,"E6.right");Q0=makeQuery(id+"F5.boolean.opBoolean","MERGE",FACE,{"derivedFrom":[makeQuery(id+"F4.opExtrude","SWEPT_FACE",FACE,{"disambiguationData":[OSD([subQ0])]}),makeQuery(id+"F5.opExtrude","SWEPT_FACE",FACE,{"disambiguationData":[OSD([subQ0])]})]});}
            var sketch = newSketch(context, id + "F6", { "sketchPlane" : qUnion([Q0])});
            skLineSegment(sketch, "E7.bottom", {"start": v(-126.74, 4) * mm, "end": v(143.26, 4) * mm});
            skLineSegment(sketch, "E7.top", {"start": v(-126.74, -50) * mm, "end": v(143.26, -50) * mm});
            skLineSegment(sketch, "E7.left", {"start": v(-126.74, 4) * mm, "end": v(-126.74, -50) * mm});
            skLineSegment(sketch, "E7.right", {"start": v(143.26, 4) * mm, "end": v(143.26, -50) * mm});
            skLineSegment(sketch, "E8.0", {"start": v(-121.74, 0) * mm, "end": v(138.26, 0) * mm});
            skLineSegment(sketch, "E9.0", {"start": v(138.26, 4) * mm, "end": v(138.26, 0) * mm});
            skLineSegment(sketch, "E10.0", {"start": v(-121.74, 4) * mm, "end": v(-121.74, 0) * mm});
            skLineSegment(sketch, "E11.0", {"start": v(-117.74, -50) * mm, "end": v(-117.74, 0) * mm});
            skLineSegment(sketch, "E12", {"start": v(134.26, 0) * mm, "end": v(134.26, -50) * mm});
            skSolve(sketch);
        }
        {
            var Q0;
            {var subQ0=sQuery(id+"F6.wireOp",EDGE,"E11.0");Q0=makeQuery(id+"F6.imprint","IMPRINT",FACE,{"disambiguationData":[TD([[makeQuery(id+"F6.imprint","IMPRINT",EDGE,{"derivedFrom":subQ0}),-1.0]])]});}
            extrude(context, id + "F7", {"entities" : qUnion([Q0]), "oppositeDirection" : true, "depth" : 4 * mm, "offsetDistance" : 25 * mm});
        }
        {
            var Q0;
            {var subQ0=sQuery(id+"F6.wireOp",EDGE,"E11.0");Q0=makeQuery(id+"F6.imprint","IMPRINT",FACE,{"disambiguationData":[TD([[makeQuery(id+"F6.imprint","IMPRINT",EDGE,{"derivedFrom":subQ0}),-1.0]])]});}
            var Q1;
            {var subQ4=sQuery(id+"F6.wireOp",EDGE,"E7.left");Q1=makeQuery(id+"F6.imprint","IMPRINT",FACE,{"disambiguationData":[TD([[makeQuery(id+"F6.imprint","IMPRINT",EDGE,{"derivedFrom":subQ4}),-1.0]])]});}
            var Q2;
            {var subQ4=sQuery(id+"F6.wireOp",EDGE,"E9.0");Q2=makeQuery(id+"F6.imprint","IMPRINT",FACE,{"disambiguationData":[TD([[makeQuery(id+"F6.imprint","IMPRINT",EDGE,{"derivedFrom":subQ4}),-1.0]])]});}
            var Q3;
            {var subQ3=sQuery(id+"F6.wireOp",EDGE,"E7.right");Q3=makeQuery(id+"F6.imprint","IMPRINT",FACE,{"disambiguationData":[TD([[makeQuery(id+"F6.imprint","IMPRINT",EDGE,{"derivedFrom":subQ3}),-1.0]])]});}
            extrude(context, id + "F8", {"entities" : qUnion([Q0, Q1, Q2, Q3]), "operationType" : NewBodyOperationType.ADD, "depth" : 5 * mm, "offsetDistance" : 25 * mm});
        }
        {
            var Q0;
            Q0=makeQuery(id+"F4.opExtrude","CAP_FACE",FACE,{"disambiguationData":[OSD([sQuery(id+"F3.wireOp",EDGE,"E6.bottom"),sQuery(id+"F3.wireOp",EDGE,"E6.top"),sQuery(id+"F3.wireOp",EDGE,"E6.left"),sQuery(id+"F3.wireOp",EDGE,"E6.right")])],"isStart":false});
            var sketch = newSketch(context, id + "F9", { "sketchPlane" : qUnion([Q0])});
            skLineSegment(sketch, "E13.bottom", {"start": v(233.95, 126.74) * mm, "end": v(-156.05, 126.74) * mm});
            skLineSegment(sketch, "E13.top", {"start": v(233.95, -143.26) * mm, "end": v(-156.05, -143.26) * mm});
            skLineSegment(sketch, "E13.left", {"start": v(233.95, 126.74) * mm, "end": v(233.95, -143.26) * mm});
            skLineSegment(sketch, "E13.right", {"start": v(-156.05, 126.74) * mm, "end": v(-156.05, -143.26) * mm});
            skSolve(sketch);
        }
        {
            var Q0;
            Q0=makeQuery(id+"F9.imprint","IMPRINT",FACE,{"disambiguationData":[TD([[makeQuery(id+"F9.imprint","IMPRINT",EDGE,{"derivedFrom":makeQuery(id+"F4.opExtrude","CAP_EDGE",EDGE,{"disambiguationData":[OSD([sQuery(id+"F3.wireOp",EDGE,"E6.bottom")])],"isStart":false})}),1.0]])]});
            var Q1;
            Q1=makeQuery(id+"F9.imprint","IMPRINT",FACE,{"disambiguationData":[TD([[makeQuery(id+"F9.imprint","IMPRINT",EDGE,{"derivedFrom":sQuery(id+"F9.wireOp",EDGE,"E13.top")}),-1.0]])]});
            extrude(context, id + "F10", {"entities" : qUnion([Q0, Q1]), "depth" : 5 * mm, "offsetDistance" : 25 * mm});
        }
        {
            var Q0;
            Q0=makeQuery(id+"F10.opExtrude","CAP_FACE",FACE,{"disambiguationData":[OSD([sQuery(id+"F9.wireOp",EDGE,"E13.bottom"),sQuery(id+"F9.wireOp",EDGE,"E13.top"),sQuery(id+"F9.wireOp",EDGE,"E13.left"),sQuery(id+"F9.wireOp",EDGE,"E13.right")])],"isStart":true});
            var sketch = newSketch(context, id + "F11", { "sketchPlane" : qUnion([Q0])});
            skLineSegment(sketch, "E14.0", {"start": v(-147.05, -117.74) * mm, "end": v(-147.05, 134.26) * mm});
            skLineSegment(sketch, "E14.1", {"start": v(-147.05, -117.74) * mm, "end": v(224.95, -117.74) * mm});
            skLineSegment(sketch, "E14.2", {"start": v(224.95, -117.74) * mm, "end": v(224.95, 134.26) * mm});
            skLineSegment(sketch, "E14.3", {"start": v(224.95, 134.26) * mm, "end": v(-147.05, 134.26) * mm});
            skSolve(sketch);
        }
        {
            var Q0;
            Q0=makeQuery(id+"F11.imprint","IMPRINT",FACE,{"disambiguationData":[TD([[makeQuery(id+"F11.imprint","IMPRINT",EDGE,{"derivedFrom":sQuery(id+"F11.wireOp",EDGE,"E14.0")}),-1.0]])]});
            extrude(context, id + "F12", {"entities" : qUnion([Q0]), "operationType" : NewBodyOperationType.ADD, "depth" : 4 * mm, "offsetDistance" : 25 * mm});
        }
        {
            var Q0;
            Q0=makeQuery(id+"F10.opExtrude","CAP_FACE",FACE,{"disambiguationData":[OSD([sQuery(id+"F9.wireOp",EDGE,"E13.bottom"),sQuery(id+"F9.wireOp",EDGE,"E13.top"),sQuery(id+"F9.wireOp",EDGE,"E13.left"),sQuery(id+"F9.wireOp",EDGE,"E13.right")])],"isStart":false});
            var sketch = newSketch(context, id + "F13", { "sketchPlane" : qUnion([Q0])});
            skLineSegment(sketch, "E15", {"start": v(38.95, 126.74) * mm, "end": v(38.95, -143.26) * mm, "construction": true});
            skPoint(sketch, "E15.startSnap0", {"position": v(38.95, 126.74) * mm});
            skCircle(sketch, "E16", {"center": v(38.95, -8.26) * mm, "radius": 20 * mm});
            skLineSegment(sketch, "E17.0.0", {"start": v(233.95, 126.74) * mm, "end": v(-156.05, 126.74) * mm});
            skLineSegment(sketch, "E17.0.1", {"start": v(-156.05, 126.74) * mm, "end": v(-156.05, -143.26) * mm});
            skLineSegment(sketch, "E17.0.2", {"start": v(-156.05, -143.26) * mm, "end": v(233.95, -143.26) * mm});
            skLineSegment(sketch, "E17.0.3", {"start": v(233.95, -143.26) * mm, "end": v(233.95, 126.74) * mm});
            skSolve(sketch);
        }
        {
            var Q0;
            Q0=makeQuery(id+"F13.imprint","IMPRINT",FACE,{"disambiguationData":[TD([[makeQuery(id+"F13.imprint","IMPRINT",EDGE,{"derivedFrom":sQuery(id+"F13.wireOp",EDGE,"E16")}),1.0]])]});
            extrude(context, id + "F14", {"entities" : qUnion([Q0]), "operationType" : NewBodyOperationType.REMOVE, "oppositeDirection" : true, "depth" : 25 * mm, "offsetDistance" : 25 * mm});
        }
        {
            var Q0;
            Q0=makeQuery(id+"F8.opExtrude","CAP_FACE",FACE,{"disambiguationData":[OSD([sQuery(id+"F6.wireOp",EDGE,"E7.bottom"),sQuery(id+"F6.wireOp",EDGE,"E7.top"),sQuery(id+"F6.wireOp",EDGE,"E7.left"),sQuery(id+"F6.wireOp",EDGE,"E7.right")])],"isStart":false});
            var sketch = newSketch(context, id + "F15", { "sketchPlane" : qUnion([Q0])});
            skLineSegment(sketch, "E18", {"start": v(8.26, 4) * mm, "end": v(8.26, -50) * mm, "construction": true});
            skCircle(sketch, "E19", {"center": v(-6.74, -30) * mm, "radius": 1.5 * mm});
            skCircle(sketch, "E20", {"center": v(23.26, -30) * mm, "radius": 1.5 * mm});
            skCircle(sketch, "E21", {"center": v(23.26, -45) * mm, "radius": 1.5 * mm});
            skCircle(sketch, "E22", {"center": v(-6.74, -45) * mm, "radius": 1.5 * mm});
            skLineSegment(sketch, "E23", {"start": v(-6.74, -30) * mm, "end": v(8.26, -30) * mm, "construction": true});
            skLineSegment(sketch, "E24", {"start": v(8.26, -30) * mm, "end": v(23.26, -30) * mm, "construction": true});
            skSolve(sketch);
        }
        {
            var Q0;
            Q0=makeQuery(id+"F15.imprint","IMPRINT",FACE,{"disambiguationData":[TD([[makeQuery(id+"F15.imprint","IMPRINT",EDGE,{"derivedFrom":sQuery(id+"F15.wireOp",EDGE,"E22")}),1.0]])]});
            var Q1;
            Q1=makeQuery(id+"F15.imprint","IMPRINT",FACE,{"disambiguationData":[TD([[makeQuery(id+"F15.imprint","IMPRINT",EDGE,{"derivedFrom":sQuery(id+"F15.wireOp",EDGE,"E19")}),1.0]])]});
            var Q2;
            Q2=makeQuery(id+"F15.imprint","IMPRINT",FACE,{"disambiguationData":[TD([[makeQuery(id+"F15.imprint","IMPRINT",EDGE,{"derivedFrom":sQuery(id+"F15.wireOp",EDGE,"E20")}),1.0]])]});
            var Q3;
            Q3=makeQuery(id+"F15.imprint","IMPRINT",FACE,{"disambiguationData":[TD([[makeQuery(id+"F15.imprint","IMPRINT",EDGE,{"derivedFrom":sQuery(id+"F15.wireOp",EDGE,"E21")}),1.0]])]});
            extrude(context, id + "F16", {"entities" : qUnion([Q0, Q1, Q2, Q3]), "operationType" : NewBodyOperationType.REMOVE, "oppositeDirection" : true, "depth" : 25 * mm, "offsetDistance" : 25 * mm});
        }
        {
            var Q0;
            {var subQ0=sQuery(id+"F3.wireOp",EDGE,"E6.top");Q0=makeQuery(id+"F5.boolean.opBoolean","MERGE",FACE,{"derivedFrom":[makeQuery(id+"F4.opExtrude","SWEPT_FACE",FACE,{"disambiguationData":[OSD([subQ0])]}),makeQuery(id+"F5.opExtrude","SWEPT_FACE",FACE,{"disambiguationData":[OSD([subQ0])]})]});}
            var sketch = newSketch(context, id + "F17", { "sketchPlane" : qUnion([Q0])});
            skLineSegment(sketch, "E25", {"start": v(38.95, 4) * mm, "end": v(38.95, -50) * mm, "construction": true});
            skCircle(sketch, "E26", {"center": v(23.95, -30) * mm, "radius": 1.5 * mm});
            skCircle(sketch, "E27", {"center": v(53.95, -30) * mm, "radius": 1.5 * mm});
            skCircle(sketch, "E28", {"center": v(53.95, -45) * mm, "radius": 1.5 * mm});
            skCircle(sketch, "E29", {"center": v(23.95, -45) * mm, "radius": 1.5 * mm});
            skLineSegment(sketch, "E30", {"start": v(23.95, -30) * mm, "end": v(38.95, -30) * mm, "construction": true});
            skLineSegment(sketch, "E31", {"start": v(38.95, -30) * mm, "end": v(53.95, -30) * mm, "construction": true});
            skSolve(sketch);
        }
        {
            var Q0;
            Q0=makeQuery(id+"F17.imprint","IMPRINT",FACE,{"disambiguationData":[TD([[makeQuery(id+"F17.imprint","IMPRINT",EDGE,{"derivedFrom":sQuery(id+"F17.wireOp",EDGE,"E26")}),1.0]])]});
            var Q1;
            Q1=makeQuery(id+"F17.imprint","IMPRINT",FACE,{"disambiguationData":[TD([[makeQuery(id+"F17.imprint","IMPRINT",EDGE,{"derivedFrom":sQuery(id+"F17.wireOp",EDGE,"E27")}),1.0]])]});
            var Q2;
            Q2=makeQuery(id+"F17.imprint","IMPRINT",FACE,{"disambiguationData":[TD([[makeQuery(id+"F17.imprint","IMPRINT",EDGE,{"derivedFrom":sQuery(id+"F17.wireOp",EDGE,"E28")}),1.0]])]});
            var Q3;
            Q3=makeQuery(id+"F17.imprint","IMPRINT",FACE,{"disambiguationData":[TD([[makeQuery(id+"F17.imprint","IMPRINT",EDGE,{"derivedFrom":sQuery(id+"F17.wireOp",EDGE,"E29")}),1.0]])]});
            extrude(context, id + "F18", {"entities" : qUnion([Q0, Q1, Q2, Q3]), "operationType" : NewBodyOperationType.REMOVE, "oppositeDirection" : true, "depth" : 25 * mm, "offsetDistance" : 25 * mm});
        }
        {
            var Q0;
            Q0=makeQuery(id+"F8.opExtrude","CAP_FACE",FACE,{"disambiguationData":[OSD([sQuery(id+"F6.wireOp",EDGE,"E7.bottom"),sQuery(id+"F6.wireOp",EDGE,"E7.top"),sQuery(id+"F6.wireOp",EDGE,"E7.left"),sQuery(id+"F6.wireOp",EDGE,"E7.right")])],"isStart":false});
            var sketch = newSketch(context, id + "F19", { "sketchPlane" : qUnion([Q0])});
            skLineSegment(sketch, "E32.bottom", {"start": v(29.76, -55) * mm, "end": v(-13.24, -55) * mm});
            skLineSegment(sketch, "E32.top", {"start": v(29.76, -25.5) * mm, "end": v(-13.24, -25.5) * mm});
            skLineSegment(sketch, "E32.left", {"start": v(29.76, -55) * mm, "end": v(29.76, -25.5) * mm});
            skLineSegment(sketch, "E32.right", {"start": v(-13.24, -55) * mm, "end": v(-13.24, -25.5) * mm});
            skCircle(sketch, "E33.0", {"center": v(23.26, -45) * mm, "radius": 1.5 * mm});
            skCircle(sketch, "E34.0", {"center": v(23.26, -30) * mm, "radius": 1.5 * mm});
            skCircle(sketch, "E35.0", {"center": v(-6.74, -30) * mm, "radius": 1.5 * mm});
            skCircle(sketch, "E36.0", {"center": v(-6.74, -45) * mm, "radius": 1.5 * mm});
            skSolve(sketch);
        }
        {
            var Q0;
            Q0=makeQuery(id+"F19.imprint","IMPRINT",FACE,{"disambiguationData":[TD([[makeQuery(id+"F19.imprint","IMPRINT",EDGE,{"derivedFrom":sQuery(id+"F19.wireOp",EDGE,"E32.bottom")}),-1.0]])]});
            var Q1;
            {var subQ1=sQuery(id+"F19.wireOp",EDGE,"E32.top");Q1=makeQuery(id+"F19.imprint","IMPRINT",FACE,{"disambiguationData":[TD([[makeQuery(id+"F19.imprint","IMPRINT",EDGE,{"derivedFrom":subQ1}),1.0]])]});}
            extrude(context, id + "F20", {"entities" : qUnion([Q0, Q1]), "depth" : 4 * mm, "offsetDistance" : 25 * mm});
        }
        {
            var Q0;
            Q0=makeQuery(id+"F20.opExtrude","SWEPT_FACE",FACE,{"disambiguationData":[OSD([sQuery(id+"F19.wireOp",EDGE,"E32.bottom")])]});
            var sketch = newSketch(context, id + "F21", { "sketchPlane" : qUnion([Q0])});
            skCircle(sketch, "E37", {"center": v(243.95, -8.26) * mm, "radius": 7.6 * mm});
            skLineSegment(sketch, "E38", {"start": v(237.95, -8.26) * mm, "end": v(243.95, -8.26) * mm, "construction": true});
            skCircle(sketch, "E39", {"center": v(243.95, -8.26) * mm, "radius": 10.6 * mm});
            skLineSegment(sketch, "E40", {"start": v(243.95, 2.34) * mm, "end": v(237.95, 2.34) * mm});
            skLineSegment(sketch, "E41", {"start": v(243.95, -18.86) * mm, "end": v(237.95, -18.86) * mm});
            skLineSegment(sketch, "E42", {"start": v(256.55, -5.26) * mm, "end": v(256.55, -11.26) * mm});
            skLineSegment(sketch, "E43", {"start": v(243.95, -8.26) * mm, "end": v(256.55, -8.26) * mm, "construction": true});
            skLineSegment(sketch, "E44", {"start": v(256.55, -5.26) * mm, "end": v(254.12, -5.26) * mm});
            skLineSegment(sketch, "E45", {"start": v(256.55, -11.26) * mm, "end": v(254.12, -11.26) * mm});
            skSolve(sketch);
        }
        {
            var Q0;
            {var subQ0=sQuery(id+"F21.wireOp",EDGE,"E40");Q0=makeQuery(id+"F21.imprint","IMPRINT",FACE,{"disambiguationData":[TD([[makeQuery(id+"F21.imprint","IMPRINT",EDGE,{"derivedFrom":subQ0}),1.0]])]});}
            var Q1;
            {var subQ3=makeQuery(id+"F20.opExtrude","CAP_EDGE",EDGE,{"disambiguationData":[OSD([sQuery(id+"F19.wireOp",EDGE,"E32.top")])],"isStart":false});var subQ6=sQuery(id+"F21.wireOp",EDGE,"E37");var subQ7=makeQuery(id+"F21.imprint","INTERSECT",VERTEX,{"disambiguationData":[OD(0.0)],"derivedFrom":[subQ3,subQ6]});Q1=makeQuery(id+"F21.imprint","IMPRINT",FACE,{"disambiguationData":[TD([[makeQuery(id+"F21.imprint","IMPRINT",EDGE,{"disambiguationData":[TD([[subQ7,1.0]])],"derivedFrom":subQ6}),-1.0]])]});}
            var Q2;
            {var subQ0=sQuery(id+"F21.wireOp",EDGE,"E41");Q2=makeQuery(id+"F21.imprint","IMPRINT",FACE,{"disambiguationData":[TD([[makeQuery(id+"F21.imprint","IMPRINT",EDGE,{"derivedFrom":subQ0}),-1.0]])]});}
            var Q3;
            {var subQ0=sQuery(id+"F21.wireOp",EDGE,"hvNTzypy-dMNU-H1L7-wxFu-QFGx7FczOX4K");Q3=makeQuery(id+"F21.imprint","IMPRINT",FACE,{"disambiguationData":[TD([[makeQuery(id+"F21.imprint","IMPRINT",EDGE,{"derivedFrom":subQ0}),-1.0]])]});}
            var Q4;
            Q4=makeQuery(id+"F21.imprint","IMPRINT",FACE,{"disambiguationData":[TD([[makeQuery(id+"F21.imprint","IMPRINT",EDGE,{"derivedFrom":sQuery(id+"F21.wireOp",EDGE,"E42")}),-1.0]])]});
            extrude(context, id + "F22", {"entities" : qUnion([Q0, Q1, Q2, Q3, Q4]), "operationType" : NewBodyOperationType.ADD, "oppositeDirection" : true, "depth" : 24 * mm, "offsetDistance" : 25 * mm});
        }
        {
            var Q0;
            {var subQ0=sQuery(id+"F21.wireOp",EDGE,"E37");var subQ1=makeQuery(id+"F20.opExtrude","CAP_EDGE",EDGE,{"disambiguationData":[OSD([sQuery(id+"F19.wireOp",EDGE,"E32.top")])],"isStart":false});var subQ2=makeQuery(id+"F21.imprint","INTERSECT",VERTEX,{"disambiguationData":[OD(0.0)],"derivedFrom":[subQ1,subQ0]});Q0=makeQuery(id+"F21.imprint","IMPRINT",FACE,{"disambiguationData":[TD([[makeQuery(id+"F21.imprint","IMPRINT",EDGE,{"disambiguationData":[TD([[subQ2,-1.0]])],"derivedFrom":subQ0}),1.0]])]});}
            extrude(context, id + "F23", {"entities" : qUnion([Q0]), "operationType" : NewBodyOperationType.REMOVE, "oppositeDirection" : true, "depth" : 24 * mm, "offsetDistance" : 25 * mm});
        }
        {
            var Q0;
            {var subQ0=sQuery(id+"F19.wireOp",EDGE,"E32.bottom");Q0=makeQuery(id+"F22.boolean.opBoolean","MERGE",FACE,{"derivedFrom":[makeQuery(id+"F20.opExtrude","SWEPT_FACE",FACE,{"disambiguationData":[OSD([subQ0])]}),makeQuery(id+"F22.opExtrude","CAP_FACE",FACE,{"disambiguationData":[OSD([subQ0,sQuery(id+"F21.wireOp",EDGE,"E37"),sQuery(id+"F21.wireOp",EDGE,"E39"),sQuery(id+"F21.wireOp",EDGE,"E40"),sQuery(id+"F21.wireOp",EDGE,"E41")])],"isStart":true})]});}
            var sketch = newSketch(context, id + "F24", { "sketchPlane" : qUnion([Q0])});
            skCircle(sketch, "E46.0", {"center": v(243.95, -8.26) * mm, "radius": 7.6 * mm});
            skCircle(sketch, "E47", {"center": v(243.95, -8.26) * mm, "radius": 7.5 * mm});
            skCircle(sketch, "E48", {"center": v(243.95, -8.26) * mm, "radius": 4 * mm});
            skSolve(sketch);
        }
        {
            var Q0;
            Q0=makeQuery(id+"F24.imprint","IMPRINT",FACE,{"disambiguationData":[TD([[makeQuery(id+"F24.imprint","IMPRINT",EDGE,{"derivedFrom":sQuery(id+"F24.wireOp",EDGE,"E47")}),1.0]])]});
            extrude(context, id + "F25", {"entities" : qUnion([Q0]), "oppositeDirection" : true, "depth" : 24 * mm, "offsetDistance" : 25 * mm});
        }
        {
            var Q0;
            Q0=makeQuery(id+"F22.opExtrude","SWEPT_FACE",FACE,{"disambiguationData":[OSD([sQuery(id+"F21.wireOp",EDGE,"E45")])]});
            cPlane(context, id + "F26", {"entities" : qUnion([Q0]), "cplaneType" : CPlaneType.OFFSET, "offset" : 5 * mm, "width" : 150 * mm, "height" : 150 * mm});
        }
        {
            var Q0;
            Q0=qCreatedBy(id+"F26.planeOp",FACE);
            var sketch = newSketch(context, id + "F27", { "sketchPlane" : qUnion([Q0])});
            skLineSegment(sketch, "E49.0", {"start": v(-256.55, -31) * mm, "end": v(-256.55, -55) * mm});
            skLineSegment(sketch, "E50.0", {"start": v(-256.55, -55) * mm, "end": v(-254.12, -55) * mm});
            skLineSegment(sketch, "E51.0", {"start": v(-256.55, -31) * mm, "end": v(-254.12, -31) * mm});
            skLineSegment(sketch, "E52.0", {"start": v(-254.12, -31) * mm, "end": v(-254.12, -55) * mm});
            skLineSegment(sketch, "E53.bottom", {"start": v(-254.12, -53) * mm, "end": v(-252.62, -53) * mm});
            skLineSegment(sketch, "E53.top", {"start": v(-254.12, -49.5) * mm, "end": v(-252.62, -49.5) * mm});
            skLineSegment(sketch, "E53.left", {"start": v(-254.12, -53) * mm, "end": v(-254.12, -49.5) * mm});
            skLineSegment(sketch, "E53.right", {"start": v(-252.62, -53) * mm, "end": v(-252.62, -49.5) * mm});
            skLineSegment(sketch, "E54.bottom", {"start": v(-254.12, -47.5) * mm, "end": v(-252.62, -47.5) * mm});
            skLineSegment(sketch, "E54.top", {"start": v(-254.12, -44) * mm, "end": v(-252.62, -44) * mm});
            skLineSegment(sketch, "E54.left", {"start": v(-254.12, -47.5) * mm, "end": v(-254.12, -44) * mm});
            skLineSegment(sketch, "E54.right", {"start": v(-252.62, -47.5) * mm, "end": v(-252.62, -44) * mm});
            skLineSegment(sketch, "E55.bottom", {"start": v(-254.12, -42) * mm, "end": v(-252.62, -42) * mm});
            skLineSegment(sketch, "E55.top", {"start": v(-254.12, -38.5) * mm, "end": v(-252.62, -38.5) * mm});
            skLineSegment(sketch, "E55.left", {"start": v(-254.12, -42) * mm, "end": v(-254.12, -38.5) * mm});
            skLineSegment(sketch, "E55.right", {"start": v(-252.62, -42) * mm, "end": v(-252.62, -38.5) * mm});
            skLineSegment(sketch, "E56.bottom", {"start": v(-254.12, -36.5) * mm, "end": v(-252.62, -36.5) * mm});
            skLineSegment(sketch, "E56.top", {"start": v(-254.12, -33) * mm, "end": v(-252.62, -33) * mm});
            skLineSegment(sketch, "E56.left", {"start": v(-254.12, -36.5) * mm, "end": v(-254.12, -33) * mm});
            skLineSegment(sketch, "E56.right", {"start": v(-252.62, -36.5) * mm, "end": v(-252.62, -33) * mm});
            skSolve(sketch);
        }
        {
            var Q0;
            Q0=makeQuery(id+"F27.imprint","IMPRINT",FACE,{"disambiguationData":[TD([[makeQuery(id+"F27.imprint","IMPRINT",EDGE,{"derivedFrom":sQuery(id+"F27.wireOp",EDGE,"E53.bottom")}),1.0]])]});
            var Q1;
            Q1=makeQuery(id+"F27.imprint","IMPRINT",FACE,{"disambiguationData":[TD([[makeQuery(id+"F27.imprint","IMPRINT",EDGE,{"derivedFrom":sQuery(id+"F27.wireOp",EDGE,"E54.bottom")}),1.0]])]});
            var Q2;
            Q2=makeQuery(id+"F27.imprint","IMPRINT",FACE,{"disambiguationData":[TD([[makeQuery(id+"F27.imprint","IMPRINT",EDGE,{"derivedFrom":sQuery(id+"F27.wireOp",EDGE,"E55.bottom")}),1.0]])]});
            var Q3;
            Q3=makeQuery(id+"F27.imprint","IMPRINT",FACE,{"disambiguationData":[TD([[makeQuery(id+"F27.imprint","IMPRINT",EDGE,{"derivedFrom":sQuery(id+"F27.wireOp",EDGE,"E56.bottom")}),1.0]])]});
            extrude(context, id + "F28", {"entities" : qUnion([Q0, Q1, Q2, Q3]), "operationType" : NewBodyOperationType.REMOVE, "oppositeDirection" : true, "depth" : 25 * mm, "offsetDistance" : 25 * mm});
        }
        {
            var Q0;
            Q0=makeQuery(id+"F22.opExtrude","SWEPT_EDGE",EDGE,{"disambiguationData":[OSD([sQuery(id+"F21.wireOp",EDGE,"E42"),sQuery(id+"F21.wireOp",EDGE,"E45")])]});
            var Q1;
            Q1=makeQuery(id+"F22.opExtrude","SWEPT_EDGE",EDGE,{"disambiguationData":[OSD([sQuery(id+"F21.wireOp",EDGE,"E42"),sQuery(id+"F21.wireOp",EDGE,"E44")])]});
            var Q2;
            {var subQ0=sQuery(id+"F21.wireOp",EDGE,"E45");Q2=makeQuery(id+"F28.boolean.opBoolean","SPLIT",EDGE,{"disambiguationData":[topologyDisambiguationEdgeConnected([makeQuery(id+"F22.opExtrude","SWEPT_FACE",FACE,{"disambiguationData":[OSD([subQ0])]}),makeQuery(id+"F28.opExtrude","SWEPT_FACE",FACE,{"disambiguationData":[OSD([sQuery(id+"F27.wireOp",EDGE,"E53.left")])]})])],"derivedFrom":makeQuery(id+"F22.opExtrude","SWEPT_EDGE",EDGE,{"disambiguationData":[OSD([sQuery(id+"F21.wireOp",EDGE,"E39"),subQ0])]})});}
            var Q3;
            {var subQ0=sQuery(id+"F21.wireOp",EDGE,"E45");Q3=makeQuery(id+"F28.boolean.opBoolean","SPLIT",EDGE,{"disambiguationData":[topologyDisambiguationEdgeConnected([makeQuery(id+"F22.opExtrude","SWEPT_FACE",FACE,{"disambiguationData":[OSD([subQ0])]}),makeQuery(id+"F28.opExtrude","SWEPT_FACE",FACE,{"disambiguationData":[OSD([sQuery(id+"F27.wireOp",EDGE,"E54.left")])]})])],"derivedFrom":makeQuery(id+"F22.opExtrude","SWEPT_EDGE",EDGE,{"disambiguationData":[OSD([sQuery(id+"F21.wireOp",EDGE,"E39"),subQ0])]})});}
            var Q4;
            {var subQ0=sQuery(id+"F21.wireOp",EDGE,"E45");Q4=makeQuery(id+"F28.boolean.opBoolean","SPLIT",EDGE,{"disambiguationData":[topologyDisambiguationEdgeConnected([makeQuery(id+"F22.opExtrude","SWEPT_FACE",FACE,{"disambiguationData":[OSD([subQ0])]}),makeQuery(id+"F28.opExtrude","SWEPT_FACE",FACE,{"disambiguationData":[OSD([sQuery(id+"F27.wireOp",EDGE,"E55.left")])]})])],"derivedFrom":makeQuery(id+"F22.opExtrude","SWEPT_EDGE",EDGE,{"disambiguationData":[OSD([sQuery(id+"F21.wireOp",EDGE,"E39"),subQ0])]})});}
            var Q5;
            {var subQ0=sQuery(id+"F21.wireOp",EDGE,"E45");Q5=makeQuery(id+"F28.boolean.opBoolean","SPLIT",EDGE,{"disambiguationData":[topologyDisambiguationEdgeConnected([makeQuery(id+"F22.opExtrude","SWEPT_FACE",FACE,{"disambiguationData":[OSD([subQ0])]}),makeQuery(id+"F28.opExtrude","SWEPT_FACE",FACE,{"disambiguationData":[OSD([sQuery(id+"F27.wireOp",EDGE,"E56.left")])]})])],"derivedFrom":makeQuery(id+"F22.opExtrude","SWEPT_EDGE",EDGE,{"disambiguationData":[OSD([sQuery(id+"F21.wireOp",EDGE,"E39"),subQ0])]})});}
            var Q6;
            {var subQ0=sQuery(id+"F21.wireOp",EDGE,"E39");Q6=makeQuery(id+"F28.boolean.opBoolean","INTERSECT",EDGE,{"derivedFrom":[makeQuery(id+"F22.opExtrude","SWEPT_FACE",FACE,{"disambiguationData":[OSD([subQ0]),TDD([makeQuery(id+"F21.imprint","IMPRINT",EDGE,{"disambiguationData":[TD([[makeQuery(id+"F21.imprint","INTERSECT",VERTEX,{"derivedFrom":[subQ0,sQuery(id+"F21.wireOp",EDGE,"E41")]}),-1.0]])],"derivedFrom":subQ0})])]}),makeQuery(id+"F28.opExtrude","SWEPT_FACE",FACE,{"disambiguationData":[OSD([sQuery(id+"F27.wireOp",EDGE,"E53.right")])]})]});}
            var Q7;
            {var subQ0=sQuery(id+"F21.wireOp",EDGE,"E39");Q7=makeQuery(id+"F28.boolean.opBoolean","INTERSECT",EDGE,{"derivedFrom":[makeQuery(id+"F22.opExtrude","SWEPT_FACE",FACE,{"disambiguationData":[OSD([subQ0]),TDD([makeQuery(id+"F21.imprint","IMPRINT",EDGE,{"disambiguationData":[TD([[makeQuery(id+"F21.imprint","INTERSECT",VERTEX,{"derivedFrom":[subQ0,sQuery(id+"F21.wireOp",EDGE,"E41")]}),-1.0]])],"derivedFrom":subQ0})])]}),makeQuery(id+"F28.opExtrude","SWEPT_FACE",FACE,{"disambiguationData":[OSD([sQuery(id+"F27.wireOp",EDGE,"E54.right")])]})]});}
            var Q8;
            {var subQ0=sQuery(id+"F21.wireOp",EDGE,"E39");Q8=makeQuery(id+"F28.boolean.opBoolean","INTERSECT",EDGE,{"derivedFrom":[makeQuery(id+"F22.opExtrude","SWEPT_FACE",FACE,{"disambiguationData":[OSD([subQ0]),TDD([makeQuery(id+"F21.imprint","IMPRINT",EDGE,{"disambiguationData":[TD([[makeQuery(id+"F21.imprint","INTERSECT",VERTEX,{"derivedFrom":[subQ0,sQuery(id+"F21.wireOp",EDGE,"E41")]}),-1.0]])],"derivedFrom":subQ0})])]}),makeQuery(id+"F28.opExtrude","SWEPT_FACE",FACE,{"disambiguationData":[OSD([sQuery(id+"F27.wireOp",EDGE,"E55.right")])]})]});}
            var Q9;
            {var subQ0=sQuery(id+"F21.wireOp",EDGE,"E39");Q9=makeQuery(id+"F28.boolean.opBoolean","INTERSECT",EDGE,{"derivedFrom":[makeQuery(id+"F22.opExtrude","SWEPT_FACE",FACE,{"disambiguationData":[OSD([subQ0]),TDD([makeQuery(id+"F21.imprint","IMPRINT",EDGE,{"disambiguationData":[TD([[makeQuery(id+"F21.imprint","INTERSECT",VERTEX,{"derivedFrom":[subQ0,sQuery(id+"F21.wireOp",EDGE,"E41")]}),-1.0]])],"derivedFrom":subQ0})])]}),makeQuery(id+"F28.opExtrude","SWEPT_FACE",FACE,{"disambiguationData":[OSD([sQuery(id+"F27.wireOp",EDGE,"E56.right")])]})]});}
            var Q10;
            {var subQ0=sQuery(id+"F21.wireOp",EDGE,"E44");Q10=makeQuery(id+"F28.boolean.opBoolean","SPLIT",EDGE,{"disambiguationData":[topologyDisambiguationEdgeConnected([makeQuery(id+"F22.opExtrude","SWEPT_FACE",FACE,{"disambiguationData":[OSD([subQ0])]}),makeQuery(id+"F28.opExtrude","SWEPT_FACE",FACE,{"disambiguationData":[OSD([sQuery(id+"F27.wireOp",EDGE,"E53.left")])]})])],"derivedFrom":makeQuery(id+"F22.opExtrude","SWEPT_EDGE",EDGE,{"disambiguationData":[OSD([sQuery(id+"F21.wireOp",EDGE,"E39"),subQ0])]})});}
            var Q11;
            {var subQ0=sQuery(id+"F21.wireOp",EDGE,"E44");Q11=makeQuery(id+"F28.boolean.opBoolean","SPLIT",EDGE,{"disambiguationData":[topologyDisambiguationEdgeConnected([makeQuery(id+"F22.opExtrude","SWEPT_FACE",FACE,{"disambiguationData":[OSD([subQ0])]}),makeQuery(id+"F28.opExtrude","SWEPT_FACE",FACE,{"disambiguationData":[OSD([sQuery(id+"F27.wireOp",EDGE,"E54.left")])]})])],"derivedFrom":makeQuery(id+"F22.opExtrude","SWEPT_EDGE",EDGE,{"disambiguationData":[OSD([sQuery(id+"F21.wireOp",EDGE,"E39"),subQ0])]})});}
            var Q12;
            {var subQ0=sQuery(id+"F21.wireOp",EDGE,"E44");Q12=makeQuery(id+"F28.boolean.opBoolean","SPLIT",EDGE,{"disambiguationData":[topologyDisambiguationEdgeConnected([makeQuery(id+"F22.opExtrude","SWEPT_FACE",FACE,{"disambiguationData":[OSD([subQ0])]}),makeQuery(id+"F28.opExtrude","SWEPT_FACE",FACE,{"disambiguationData":[OSD([sQuery(id+"F27.wireOp",EDGE,"E55.left")])]})])],"derivedFrom":makeQuery(id+"F22.opExtrude","SWEPT_EDGE",EDGE,{"disambiguationData":[OSD([sQuery(id+"F21.wireOp",EDGE,"E39"),subQ0])]})});}
            var Q13;
            {var subQ0=sQuery(id+"F21.wireOp",EDGE,"E44");Q13=makeQuery(id+"F28.boolean.opBoolean","SPLIT",EDGE,{"disambiguationData":[topologyDisambiguationEdgeConnected([makeQuery(id+"F22.opExtrude","SWEPT_FACE",FACE,{"disambiguationData":[OSD([subQ0])]}),makeQuery(id+"F28.opExtrude","SWEPT_FACE",FACE,{"disambiguationData":[OSD([sQuery(id+"F27.wireOp",EDGE,"E56.left")])]})])],"derivedFrom":makeQuery(id+"F22.opExtrude","SWEPT_EDGE",EDGE,{"disambiguationData":[OSD([sQuery(id+"F21.wireOp",EDGE,"E39"),subQ0])]})});}
            var Q14;
            {var subQ0=sQuery(id+"F21.wireOp",EDGE,"E39");Q14=makeQuery(id+"F28.boolean.opBoolean","INTERSECT",EDGE,{"derivedFrom":[makeQuery(id+"F22.opExtrude","SWEPT_FACE",FACE,{"disambiguationData":[OSD([subQ0]),TDD([makeQuery(id+"F21.imprint","IMPRINT",EDGE,{"disambiguationData":[TD([[makeQuery(id+"F21.imprint","INTERSECT",VERTEX,{"derivedFrom":[subQ0,sQuery(id+"F21.wireOp",EDGE,"E40")]}),1.0]])],"derivedFrom":subQ0})])]}),makeQuery(id+"F28.opExtrude","SWEPT_FACE",FACE,{"disambiguationData":[OSD([sQuery(id+"F27.wireOp",EDGE,"E56.right")])]})]});}
            var Q15;
            {var subQ0=sQuery(id+"F21.wireOp",EDGE,"E39");Q15=makeQuery(id+"F28.boolean.opBoolean","INTERSECT",EDGE,{"derivedFrom":[makeQuery(id+"F22.opExtrude","SWEPT_FACE",FACE,{"disambiguationData":[OSD([subQ0]),TDD([makeQuery(id+"F21.imprint","IMPRINT",EDGE,{"disambiguationData":[TD([[makeQuery(id+"F21.imprint","INTERSECT",VERTEX,{"derivedFrom":[subQ0,sQuery(id+"F21.wireOp",EDGE,"E40")]}),1.0]])],"derivedFrom":subQ0})])]}),makeQuery(id+"F28.opExtrude","SWEPT_FACE",FACE,{"disambiguationData":[OSD([sQuery(id+"F27.wireOp",EDGE,"E55.right")])]})]});}
            var Q16;
            {var subQ0=sQuery(id+"F21.wireOp",EDGE,"E39");Q16=makeQuery(id+"F28.boolean.opBoolean","INTERSECT",EDGE,{"derivedFrom":[makeQuery(id+"F22.opExtrude","SWEPT_FACE",FACE,{"disambiguationData":[OSD([subQ0]),TDD([makeQuery(id+"F21.imprint","IMPRINT",EDGE,{"disambiguationData":[TD([[makeQuery(id+"F21.imprint","INTERSECT",VERTEX,{"derivedFrom":[subQ0,sQuery(id+"F21.wireOp",EDGE,"E40")]}),1.0]])],"derivedFrom":subQ0})])]}),makeQuery(id+"F28.opExtrude","SWEPT_FACE",FACE,{"disambiguationData":[OSD([sQuery(id+"F27.wireOp",EDGE,"E54.right")])]})]});}
            var Q17;
            {var subQ0=sQuery(id+"F21.wireOp",EDGE,"E39");Q17=makeQuery(id+"F28.boolean.opBoolean","INTERSECT",EDGE,{"derivedFrom":[makeQuery(id+"F22.opExtrude","SWEPT_FACE",FACE,{"disambiguationData":[OSD([subQ0]),TDD([makeQuery(id+"F21.imprint","IMPRINT",EDGE,{"disambiguationData":[TD([[makeQuery(id+"F21.imprint","INTERSECT",VERTEX,{"derivedFrom":[subQ0,sQuery(id+"F21.wireOp",EDGE,"E40")]}),1.0]])],"derivedFrom":subQ0})])]}),makeQuery(id+"F28.opExtrude","SWEPT_FACE",FACE,{"disambiguationData":[OSD([sQuery(id+"F27.wireOp",EDGE,"E53.right")])]})]});}
            fillet(context, id + "F29", {"entities" : qUnion([Q0, Q1, Q2, Q3, Q4, Q5, Q6, Q7, Q8, Q9, Q10, Q11, Q12, Q13, Q14, Q15, Q16, Q17]), "radius" : 1 * mm, "tangentPropagation" : true, "allowEdgeOverflow" : false});
        }
        {
            var Q0;
            Q0=makeQuery(id+"F8.opExtrude","CAP_FACE",FACE,{"disambiguationData":[OSD([sQuery(id+"F6.wireOp",EDGE,"E7.bottom"),sQuery(id+"F6.wireOp",EDGE,"E7.top"),sQuery(id+"F6.wireOp",EDGE,"E7.left"),sQuery(id+"F6.wireOp",EDGE,"E7.right")])],"isStart":false});
            var sketch = newSketch(context, id + "F30", { "sketchPlane" : qUnion([Q0])});
            skLineSegment(sketch, "E57.bottom", {"start": v(-43.24, -25.5) * mm, "end": v(-88.24, -25.5) * mm});
            skLineSegment(sketch, "E57.left", {"start": v(-43.24, -25.5) * mm, "end": v(-43.24, -55) * mm});
            skLineSegment(sketch, "E58", {"start": v(-88.24, -25.5) * mm, "end": v(-88.24, -55) * mm});
            skLineSegment(sketch, "E59", {"start": v(-88.24, -55) * mm, "end": v(-43.24, -55) * mm});
            skCircle(sketch, "E60", {"center": v(-83.24, -30.5) * mm, "radius": 1.5 * mm});
            skCircle(sketch, "E61", {"center": v(-48.24, -30.5) * mm, "radius": 1.5 * mm});
            skCircle(sketch, "E62", {"center": v(-48.24, -45) * mm, "radius": 1.5 * mm});
            skCircle(sketch, "E63", {"center": v(-83.24, -45) * mm, "radius": 1.5 * mm});
            skSolve(sketch);
        }
        {
            var Q0;
            Q0=makeQuery(id+"F30.imprint","IMPRINT",FACE,{"disambiguationData":[TD([[makeQuery(id+"F30.imprint","IMPRINT",EDGE,{"derivedFrom":sQuery(id+"F30.wireOp",EDGE,"E60")}),1.0]])]});
            var Q1;
            Q1=makeQuery(id+"F30.imprint","IMPRINT",FACE,{"disambiguationData":[TD([[makeQuery(id+"F30.imprint","IMPRINT",EDGE,{"derivedFrom":sQuery(id+"F30.wireOp",EDGE,"E61")}),1.0]])]});
            var Q2;
            Q2=makeQuery(id+"F30.imprint","IMPRINT",FACE,{"disambiguationData":[TD([[makeQuery(id+"F30.imprint","IMPRINT",EDGE,{"derivedFrom":sQuery(id+"F30.wireOp",EDGE,"E62")}),1.0]])]});
            var Q3;
            Q3=makeQuery(id+"F30.imprint","IMPRINT",FACE,{"disambiguationData":[TD([[makeQuery(id+"F30.imprint","IMPRINT",EDGE,{"derivedFrom":sQuery(id+"F30.wireOp",EDGE,"E63")}),1.0]])]});
            extrude(context, id + "F31", {"entities" : qUnion([Q0, Q1, Q2, Q3]), "operationType" : NewBodyOperationType.REMOVE, "oppositeDirection" : true, "depth" : 25 * mm, "offsetDistance" : 25 * mm});
        }
        {
            var Q0;
            {var subQ1=sQuery(id+"F30.wireOp",EDGE,"E57.bottom");Q0=makeQuery(id+"F30.imprint","IMPRINT",FACE,{"disambiguationData":[TD([[makeQuery(id+"F30.imprint","IMPRINT",EDGE,{"derivedFrom":subQ1}),1.0]])]});}
            var Q1;
            {var subQ0=sQuery(id+"F30.wireOp",EDGE,"E59");Q1=makeQuery(id+"F30.imprint","IMPRINT",FACE,{"disambiguationData":[TD([[makeQuery(id+"F30.imprint","IMPRINT",EDGE,{"derivedFrom":subQ0}),1.0]])]});}
            var Q2;
            Q2=makeQuery(id+"F20.opExtrude","CAP_FACE",FACE,{"disambiguationData":[OSD([sQuery(id+"F19.wireOp",EDGE,"E32.bottom"),sQuery(id+"F19.wireOp",EDGE,"E32.top"),sQuery(id+"F19.wireOp",EDGE,"E32.left"),sQuery(id+"F19.wireOp",EDGE,"E32.right"),sQuery(id+"F19.wireOp",EDGE,"E33.0"),sQuery(id+"F19.wireOp",EDGE,"E34.0"),sQuery(id+"F19.wireOp",EDGE,"E35.0"),sQuery(id+"F19.wireOp",EDGE,"E36.0")])],"isStart":false});
            extrude(context, id + "F32", {"entities" : qUnion([Q0, Q1]), "endBound" : BoundingType.UP_TO_SURFACE, "depth" : 25 * mm, "endBoundEntityFace" : qUnion([Q2]), "offsetDistance" : 25 * mm});
        }
        {
            var Q0;
            Q0=makeQuery(id+"F32.opExtrude","SWEPT_FACE",FACE,{"disambiguationData":[OSD([sQuery(id+"F30.wireOp",EDGE,"E59")])]});
            var sketch = newSketch(context, id + "F33", { "sketchPlane" : qUnion([Q0])});
            skCircle(sketch, "E64.cCircle", {"center": v(243.95, 65.74) * mm, "radius": 6.55 * mm, "construction": true});
            skLineSegment(sketch, "E64.0", {"start": v(247.73, 59.2) * mm, "end": v(240.17, 59.2) * mm});
            skLineSegment(sketch, "E64.1", {"start": v(240.17, 59.2) * mm, "end": v(236.39, 65.74) * mm});
            skLineSegment(sketch, "E64.2", {"start": v(236.39, 65.74) * mm, "end": v(240.17, 72.3) * mm});
            skLineSegment(sketch, "E64.3", {"start": v(240.17, 72.3) * mm, "end": v(247.73, 72.3) * mm});
            skLineSegment(sketch, "E64.4", {"start": v(247.73, 72.3) * mm, "end": v(251.51, 65.74) * mm});
            skLineSegment(sketch, "E64.5", {"start": v(251.51, 65.74) * mm, "end": v(247.73, 59.2) * mm});
            skPoint(sketch, "E64.0.midPoint", {"position": v(243.95, 59.2) * mm});
            skLineSegment(sketch, "E65", {"start": v(243.95, 65.74) * mm, "end": v(237.95, 65.74) * mm, "construction": true});
            skCircle(sketch, "E66.0", {"center": v(243.95, -8.26) * mm, "radius": 4 * mm});
            skCircle(sketch, "E67", {"center": v(243.95, 65.74) * mm, "radius": 11.56 * mm});
            skLineSegment(sketch, "E68", {"start": v(237.95, 77.3) * mm, "end": v(243.95, 77.3) * mm});
            skLineSegment(sketch, "E69", {"start": v(237.95, 54.18) * mm, "end": v(243.95, 54.18) * mm});
            skCircle(sketch, "E70", {"center": v(243.95, 65.74) * mm, "radius": 4.25 * mm});
            skSolve(sketch);
        }
        {
            var Q0;
            {var subQ0=sQuery(id+"F33.wireOp",EDGE,"E68");Q0=makeQuery(id+"F33.imprint","IMPRINT",FACE,{"disambiguationData":[TD([[makeQuery(id+"F33.imprint","IMPRINT",EDGE,{"derivedFrom":subQ0}),-1.0]])]});}
            var Q1;
            {var subQ11=sQuery(id+"F33.wireOp",EDGE,"E64.0");Q1=makeQuery(id+"F33.imprint","IMPRINT",FACE,{"disambiguationData":[TD([[makeQuery(id+"F33.imprint","IMPRINT",EDGE,{"derivedFrom":subQ11}),1.0]])]});}
            var Q2;
            {var subQ5=sQuery(id+"F33.wireOp",EDGE,"E64.0");Q2=makeQuery(id+"F33.imprint","IMPRINT",FACE,{"disambiguationData":[TD([[makeQuery(id+"F33.imprint","IMPRINT",EDGE,{"derivedFrom":subQ5}),-1.0]])]});}
            var Q3;
            {var subQ0=sQuery(id+"F33.wireOp",EDGE,"E69");Q3=makeQuery(id+"F33.imprint","IMPRINT",FACE,{"disambiguationData":[TD([[makeQuery(id+"F33.imprint","IMPRINT",EDGE,{"derivedFrom":subQ0}),1.0]])]});}
            var Q4;
            Q4=makeQuery(id+"F32.opExtrude","SWEPT_FACE",FACE,{"disambiguationData":[OSD([sQuery(id+"F30.wireOp",EDGE,"E57.bottom")])]});
            extrude(context, id + "F34", {"entities" : qUnion([Q0, Q1, Q2, Q3]), "operationType" : NewBodyOperationType.ADD, "endBound" : BoundingType.UP_TO_SURFACE, "oppositeDirection" : true, "depth" : 25 * mm, "endBoundEntityFace" : qUnion([Q4]), "offsetDistance" : 25 * mm});
        }
        {
            var Q0;
            {var subQ5=sQuery(id+"F33.wireOp",EDGE,"E64.0");Q0=makeQuery(id+"F33.imprint","IMPRINT",FACE,{"disambiguationData":[TD([[makeQuery(id+"F33.imprint","IMPRINT",EDGE,{"derivedFrom":subQ5}),-1.0]])]});}
            var Q1;
            {var subQ0=sQuery(id+"F33.wireOp",EDGE,"E64.2");var subQ1=sQuery(id+"F33.wireOp",EDGE,"E64.1");var subQ2=makeQuery(id+"F33.imprint","INTERSECT",VERTEX,{"derivedFrom":[subQ1,subQ0]});Q1=makeQuery(id+"F33.imprint","IMPRINT",FACE,{"disambiguationData":[TD([[makeQuery(id+"F33.imprint","IMPRINT",EDGE,{"disambiguationData":[TD([[subQ2,1.0]])],"derivedFrom":subQ1}),-1.0]])]});}
            extrude(context, id + "F35", {"entities" : qUnion([Q0, Q1]), "operationType" : NewBodyOperationType.REMOVE, "oppositeDirection" : true, "depth" : 7 * mm, "offsetDistance" : 25 * mm});
        }
        {
            var Q0;
            {var subQ0=sQuery(id+"F30.wireOp",EDGE,"E57.bottom");Q0=makeQuery(id+"F34.boolean.opBoolean","MERGE",FACE,{"derivedFrom":[makeQuery(id+"F32.opExtrude","SWEPT_FACE",FACE,{"disambiguationData":[OSD([subQ0])]}),makeQuery(id+"F34.opExtrude","CAP_FACE",FACE,{"disambiguationData":[OSD([subQ0])],"isStart":false})]});}
            var sketch = newSketch(context, id + "F36", { "sketchPlane" : qUnion([Q0])});
            skLineSegment(sketch, "E71.0.0", {"start": v(240.17, -72.3) * mm, "end": v(236.39, -65.74) * mm});
            skLineSegment(sketch, "E71.0.1", {"start": v(236.39, -65.74) * mm, "end": v(240.17, -59.2) * mm});
            skLineSegment(sketch, "E71.0.2", {"start": v(240.17, -59.2) * mm, "end": v(247.73, -59.2) * mm});
            skLineSegment(sketch, "E71.0.3", {"start": v(247.73, -59.2) * mm, "end": v(251.51, -65.74) * mm});
            skLineSegment(sketch, "E71.0.4", {"start": v(251.51, -65.74) * mm, "end": v(247.73, -72.3) * mm});
            skLineSegment(sketch, "E71.0.5", {"start": v(247.73, -72.3) * mm, "end": v(240.17, -72.3) * mm});
            skSolve(sketch);
        }
        {
            var Q0;
            Q0=makeQuery(id+"F36.imprint","IMPRINT",FACE,{"disambiguationData":[TD([[makeQuery(id+"F36.imprint","IMPRINT",EDGE,{"derivedFrom":sQuery(id+"F36.wireOp",EDGE,"E71.0.0")}),-1.0]])]});
            extrude(context, id + "F37", {"entities" : qUnion([Q0]), "operationType" : NewBodyOperationType.REMOVE, "oppositeDirection" : true, "depth" : 7 * mm, "offsetDistance" : 25 * mm});
        }
        {
            var Q0;
            {var subQ0=sQuery(id+"F30.wireOp",EDGE,"E57.bottom");Q0=makeQuery(id+"F34.boolean.opBoolean","MERGE",FACE,{"derivedFrom":[makeQuery(id+"F32.opExtrude","SWEPT_FACE",FACE,{"disambiguationData":[OSD([subQ0])]}),makeQuery(id+"F34.opExtrude","CAP_FACE",FACE,{"disambiguationData":[OSD([subQ0])],"isStart":false})]});}
            var sketch = newSketch(context, id + "F38", { "sketchPlane" : qUnion([Q0])});
            skLineSegment(sketch, "E72.0.0", {"start": v(240.17, -72.3) * mm, "end": v(247.73, -72.3) * mm});
            skLineSegment(sketch, "E72.0.1", {"start": v(247.73, -72.3) * mm, "end": v(251.51, -65.74) * mm});
            skLineSegment(sketch, "E72.0.2", {"start": v(251.51, -65.74) * mm, "end": v(247.73, -59.2) * mm});
            skLineSegment(sketch, "E72.0.3", {"start": v(247.73, -59.2) * mm, "end": v(240.17, -59.2) * mm});
            skLineSegment(sketch, "E72.0.4", {"start": v(240.17, -59.2) * mm, "end": v(236.39, -65.74) * mm});
            skLineSegment(sketch, "E72.0.5", {"start": v(236.39, -65.74) * mm, "end": v(240.17, -72.3) * mm});
            skCircle(sketch, "E73.0", {"center": v(243.95, -65.74) * mm, "radius": 4.25 * mm});
            skSolve(sketch);
        }
        {
            var Q0;
            Q0=makeQuery(id+"F38.imprint","IMPRINT",FACE,{"disambiguationData":[TD([[makeQuery(id+"F38.imprint","IMPRINT",EDGE,{"derivedFrom":sQuery(id+"F38.wireOp",EDGE,"E72.0.0")}),-1.0]])]});
            extrude(context, id + "F39", {"entities" : qUnion([Q0]), "oppositeDirection" : true, "depth" : 7 * mm, "offsetDistance" : 25 * mm});
        }
    });
